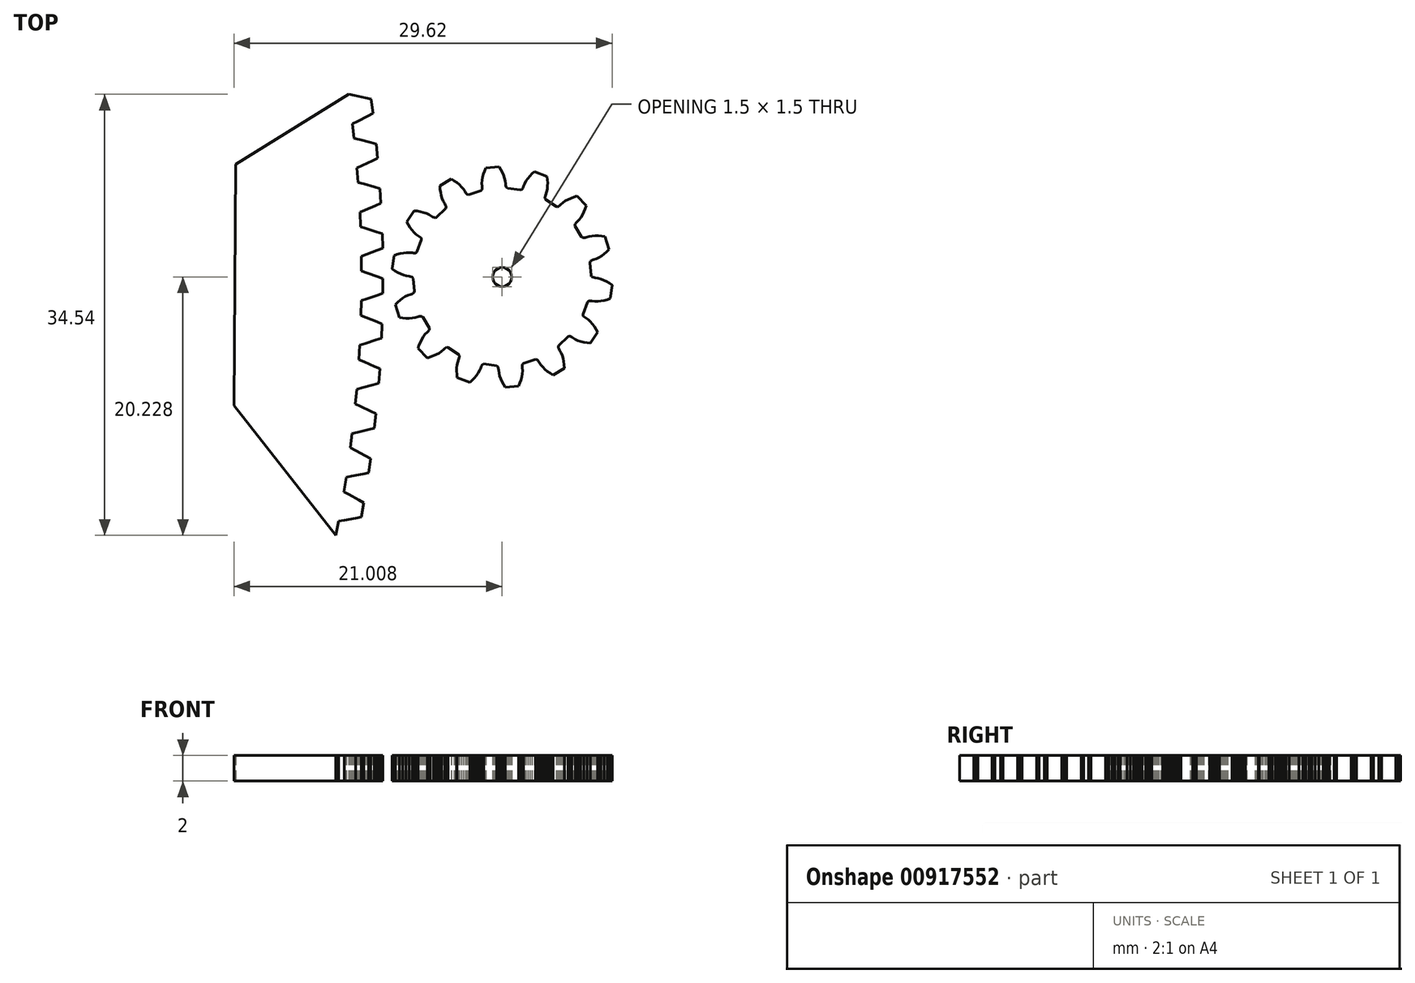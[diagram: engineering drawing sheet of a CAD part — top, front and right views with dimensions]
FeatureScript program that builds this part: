
annotation { "Feature Type Name" : "Feature", "Feature Type Description" : "" }
export const myFeature = defineFeature(function(context is Context, id is Id, definition is map)
    precondition{}
    {
        {
            var Q0;
            Q0=qCreatedBy(makeId("Top.planeOp"),FACE);
            var sketch = newSketch(context, id + "F0", { "sketchPlane" : qUnion([Q0])});
            skLineSegment(sketch, "E0", {"start": v(94.35, 0.47) * mm, "end": v(94.77, 0.32) * mm});
            skLineSegment(sketch, "E1", {"start": v(94.77, 0.32) * mm, "end": v(95.6, 0.02) * mm});
            skLineSegment(sketch, "E2", {"start": v(95.6, 0.02) * mm, "end": v(96.03, -0.14) * mm});
            skLineSegment(sketch, "E3", {"start": v(96.03, -0.14) * mm, "end": v(96.02, -1.27) * mm});
            skLineSegment(sketch, "E4", {"start": v(96.02, -1.27) * mm, "end": v(95.6, -1.43) * mm});
            skLineSegment(sketch, "E5", {"start": v(95.6, -1.43) * mm, "end": v(94.76, -1.72) * mm});
            skLineSegment(sketch, "E6", {"start": v(94.76, -1.72) * mm, "end": v(94.33, -1.86) * mm});
            skLineSegment(sketch, "E7", {"start": v(94.33, -1.86) * mm, "end": v(94.3, -3) * mm});
            skLineSegment(sketch, "E8", {"start": v(94.3, -3) * mm, "end": v(94.72, -3.16) * mm});
            skLineSegment(sketch, "E9", {"start": v(94.72, -3.16) * mm, "end": v(95.55, -3.5) * mm});
            skLineSegment(sketch, "E10", {"start": v(95.55, -3.5) * mm, "end": v(95.97, -3.67) * mm});
            skLineSegment(sketch, "E11", {"start": v(95.97, -3.67) * mm, "end": v(95.92, -4.8) * mm});
            skLineSegment(sketch, "E12", {"start": v(95.92, -4.8) * mm, "end": v(95.5, -4.94) * mm});
            skLineSegment(sketch, "E13", {"start": v(95.5, -4.94) * mm, "end": v(94.64, -5.2) * mm});
            skLineSegment(sketch, "E14", {"start": v(94.64, -5.2) * mm, "end": v(94.21, -5.33) * mm});
            skLineSegment(sketch, "E15", {"start": v(94.21, -5.33) * mm, "end": v(94.15, -6.47) * mm});
            skLineSegment(sketch, "E16", {"start": v(94.15, -6.47) * mm, "end": v(94.56, -6.65) * mm});
            skLineSegment(sketch, "E17", {"start": v(94.56, -6.65) * mm, "end": v(95.37, -7) * mm});
            skLineSegment(sketch, "E18", {"start": v(95.37, -7) * mm, "end": v(95.78, -7.2) * mm});
            skLineSegment(sketch, "E19", {"start": v(95.78, -7.2) * mm, "end": v(95.7, -8.32) * mm});
            skLineSegment(sketch, "E20", {"start": v(95.7, -8.32) * mm, "end": v(95.27, -8.45) * mm});
            skLineSegment(sketch, "E21", {"start": v(95.27, -8.45) * mm, "end": v(94.4, -8.68) * mm});
            skLineSegment(sketch, "E22", {"start": v(94.4, -8.68) * mm, "end": v(93.98, -8.8) * mm});
            skLineSegment(sketch, "E23", {"start": v(93.98, -8.8) * mm, "end": v(93.87, -9.93) * mm});
            skLineSegment(sketch, "E24", {"start": v(93.87, -9.93) * mm, "end": v(94.28, -10.12) * mm});
            skLineSegment(sketch, "E25", {"start": v(94.28, -10.12) * mm, "end": v(95.08, -10.5) * mm});
            skLineSegment(sketch, "E26", {"start": v(95.08, -10.5) * mm, "end": v(95.48, -10.7) * mm});
            skLineSegment(sketch, "E27", {"start": v(95.48, -10.7) * mm, "end": v(95.36, -11.83) * mm});
            skLineSegment(sketch, "E28", {"start": v(95.36, -11.83) * mm, "end": v(94.93, -11.94) * mm});
            skLineSegment(sketch, "E29", {"start": v(94.93, -11.94) * mm, "end": v(94.06, -12.15) * mm});
            skLineSegment(sketch, "E30", {"start": v(94.06, -12.15) * mm, "end": v(93.62, -12.24) * mm});
            skLineSegment(sketch, "E31", {"start": v(93.62, -12.24) * mm, "end": v(93.48, -13.38) * mm});
            skLineSegment(sketch, "E32", {"start": v(93.48, -13.38) * mm, "end": v(93.88, -13.58) * mm});
            skLineSegment(sketch, "E33", {"start": v(93.88, -13.58) * mm, "end": v(94.67, -14) * mm});
            skLineSegment(sketch, "E34", {"start": v(94.67, -14) * mm, "end": v(95.06, -14.21) * mm});
            skLineSegment(sketch, "E35", {"start": v(95.06, -14.21) * mm, "end": v(94.9, -15.33) * mm});
            skLineSegment(sketch, "E36", {"start": v(94.9, -15.33) * mm, "end": v(94.47, -15.43) * mm});
            skLineSegment(sketch, "E37", {"start": v(94.47, -15.43) * mm, "end": v(93.6, -15.6) * mm});
            skLineSegment(sketch, "E38", {"start": v(93.6, -15.6) * mm, "end": v(93.15, -15.68) * mm});
            skLineSegment(sketch, "E39", {"start": v(93.15, -15.68) * mm, "end": v(92.97, -16.82) * mm});
            skLineSegment(sketch, "E40", {"start": v(92.97, -16.82) * mm, "end": v(93.36, -17.03) * mm});
            skLineSegment(sketch, "E41", {"start": v(93.36, -17.03) * mm, "end": v(94.14, -17.47) * mm});
            skLineSegment(sketch, "E42", {"start": v(94.14, -17.47) * mm, "end": v(94.53, -17.7) * mm});
            skLineSegment(sketch, "E43", {"start": v(94.53, -17.7) * mm, "end": v(94.33, -18.81) * mm});
            skLineSegment(sketch, "E44", {"start": v(94.33, -18.81) * mm, "end": v(93.89, -18.9) * mm});
            skLineSegment(sketch, "E45", {"start": v(93.89, -18.9) * mm, "end": v(93, -19.04) * mm});
            skLineSegment(sketch, "E46", {"start": v(93, -19.04) * mm, "end": v(92.57, -19.1) * mm});
            skLineSegment(sketch, "E47", {"start": v(92.57, -19.1) * mm, "end": v(92.35, -20.23) * mm});
            skLineSegment(sketch, "E48", {"start": v(92.35, -20.23) * mm, "end": v(92.73, -20.46) * mm});
            skLineSegment(sketch, "E49", {"start": v(92.73, -20.46) * mm, "end": v(93.5, -20.92) * mm});
            skLineSegment(sketch, "E50", {"start": v(93.5, -20.92) * mm, "end": v(93.87, -21.17) * mm});
            skLineSegment(sketch, "E51", {"start": v(93.87, -21.17) * mm, "end": v(93.64, -22.27) * mm});
            skLineSegment(sketch, "E52", {"start": v(93.64, -22.27) * mm, "end": v(93.2, -22.34) * mm});
            skLineSegment(sketch, "E53", {"start": v(93.2, -22.34) * mm, "end": v(92.31, -22.46) * mm});
            skLineSegment(sketch, "E54", {"start": v(92.31, -22.46) * mm, "end": v(91.87, -22.5) * mm});
            skLineSegment(sketch, "E55", {"start": v(91.87, -22.5) * mm, "end": v(91.61, -23.63) * mm});
            skLineSegment(sketch, "E56", {"start": v(91.61, -23.63) * mm, "end": v(91.99, -23.86) * mm});
            skLineSegment(sketch, "E57", {"start": v(91.99, -23.86) * mm, "end": v(92.73, -24.36) * mm});
            skLineSegment(sketch, "E58", {"start": v(92.73, -24.36) * mm, "end": v(93.1, -24.6) * mm});
            skLineSegment(sketch, "E59", {"start": v(93.1, -24.6) * mm, "end": v(92.83, -25.7) * mm});
            skLineSegment(sketch, "E60", {"start": v(92.83, -25.7) * mm, "end": v(92.39, -25.76) * mm});
            skLineSegment(sketch, "E61", {"start": v(92.39, -25.76) * mm, "end": v(91.5, -25.85) * mm});
            skLineSegment(sketch, "E62", {"start": v(91.5, -25.85) * mm, "end": v(91.06, -25.88) * mm});
            skLineSegment(sketch, "E63", {"start": v(91.06, -25.88) * mm, "end": v(90.76, -27) * mm});
            skLineSegment(sketch, "E64", {"start": v(90.76, -27) * mm, "end": v(91.13, -27.24) * mm});
            skLineSegment(sketch, "E65", {"start": v(91.13, -27.24) * mm, "end": v(91.86, -27.76) * mm});
            skLineSegment(sketch, "E66", {"start": v(91.86, -27.76) * mm, "end": v(92.22, -28.02) * mm});
            skLineSegment(sketch, "E67", {"start": v(92.22, -28.02) * mm, "end": v(91.91, -29.11) * mm});
            skLineSegment(sketch, "E68", {"start": v(91.91, -29.11) * mm, "end": v(91.47, -29.15) * mm});
            skLineSegment(sketch, "E69", {"start": v(91.47, -29.15) * mm, "end": v(90.57, -29.2) * mm});
            skLineSegment(sketch, "E70", {"start": v(90.57, -29.2) * mm, "end": v(90.13, -29.23) * mm});
            skLineSegment(sketch, "E71", {"start": v(90.13, -29.23) * mm, "end": v(89.8, -30.33) * mm});
            skLineSegment(sketch, "E72", {"start": v(89.8, -30.33) * mm, "end": v(90.16, -30.59) * mm});
            skLineSegment(sketch, "E73", {"start": v(90.16, -30.59) * mm, "end": v(90.87, -31.13) * mm});
            skLineSegment(sketch, "E74", {"start": v(90.87, -31.13) * mm, "end": v(91.22, -31.4) * mm});
            skLineSegment(sketch, "E75", {"start": v(91.22, -31.4) * mm, "end": v(90.88, -32.48) * mm});
            skLineSegment(sketch, "E76", {"start": v(90.88, -32.48) * mm, "end": v(90.43, -32.5) * mm});
            skLineSegment(sketch, "E77", {"start": v(90.43, -32.5) * mm, "end": v(89.54, -32.54) * mm});
            skLineSegment(sketch, "E78", {"start": v(89.54, -32.54) * mm, "end": v(89.1, -32.54) * mm});
            skLineSegment(sketch, "E79", {"start": v(89.1, -32.54) * mm, "end": v(88.73, -33.63) * mm});
            skLineSegment(sketch, "E80", {"start": v(88.73, -33.63) * mm, "end": v(89.07, -33.9) * mm});
            skLineSegment(sketch, "E81", {"start": v(89.07, -33.9) * mm, "end": v(89.77, -34.47) * mm});
            skLineSegment(sketch, "E82", {"start": v(89.77, -34.47) * mm, "end": v(90.11, -34.76) * mm});
            skLineSegment(sketch, "E83", {"start": v(90.11, -34.76) * mm, "end": v(89.73, -35.82) * mm});
            skLineSegment(sketch, "E84", {"start": v(89.73, -35.82) * mm, "end": v(89.28, -35.83) * mm});
            skLineSegment(sketch, "E85", {"start": v(89.28, -35.83) * mm, "end": v(88.39, -35.83) * mm});
            skLineSegment(sketch, "E86", {"start": v(88.39, -35.83) * mm, "end": v(87.94, -35.82) * mm});
            skLineSegment(sketch, "E87", {"start": v(87.94, -35.82) * mm, "end": v(87.54, -36.9) * mm});
            skLineSegment(sketch, "E88", {"start": v(87.54, -36.9) * mm, "end": v(87.88, -37.18) * mm});
            skLineSegment(sketch, "E89", {"start": v(87.88, -37.18) * mm, "end": v(88.55, -37.76) * mm});
            skLineSegment(sketch, "E90", {"start": v(88.55, -37.76) * mm, "end": v(88.89, -38.07) * mm});
            skLineSegment(sketch, "E91", {"start": v(88.89, -38.07) * mm, "end": v(88.47, -39.12) * mm});
            skLineSegment(sketch, "E92", {"start": v(88.47, -39.12) * mm, "end": v(88.02, -39.1) * mm});
            skLineSegment(sketch, "E93", {"start": v(88.02, -39.1) * mm, "end": v(87.13, -39.08) * mm});
            skLineSegment(sketch, "E94", {"start": v(87.13, -39.08) * mm, "end": v(86.69, -39.05) * mm});
            skLineSegment(sketch, "E95", {"start": v(86.69, -39.05) * mm, "end": v(86.25, -40.11) * mm});
            skLineSegment(sketch, "E96", {"start": v(86.25, -40.11) * mm, "end": v(86.58, -40.41) * mm});
            skLineSegment(sketch, "E97", {"start": v(86.58, -40.41) * mm, "end": v(87.23, -41.02) * mm});
            skLineSegment(sketch, "E98", {"start": v(87.23, -41.02) * mm, "end": v(87.55, -41.33) * mm});
            skLineSegment(sketch, "E99", {"start": v(87.55, -41.33) * mm, "end": v(87.1, -42.37) * mm});
            skLineSegment(sketch, "E100", {"start": v(87.1, -42.37) * mm, "end": v(86.65, -42.35) * mm});
            skLineSegment(sketch, "E101", {"start": v(86.65, -42.35) * mm, "end": v(85.76, -42.28) * mm});
            skLineSegment(sketch, "E102", {"start": v(85.76, -42.28) * mm, "end": v(85.32, -42.24) * mm});
            skLineSegment(sketch, "E103", {"start": v(85.32, -42.24) * mm, "end": v(84.85, -43.3) * mm});
            skLineSegment(sketch, "E104", {"start": v(84.85, -43.3) * mm, "end": v(85.17, -43.6) * mm});
            skLineSegment(sketch, "E105", {"start": v(85.17, -43.6) * mm, "end": v(85.8, -44.23) * mm});
            skLineSegment(sketch, "E106", {"start": v(85.8, -44.23) * mm, "end": v(86.11, -44.55) * mm});
            skLineSegment(sketch, "E107", {"start": v(86.11, -44.55) * mm, "end": v(85.63, -45.57) * mm});
            skLineSegment(sketch, "E108", {"start": v(85.63, -45.57) * mm, "end": v(85.18, -45.53) * mm});
            skLineSegment(sketch, "E109", {"start": v(85.18, -45.53) * mm, "end": v(84.29, -45.44) * mm});
            skLineSegment(sketch, "E110", {"start": v(84.29, -45.44) * mm, "end": v(83.85, -45.39) * mm});
            skLineSegment(sketch, "E111", {"start": v(83.85, -45.39) * mm, "end": v(83.34, -46.42) * mm});
            skLineSegment(sketch, "E112", {"start": v(83.34, -46.42) * mm, "end": v(83.65, -46.74) * mm});
            skLineSegment(sketch, "E113", {"start": v(83.65, -46.74) * mm, "end": v(84.26, -47.39) * mm});
            skLineSegment(sketch, "E114", {"start": v(84.26, -47.39) * mm, "end": v(84.56, -47.72) * mm});
            skLineSegment(sketch, "E115", {"start": v(84.56, -47.72) * mm, "end": v(84.04, -48.72) * mm});
            skLineSegment(sketch, "E116", {"start": v(84.04, -48.72) * mm, "end": v(83.6, -48.67) * mm});
            skLineSegment(sketch, "E117", {"start": v(83.6, -48.67) * mm, "end": v(82.71, -48.55) * mm});
            skLineSegment(sketch, "E118", {"start": v(82.71, -48.55) * mm, "end": v(82.27, -48.48) * mm});
            skLineSegment(sketch, "E119", {"start": v(82.27, -48.48) * mm, "end": v(81.73, -49.5) * mm});
            skLineSegment(sketch, "E120", {"start": v(81.73, -49.5) * mm, "end": v(82.03, -49.82) * mm});
            skLineSegment(sketch, "E121", {"start": v(82.03, -49.82) * mm, "end": v(82.61, -50.5) * mm});
            skLineSegment(sketch, "E122", {"start": v(82.61, -50.5) * mm, "end": v(82.9, -50.84) * mm});
            skLineSegment(sketch, "E123", {"start": v(82.9, -50.84) * mm, "end": v(82.35, -51.82) * mm});
            skLineSegment(sketch, "E124", {"start": v(82.35, -51.82) * mm, "end": v(81.9, -51.75) * mm});
            skLineSegment(sketch, "E125", {"start": v(81.9, -51.75) * mm, "end": v(81.03, -51.6) * mm});
            skLineSegment(sketch, "E126", {"start": v(81.03, -51.6) * mm, "end": v(80.6, -51.52) * mm});
            skLineSegment(sketch, "E127", {"start": v(80.6, -51.52) * mm, "end": v(80.01, -52.51) * mm});
            skLineSegment(sketch, "E128", {"start": v(80.01, -52.51) * mm, "end": v(80.3, -52.85) * mm});
            skLineSegment(sketch, "E129", {"start": v(80.3, -52.85) * mm, "end": v(80.87, -53.54) * mm});
            skLineSegment(sketch, "E130", {"start": v(80.87, -53.54) * mm, "end": v(81.15, -53.9) * mm});
            skLineSegment(sketch, "E131", {"start": v(81.15, -53.9) * mm, "end": v(80.56, -54.86) * mm});
            skLineSegment(sketch, "E132", {"start": v(80.56, -54.86) * mm, "end": v(80.12, -54.78) * mm});
            skLineSegment(sketch, "E133", {"start": v(80.12, -54.78) * mm, "end": v(79.24, -54.6) * mm});
            skLineSegment(sketch, "E134", {"start": v(79.24, -54.6) * mm, "end": v(78.81, -54.5) * mm});
            skLineSegment(sketch, "E135", {"start": v(78.81, -54.5) * mm, "end": v(78.2, -55.47) * mm});
            skLineSegment(sketch, "E136", {"start": v(78.2, -55.47) * mm, "end": v(78.48, -55.82) * mm});
            skLineSegment(sketch, "E137", {"start": v(78.48, -55.82) * mm, "end": v(79.02, -56.53) * mm});
            skLineSegment(sketch, "E138", {"start": v(79.02, -56.53) * mm, "end": v(79.28, -56.9) * mm});
            skLineSegment(sketch, "E139", {"start": v(79.28, -56.9) * mm, "end": v(78.67, -57.84) * mm});
            skLineSegment(sketch, "E140", {"start": v(78.67, -57.84) * mm, "end": v(78.23, -57.74) * mm});
            skLineSegment(sketch, "E141", {"start": v(78.23, -57.74) * mm, "end": v(77.36, -57.53) * mm});
            skLineSegment(sketch, "E142", {"start": v(77.36, -57.53) * mm, "end": v(76.93, -57.42) * mm});
            skLineSegment(sketch, "E143", {"start": v(76.93, -57.42) * mm, "end": v(76.29, -58.37) * mm});
            skLineSegment(sketch, "E144", {"start": v(76.29, -58.37) * mm, "end": v(76.55, -58.73) * mm});
            skLineSegment(sketch, "E145", {"start": v(76.55, -58.73) * mm, "end": v(77.07, -59.45) * mm});
            skLineSegment(sketch, "E146", {"start": v(77.07, -59.45) * mm, "end": v(77.32, -59.82) * mm});
            skLineSegment(sketch, "E147", {"start": v(77.32, -59.82) * mm, "end": v(76.67, -60.75) * mm});
            skLineSegment(sketch, "E148", {"start": v(76.67, -60.75) * mm, "end": v(76.24, -60.64) * mm});
            skLineSegment(sketch, "E149", {"start": v(76.24, -60.64) * mm, "end": v(75.38, -60.4) * mm});
            skLineSegment(sketch, "E150", {"start": v(75.38, -60.4) * mm, "end": v(74.95, -60.27) * mm});
            skLineSegment(sketch, "E151", {"start": v(74.95, -60.27) * mm, "end": v(74.28, -61.2) * mm});
            skLineSegment(sketch, "E152", {"start": v(74.28, -61.2) * mm, "end": v(74.53, -61.57) * mm});
            skLineSegment(sketch, "E153", {"start": v(74.53, -61.57) * mm, "end": v(75.02, -62.31) * mm});
            skLineSegment(sketch, "E154", {"start": v(75.02, -62.31) * mm, "end": v(75.26, -62.69) * mm});
            skLineSegment(sketch, "E155", {"start": v(75.26, -62.69) * mm, "end": v(74.59, -63.6) * mm});
            skLineSegment(sketch, "E156", {"start": v(74.59, -63.6) * mm, "end": v(74.15, -63.47) * mm});
            skLineSegment(sketch, "E157", {"start": v(74.15, -63.47) * mm, "end": v(73.3, -63.2) * mm});
            skLineSegment(sketch, "E158", {"start": v(73.3, -63.2) * mm, "end": v(72.88, -63.06) * mm});
            skLineSegment(sketch, "E159", {"start": v(72.88, -63.06) * mm, "end": v(72.17, -63.96) * mm});
            skLineSegment(sketch, "E160", {"start": v(72.17, -63.96) * mm, "end": v(72.41, -64.34) * mm});
            skLineSegment(sketch, "E161", {"start": v(72.41, -64.34) * mm, "end": v(72.88, -65.1) * mm});
            skLineSegment(sketch, "E162", {"start": v(72.88, -65.1) * mm, "end": v(73.11, -65.48) * mm});
            skLineSegment(sketch, "E163", {"start": v(73.11, -65.48) * mm, "end": v(72.4, -66.36) * mm});
            skLineSegment(sketch, "E164", {"start": v(72.4, -66.36) * mm, "end": v(71.98, -66.22) * mm});
            skLineSegment(sketch, "E165", {"start": v(71.98, -66.22) * mm, "end": v(71.13, -65.93) * mm});
            skLineSegment(sketch, "E166", {"start": v(71.13, -65.93) * mm, "end": v(70.72, -65.77) * mm});
            skLineSegment(sketch, "E167", {"start": v(70.72, -65.77) * mm, "end": v(69.98, -66.65) * mm});
            skLineSegment(sketch, "E168", {"start": v(69.98, -66.65) * mm, "end": v(70.2, -67.03) * mm});
            skLineSegment(sketch, "E169", {"start": v(70.2, -67.03) * mm, "end": v(70.65, -67.81) * mm});
            skLineSegment(sketch, "E170", {"start": v(70.65, -67.81) * mm, "end": v(70.87, -68.2) * mm});
            skLineSegment(sketch, "E171", {"start": v(70.87, -68.2) * mm, "end": v(70.13, -69.06) * mm});
            skLineSegment(sketch, "E172", {"start": v(70.13, -69.06) * mm, "end": v(69.7, -68.9) * mm});
            skLineSegment(sketch, "E173", {"start": v(69.7, -68.9) * mm, "end": v(68.87, -68.58) * mm});
            skLineSegment(sketch, "E174", {"start": v(68.87, -68.58) * mm, "end": v(68.46, -68.41) * mm});
            skLineSegment(sketch, "E175", {"start": v(68.46, -68.41) * mm, "end": v(67.7, -69.27) * mm});
            skLineSegment(sketch, "E176", {"start": v(67.7, -69.27) * mm, "end": v(67.91, -69.66) * mm});
            skLineSegment(sketch, "E177", {"start": v(67.91, -69.66) * mm, "end": v(68.33, -70.45) * mm});
            skLineSegment(sketch, "E178", {"start": v(68.33, -70.45) * mm, "end": v(68.53, -70.85) * mm});
            skLineSegment(sketch, "E179", {"start": v(68.53, -70.85) * mm, "end": v(67.76, -71.68) * mm});
            skLineSegment(sketch, "E180", {"start": v(67.76, -71.68) * mm, "end": v(67.35, -71.5) * mm});
            skLineSegment(sketch, "E181", {"start": v(67.35, -71.5) * mm, "end": v(66.52, -71.16) * mm});
            skLineSegment(sketch, "E182", {"start": v(66.52, -71.16) * mm, "end": v(66.12, -70.97) * mm});
            skLineSegment(sketch, "E183", {"start": v(66.12, -70.97) * mm, "end": v(65.33, -71.8) * mm});
            skLineSegment(sketch, "E184", {"start": v(65.33, -71.8) * mm, "end": v(65.53, -72.2) * mm});
            skLineSegment(sketch, "E185", {"start": v(65.53, -72.2) * mm, "end": v(65.92, -73) * mm});
            skLineSegment(sketch, "E186", {"start": v(65.92, -73) * mm, "end": v(66.1, -73.41) * mm});
            skLineSegment(sketch, "E187", {"start": v(66.1, -73.41) * mm, "end": v(65.31, -74.22) * mm});
            skLineSegment(sketch, "E188", {"start": v(65.31, -74.22) * mm, "end": v(64.9, -74.03) * mm});
            skLineSegment(sketch, "E189", {"start": v(64.9, -74.03) * mm, "end": v(64.1, -73.65) * mm});
            skLineSegment(sketch, "E190", {"start": v(64.1, -73.65) * mm, "end": v(63.7, -73.46) * mm});
            skLineSegment(sketch, "E191", {"start": v(63.7, -73.46) * mm, "end": v(62.87, -74.26) * mm});
            skLineSegment(sketch, "E192", {"start": v(62.87, -74.26) * mm, "end": v(63.06, -74.66) * mm});
            skLineSegment(sketch, "E193", {"start": v(63.06, -74.66) * mm, "end": v(63.42, -75.48) * mm});
            skLineSegment(sketch, "E194", {"start": v(63.42, -75.48) * mm, "end": v(63.6, -75.9) * mm});
            skLineSegment(sketch, "E195", {"start": v(63.6, -75.9) * mm, "end": v(62.78, -76.67) * mm});
            skLineSegment(sketch, "E196", {"start": v(62.78, -76.67) * mm, "end": v(62.37, -76.47) * mm});
            skLineSegment(sketch, "E197", {"start": v(62.37, -76.47) * mm, "end": v(61.58, -76.07) * mm});
            skLineSegment(sketch, "E198", {"start": v(61.58, -76.07) * mm, "end": v(61.18, -75.86) * mm});
            skLineSegment(sketch, "E199", {"start": v(61.18, -75.86) * mm, "end": v(60.34, -76.63) * mm});
            skLineSegment(sketch, "E200", {"start": v(60.34, -76.63) * mm, "end": v(60.51, -77.04) * mm});
            skLineSegment(sketch, "E201", {"start": v(60.51, -77.04) * mm, "end": v(60.85, -77.87) * mm});
            skLineSegment(sketch, "E202", {"start": v(60.85, -77.87) * mm, "end": v(61, -78.29) * mm});
            skLineSegment(sketch, "E203", {"start": v(61, -78.29) * mm, "end": v(60.16, -79.04) * mm});
            skLineSegment(sketch, "E204", {"start": v(60.16, -79.04) * mm, "end": v(59.76, -78.83) * mm});
            skLineSegment(sketch, "E205", {"start": v(59.76, -78.83) * mm, "end": v(58.98, -78.4) * mm});
            skLineSegment(sketch, "E206", {"start": v(58.98, -78.4) * mm, "end": v(58.6, -78.17) * mm});
            skLineSegment(sketch, "E207", {"start": v(58.6, -78.17) * mm, "end": v(57.72, -78.92) * mm});
            skLineSegment(sketch, "E208", {"start": v(57.72, -78.92) * mm, "end": v(57.88, -79.33) * mm});
            skLineSegment(sketch, "E209", {"start": v(57.88, -79.33) * mm, "end": v(58.2, -80.17) * mm});
            skLineSegment(sketch, "E210", {"start": v(58.2, -80.17) * mm, "end": v(58.34, -80.6) * mm});
            skLineSegment(sketch, "E211", {"start": v(58.34, -80.6) * mm, "end": v(57.47, -81.31) * mm});
            skLineSegment(sketch, "E212", {"start": v(57.47, -81.31) * mm, "end": v(57.08, -81.1) * mm});
            skLineSegment(sketch, "E213", {"start": v(57.08, -81.1) * mm, "end": v(56.3, -80.63) * mm});
            skLineSegment(sketch, "E214", {"start": v(56.3, -80.63) * mm, "end": v(55.93, -80.4) * mm});
            skLineSegment(sketch, "E215", {"start": v(55.93, -80.4) * mm, "end": v(55.04, -81.11) * mm});
            skLineSegment(sketch, "E216", {"start": v(55.04, -81.11) * mm, "end": v(55.18, -81.53) * mm});
            skLineSegment(sketch, "E217", {"start": v(55.18, -81.53) * mm, "end": v(55.46, -82.38) * mm});
            skLineSegment(sketch, "E218", {"start": v(55.46, -82.38) * mm, "end": v(55.6, -82.81) * mm});
            skLineSegment(sketch, "E219", {"start": v(55.6, -82.81) * mm, "end": v(54.7, -83.5) * mm});
            skLineSegment(sketch, "E220", {"start": v(54.7, -83.5) * mm, "end": v(54.31, -83.26) * mm});
            skLineSegment(sketch, "E221", {"start": v(54.31, -83.26) * mm, "end": v(53.56, -82.78) * mm});
            skLineSegment(sketch, "E222", {"start": v(53.56, -82.78) * mm, "end": v(53.2, -82.53) * mm});
            skLineSegment(sketch, "E223", {"start": v(53.2, -82.53) * mm, "end": v(52.27, -83.22) * mm});
            skLineSegment(sketch, "E224", {"start": v(52.27, -83.22) * mm, "end": v(52.4, -83.64) * mm});
            skLineSegment(sketch, "E225", {"start": v(52.4, -83.64) * mm, "end": v(52.66, -84.5) * mm});
            skLineSegment(sketch, "E226", {"start": v(52.66, -84.5) * mm, "end": v(52.77, -84.93) * mm});
            skLineSegment(sketch, "E227", {"start": v(52.77, -84.93) * mm, "end": v(51.86, -85.6) * mm});
            skLineSegment(sketch, "E228", {"start": v(51.86, -85.6) * mm, "end": v(51.48, -85.34) * mm});
            skLineSegment(sketch, "E229", {"start": v(51.48, -85.34) * mm, "end": v(50.75, -84.83) * mm});
            skLineSegment(sketch, "E230", {"start": v(50.75, -84.83) * mm, "end": v(50.39, -84.57) * mm});
            skLineSegment(sketch, "E231", {"start": v(50.39, -84.57) * mm, "end": v(49.44, -85.23) * mm});
            skLineSegment(sketch, "E232", {"start": v(49.44, -85.23) * mm, "end": v(49.56, -85.66) * mm});
            skLineSegment(sketch, "E233", {"start": v(49.56, -85.66) * mm, "end": v(49.78, -86.52) * mm});
            skLineSegment(sketch, "E234", {"start": v(49.78, -86.52) * mm, "end": v(49.89, -86.96) * mm});
            skLineSegment(sketch, "E235", {"start": v(49.89, -86.96) * mm, "end": v(48.95, -87.59) * mm});
            skLineSegment(sketch, "E236", {"start": v(48.95, -87.59) * mm, "end": v(48.58, -87.33) * mm});
            skLineSegment(sketch, "E237", {"start": v(48.58, -87.33) * mm, "end": v(47.86, -86.8) * mm});
            skLineSegment(sketch, "E238", {"start": v(47.86, -86.8) * mm, "end": v(47.51, -86.52) * mm});
            skLineSegment(sketch, "E239", {"start": v(47.51, -86.52) * mm, "end": v(46.55, -87.14) * mm});
            skLineSegment(sketch, "E240", {"start": v(46.55, -87.14) * mm, "end": v(46.65, -87.57) * mm});
            skLineSegment(sketch, "E241", {"start": v(46.65, -87.57) * mm, "end": v(46.84, -88.45) * mm});
            skLineSegment(sketch, "E242", {"start": v(46.84, -88.45) * mm, "end": v(46.93, -88.89) * mm});
            skLineSegment(sketch, "E243", {"start": v(46.93, -88.89) * mm, "end": v(45.97, -89.48) * mm});
            skLineSegment(sketch, "E244", {"start": v(45.97, -89.48) * mm, "end": v(45.61, -89.21) * mm});
            skLineSegment(sketch, "E245", {"start": v(45.61, -89.21) * mm, "end": v(44.92, -88.65) * mm});
            skLineSegment(sketch, "E246", {"start": v(44.92, -88.65) * mm, "end": v(44.58, -88.37) * mm});
            skLineSegment(sketch, "E247", {"start": v(44.58, -88.37) * mm, "end": v(43.59, -88.96) * mm});
            skLineSegment(sketch, "E248", {"start": v(43.59, -88.96) * mm, "end": v(43.68, -89.4) * mm});
            skLineSegment(sketch, "E249", {"start": v(43.68, -89.4) * mm, "end": v(43.84, -90.27) * mm});
            skLineSegment(sketch, "E250", {"start": v(43.84, -90.27) * mm, "end": v(43.91, -90.72) * mm});
            skLineSegment(sketch, "E251", {"start": v(43.91, -90.72) * mm, "end": v(42.93, -91.28) * mm});
            skLineSegment(sketch, "E252", {"start": v(42.93, -91.28) * mm, "end": v(42.59, -91) * mm});
            skLineSegment(sketch, "E253", {"start": v(42.59, -91) * mm, "end": v(41.9, -90.41) * mm});
            skLineSegment(sketch, "E254", {"start": v(41.9, -90.41) * mm, "end": v(41.58, -90.12) * mm});
            skLineSegment(sketch, "E255", {"start": v(41.58, -90.12) * mm, "end": v(40.57, -90.67) * mm});
            skLineSegment(sketch, "E256", {"start": v(40.57, -90.67) * mm, "end": v(40.65, -91.11) * mm});
            skLineSegment(sketch, "E257", {"start": v(40.65, -91.11) * mm, "end": v(40.78, -92) * mm});
            skLineSegment(sketch, "E258", {"start": v(40.78, -92) * mm, "end": v(40.84, -92.44) * mm});
            skLineSegment(sketch, "E259", {"start": v(40.84, -92.44) * mm, "end": v(39.84, -92.97) * mm});
            skLineSegment(sketch, "E260", {"start": v(39.84, -92.97) * mm, "end": v(39.5, -92.67) * mm});
            skLineSegment(sketch, "E261", {"start": v(39.5, -92.67) * mm, "end": v(38.84, -92.07) * mm});
            skLineSegment(sketch, "E262", {"start": v(38.84, -92.07) * mm, "end": v(38.52, -91.77) * mm});
            skLineSegment(sketch, "E263", {"start": v(38.52, -91.77) * mm, "end": v(37.5, -92.29) * mm});
            skLineSegment(sketch, "E264", {"start": v(37.5, -92.29) * mm, "end": v(37.56, -92.73) * mm});
            skLineSegment(sketch, "E265", {"start": v(37.56, -92.73) * mm, "end": v(37.66, -93.62) * mm});
            skLineSegment(sketch, "E266", {"start": v(37.66, -93.62) * mm, "end": v(37.7, -94.06) * mm});
            skLineSegment(sketch, "E267", {"start": v(37.7, -94.06) * mm, "end": v(36.69, -94.56) * mm});
            skLineSegment(sketch, "E268", {"start": v(36.69, -94.56) * mm, "end": v(36.36, -94.25) * mm});
            skLineSegment(sketch, "E269", {"start": v(36.36, -94.25) * mm, "end": v(35.72, -93.63) * mm});
            skLineSegment(sketch, "E270", {"start": v(35.72, -93.63) * mm, "end": v(35.41, -93.3) * mm});
            skLineSegment(sketch, "E271", {"start": v(35.41, -93.3) * mm, "end": v(34.37, -93.8) * mm});
            skLineSegment(sketch, "E272", {"start": v(34.37, -93.8) * mm, "end": v(34.42, -94.24) * mm});
            skLineSegment(sketch, "E273", {"start": v(34.42, -94.24) * mm, "end": v(34.49, -95.13) * mm});
            skLineSegment(sketch, "E274", {"start": v(34.49, -95.13) * mm, "end": v(34.52, -95.58) * mm});
            skLineSegment(sketch, "E275", {"start": v(34.52, -95.58) * mm, "end": v(33.49, -96.04) * mm});
            skLineSegment(sketch, "E276", {"start": v(33.49, -96.04) * mm, "end": v(33.17, -95.72) * mm});
            skLineSegment(sketch, "E277", {"start": v(33.17, -95.72) * mm, "end": v(32.55, -95.07) * mm});
            skLineSegment(sketch, "E278", {"start": v(32.55, -95.07) * mm, "end": v(32.25, -94.75) * mm});
            skLineSegment(sketch, "E279", {"start": v(32.25, -94.75) * mm, "end": v(31.2, -95.2) * mm});
            skLineSegment(sketch, "E280", {"start": v(31.2, -95.2) * mm, "end": v(31.23, -95.64) * mm});
            skLineSegment(sketch, "E281", {"start": v(31.23, -95.64) * mm, "end": v(31.27, -96.54) * mm});
            skLineSegment(sketch, "E282", {"start": v(31.27, -96.54) * mm, "end": v(31.28, -96.98) * mm});
            skLineSegment(sketch, "E283", {"start": v(31.28, -96.98) * mm, "end": v(30.24, -97.41) * mm});
            skLineSegment(sketch, "E284", {"start": v(30.24, -97.41) * mm, "end": v(29.93, -97.08) * mm});
            skLineSegment(sketch, "E285", {"start": v(29.93, -97.08) * mm, "end": v(29.33, -96.42) * mm});
            skLineSegment(sketch, "E286", {"start": v(29.33, -96.42) * mm, "end": v(29.05, -96.08) * mm});
            skLineSegment(sketch, "E287", {"start": v(29.05, -96.08) * mm, "end": v(27.98, -96.5) * mm});
            skLineSegment(sketch, "E288", {"start": v(27.98, -96.5) * mm, "end": v(27.99, -96.94) * mm});
            skLineSegment(sketch, "E289", {"start": v(27.99, -96.94) * mm, "end": v(28, -97.83) * mm});
            skLineSegment(sketch, "E290", {"start": v(28, -97.83) * mm, "end": v(28, -98.28) * mm});
            skLineSegment(sketch, "E291", {"start": v(28, -98.28) * mm, "end": v(26.94, -98.67) * mm});
            skLineSegment(sketch, "E292", {"start": v(26.94, -98.67) * mm, "end": v(26.65, -98.33) * mm});
            skLineSegment(sketch, "E293", {"start": v(26.65, -98.33) * mm, "end": v(26.07, -97.65) * mm});
            skLineSegment(sketch, "E294", {"start": v(26.07, -97.65) * mm, "end": v(25.8, -97.3) * mm});
            skLineSegment(sketch, "E295", {"start": v(25.8, -97.3) * mm, "end": v(24.71, -97.68) * mm});
            skLineSegment(sketch, "E296", {"start": v(24.71, -97.68) * mm, "end": v(24.71, -98.13) * mm});
            skLineSegment(sketch, "E297", {"start": v(24.71, -98.13) * mm, "end": v(24.7, -99.02) * mm});
            skLineSegment(sketch, "E298", {"start": v(24.7, -99.02) * mm, "end": v(24.68, -99.47) * mm});
            skLineSegment(sketch, "E299", {"start": v(24.68, -99.47) * mm, "end": v(23.6, -99.83) * mm});
            skLineSegment(sketch, "E300", {"start": v(23.6, -99.83) * mm, "end": v(23.32, -99.48) * mm});
            skLineSegment(sketch, "E301", {"start": v(23.32, -99.48) * mm, "end": v(22.77, -98.77) * mm});
            skLineSegment(sketch, "E302", {"start": v(22.77, -98.77) * mm, "end": v(22.5, -98.42) * mm});
            skLineSegment(sketch, "E303", {"start": v(22.5, -98.42) * mm, "end": v(21.41, -98.76) * mm});
            skLineSegment(sketch, "E304", {"start": v(21.41, -98.76) * mm, "end": v(21.4, -99.2) * mm});
            skLineSegment(sketch, "E305", {"start": v(21.4, -99.2) * mm, "end": v(21.35, -100.1) * mm});
            skLineSegment(sketch, "E306", {"start": v(21.35, -100.1) * mm, "end": v(21.32, -100.54) * mm});
            skLineSegment(sketch, "E307", {"start": v(21.32, -100.54) * mm, "end": v(20.23, -100.86) * mm});
            skLineSegment(sketch, "E308", {"start": v(20.23, -100.86) * mm, "end": v(19.96, -100.5) * mm});
            skLineSegment(sketch, "E309", {"start": v(19.96, -100.5) * mm, "end": v(19.44, -99.78) * mm});
            skLineSegment(sketch, "E310", {"start": v(19.44, -99.78) * mm, "end": v(19.18, -99.42) * mm});
            skLineSegment(sketch, "E311", {"start": v(19.18, -99.42) * mm, "end": v(18.08, -99.72) * mm});
            skLineSegment(sketch, "E312", {"start": v(18.08, -99.72) * mm, "end": v(18.05, -100.17) * mm});
            skLineSegment(sketch, "E313", {"start": v(18.05, -100.17) * mm, "end": v(17.97, -101.06) * mm});
            skLineSegment(sketch, "E314", {"start": v(17.97, -101.06) * mm, "end": v(17.92, -101.5) * mm});
            skLineSegment(sketch, "E315", {"start": v(17.92, -101.5) * mm, "end": v(16.83, -101.79) * mm});
            skLineSegment(sketch, "E316", {"start": v(16.83, -101.79) * mm, "end": v(16.57, -101.42) * mm});
            skLineSegment(sketch, "E317", {"start": v(16.57, -101.42) * mm, "end": v(16.07, -100.68) * mm});
            skLineSegment(sketch, "E318", {"start": v(16.07, -100.68) * mm, "end": v(15.83, -100.3) * mm});
            skLineSegment(sketch, "E319", {"start": v(15.83, -100.3) * mm, "end": v(14.71, -100.58) * mm});
            skLineSegment(sketch, "E320", {"start": v(14.71, -100.58) * mm, "end": v(14.67, -101.02) * mm});
            skLineSegment(sketch, "E321", {"start": v(14.67, -101.02) * mm, "end": v(14.56, -101.9) * mm});
            skLineSegment(sketch, "E322", {"start": v(14.56, -101.9) * mm, "end": v(14.5, -102.35) * mm});
            skLineSegment(sketch, "E323", {"start": v(14.5, -102.35) * mm, "end": v(13.4, -102.6) * mm});
            skLineSegment(sketch, "E324", {"start": v(13.4, -102.6) * mm, "end": v(13.15, -102.22) * mm});
            skLineSegment(sketch, "E325", {"start": v(13.15, -102.22) * mm, "end": v(12.67, -101.46) * mm});
            skLineSegment(sketch, "E326", {"start": v(12.67, -101.46) * mm, "end": v(12.45, -101.08) * mm});
            skLineSegment(sketch, "E327", {"start": v(12.45, -101.08) * mm, "end": v(11.32, -101.32) * mm});
            skLineSegment(sketch, "E328", {"start": v(11.32, -101.32) * mm, "end": v(11.26, -101.76) * mm});
            skLineSegment(sketch, "E329", {"start": v(11.26, -101.76) * mm, "end": v(11.12, -102.64) * mm});
            skLineSegment(sketch, "E330", {"start": v(11.12, -102.64) * mm, "end": v(11.05, -103.08) * mm});
            skLineSegment(sketch, "E331", {"start": v(11.05, -103.08) * mm, "end": v(9.94, -103.3) * mm});
            skLineSegment(sketch, "E332", {"start": v(9.94, -103.3) * mm, "end": v(9.7, -102.9) * mm});
            skLineSegment(sketch, "E333", {"start": v(9.7, -102.9) * mm, "end": v(9.25, -102.13) * mm});
            skLineSegment(sketch, "E334", {"start": v(9.25, -102.13) * mm, "end": v(9.04, -101.75) * mm});
            skLineSegment(sketch, "E335", {"start": v(9.04, -101.75) * mm, "end": v(7.9, -101.94) * mm});
            skLineSegment(sketch, "E336", {"start": v(7.9, -101.94) * mm, "end": v(7.83, -102.38) * mm});
            skLineSegment(sketch, "E337", {"start": v(7.83, -102.38) * mm, "end": v(7.66, -103.26) * mm});
            skLineSegment(sketch, "E338", {"start": v(7.66, -103.26) * mm, "end": v(7.57, -103.7) * mm});
            skLineSegment(sketch, "E339", {"start": v(7.57, -103.7) * mm, "end": v(6.46, -103.87) * mm});
            skLineSegment(sketch, "E340", {"start": v(6.46, -103.87) * mm, "end": v(6.24, -103.48) * mm});
            skLineSegment(sketch, "E341", {"start": v(6.24, -103.48) * mm, "end": v(5.81, -102.69) * mm});
            skLineSegment(sketch, "E342", {"start": v(5.81, -102.69) * mm, "end": v(5.6, -102.3) * mm});
            skLineSegment(sketch, "E343", {"start": v(5.6, -102.3) * mm, "end": v(4.47, -102.45) * mm});
            skLineSegment(sketch, "E344", {"start": v(4.47, -102.45) * mm, "end": v(4.38, -102.89) * mm});
            skLineSegment(sketch, "E345", {"start": v(4.38, -102.89) * mm, "end": v(4.19, -103.76) * mm});
            skLineSegment(sketch, "E346", {"start": v(4.19, -103.76) * mm, "end": v(4.08, -104.2) * mm});
            skLineSegment(sketch, "E347", {"start": v(4.08, -104.2) * mm, "end": v(2.96, -104.33) * mm});
            skLineSegment(sketch, "E348", {"start": v(2.96, -104.33) * mm, "end": v(2.75, -103.93) * mm});
            skLineSegment(sketch, "E349", {"start": v(2.75, -103.93) * mm, "end": v(2.35, -103.13) * mm});
            skLineSegment(sketch, "E350", {"start": v(2.35, -103.13) * mm, "end": v(2.16, -102.73) * mm});
            skLineSegment(sketch, "E351", {"start": v(2.16, -102.73) * mm, "end": v(1.02, -102.84) * mm});
            skLineSegment(sketch, "E352", {"start": v(1.02, -102.84) * mm, "end": v(0.92, -103.28) * mm});
            skLineSegment(sketch, "E353", {"start": v(0.92, -103.28) * mm, "end": v(0.7, -104.14) * mm});
            skLineSegment(sketch, "E354", {"start": v(0.7, -104.14) * mm, "end": v(0.57, -104.57) * mm});
            skLineSegment(sketch, "E355", {"start": v(0.57, -104.57) * mm, "end": v(-0.55, -104.67) * mm});
            skLineSegment(sketch, "E356", {"start": v(-0.55, -104.67) * mm, "end": v(-0.75, -104.26) * mm});
            skLineSegment(sketch, "E357", {"start": v(-0.75, -104.26) * mm, "end": v(-1.12, -103.45) * mm});
            skLineSegment(sketch, "E358", {"start": v(-1.12, -103.45) * mm, "end": v(-1.3, -103.04) * mm});
            skLineSegment(sketch, "E359", {"start": v(-1.3, -103.04) * mm, "end": v(-2.44, -103.12) * mm});
            skLineSegment(sketch, "E360", {"start": v(-2.44, -103.12) * mm, "end": v(-2.56, -103.55) * mm});
            skLineSegment(sketch, "E361", {"start": v(-2.56, -103.55) * mm, "end": v(-2.81, -104.4) * mm});
            skLineSegment(sketch, "E362", {"start": v(-2.81, -104.4) * mm, "end": v(-2.95, -104.84) * mm});
            skLineSegment(sketch, "E363", {"start": v(-2.95, -104.84) * mm, "end": v(-4.08, -104.9) * mm});
            skLineSegment(sketch, "E364", {"start": v(-4.08, -104.9) * mm, "end": v(-4.25, -104.48) * mm});
            skLineSegment(sketch, "E365", {"start": v(-4.25, -104.48) * mm, "end": v(-4.6, -103.66) * mm});
            skLineSegment(sketch, "E366", {"start": v(-4.6, -103.66) * mm, "end": v(-4.76, -103.24) * mm});
            skLineSegment(sketch, "E367", {"start": v(-4.76, -103.24) * mm, "end": v(-5.9, -103.28) * mm});
            skLineSegment(sketch, "E368", {"start": v(-5.9, -103.28) * mm, "end": v(-6.04, -103.7) * mm});
            skLineSegment(sketch, "E369", {"start": v(-6.04, -103.7) * mm, "end": v(-6.32, -104.56) * mm});
            skLineSegment(sketch, "E370", {"start": v(-6.32, -104.56) * mm, "end": v(-6.47, -104.98) * mm});
            skLineSegment(sketch, "E371", {"start": v(-6.47, -104.98) * mm, "end": v(-7.6, -105) * mm});
            skLineSegment(sketch, "E372", {"start": v(-7.6, -105) * mm, "end": v(-7.77, -104.58) * mm});
            skLineSegment(sketch, "E373", {"start": v(-7.77, -104.58) * mm, "end": v(-8.08, -103.75) * mm});
            skLineSegment(sketch, "E374", {"start": v(-8.08, -103.75) * mm, "end": v(-8.23, -103.33) * mm});
            skLineSegment(sketch, "E375", {"start": v(-8.23, -103.33) * mm, "end": v(-9.38, -103.33) * mm});
            skLineSegment(sketch, "E376", {"start": v(-9.38, -103.33) * mm, "end": v(-9.52, -103.75) * mm});
            skLineSegment(sketch, "E377", {"start": v(-9.52, -103.75) * mm, "end": v(-9.84, -104.59) * mm});
            skLineSegment(sketch, "E378", {"start": v(-9.84, -104.59) * mm, "end": v(-10, -105) * mm});
            skLineSegment(sketch, "E379", {"start": v(-10, -105) * mm, "end": v(-11.13, -104.99) * mm});
            skLineSegment(sketch, "E380", {"start": v(-11.13, -104.99) * mm, "end": v(-11.28, -104.56) * mm});
            skLineSegment(sketch, "E381", {"start": v(-11.28, -104.56) * mm, "end": v(-11.57, -103.72) * mm});
            skLineSegment(sketch, "E382", {"start": v(-11.57, -103.72) * mm, "end": v(-11.7, -103.3) * mm});
            skLineSegment(sketch, "E383", {"start": v(-11.7, -103.3) * mm, "end": v(-12.85, -103.26) * mm});
            skLineSegment(sketch, "E384", {"start": v(-12.85, -103.26) * mm, "end": v(-13, -103.67) * mm});
            skLineSegment(sketch, "E385", {"start": v(-13, -103.67) * mm, "end": v(-13.35, -104.5) * mm});
            skLineSegment(sketch, "E386", {"start": v(-13.35, -104.5) * mm, "end": v(-13.53, -104.91) * mm});
            skLineSegment(sketch, "E387", {"start": v(-13.53, -104.91) * mm, "end": v(-14.66, -104.86) * mm});
            skLineSegment(sketch, "E388", {"start": v(-14.66, -104.86) * mm, "end": v(-14.8, -104.43) * mm});
            skLineSegment(sketch, "E389", {"start": v(-14.8, -104.43) * mm, "end": v(-15.05, -103.57) * mm});
            skLineSegment(sketch, "E390", {"start": v(-15.05, -103.57) * mm, "end": v(-15.17, -103.14) * mm});
            skLineSegment(sketch, "E391", {"start": v(-15.17, -103.14) * mm, "end": v(-16.32, -103.07) * mm});
            skLineSegment(sketch, "E392", {"start": v(-16.32, -103.07) * mm, "end": v(-16.49, -103.48) * mm});
            skLineSegment(sketch, "E393", {"start": v(-16.49, -103.48) * mm, "end": v(-16.86, -104.3) * mm});
            skLineSegment(sketch, "E394", {"start": v(-16.86, -104.3) * mm, "end": v(-17.05, -104.7) * mm});
            skLineSegment(sketch, "E395", {"start": v(-17.05, -104.7) * mm, "end": v(-18.17, -104.6) * mm});
            skLineSegment(sketch, "E396", {"start": v(-18.17, -104.6) * mm, "end": v(-18.3, -104.17) * mm});
            skLineSegment(sketch, "E397", {"start": v(-18.3, -104.17) * mm, "end": v(-18.53, -103.3) * mm});
            skLineSegment(sketch, "E398", {"start": v(-18.53, -103.3) * mm, "end": v(-18.63, -102.88) * mm});
            skLineSegment(sketch, "E399", {"start": v(-18.63, -102.88) * mm, "end": v(-19.77, -102.76) * mm});
            skLineSegment(sketch, "E400", {"start": v(-19.77, -102.76) * mm, "end": v(-19.96, -103.17) * mm});
            skLineSegment(sketch, "E401", {"start": v(-19.96, -103.17) * mm, "end": v(-20.36, -103.97) * mm});
            skLineSegment(sketch, "E402", {"start": v(-20.36, -103.97) * mm, "end": v(-20.56, -104.37) * mm});
            skLineSegment(sketch, "E403", {"start": v(-20.56, -104.37) * mm, "end": v(-21.68, -104.24) * mm});
            skLineSegment(sketch, "E404", {"start": v(-21.68, -104.24) * mm, "end": v(-21.8, -103.8) * mm});
            skLineSegment(sketch, "E405", {"start": v(-21.8, -103.8) * mm, "end": v(-22, -102.93) * mm});
            skLineSegment(sketch, "E406", {"start": v(-22, -102.93) * mm, "end": v(-22.08, -102.5) * mm});
            skLineSegment(sketch, "E407", {"start": v(-22.08, -102.5) * mm, "end": v(-23.22, -102.34) * mm});
            skLineSegment(sketch, "E408", {"start": v(-23.22, -102.34) * mm, "end": v(-23.42, -102.74) * mm});
            skLineSegment(sketch, "E409", {"start": v(-23.42, -102.74) * mm, "end": v(-23.84, -103.53) * mm});
            skLineSegment(sketch, "E410", {"start": v(-23.84, -103.53) * mm, "end": v(-24.06, -103.92) * mm});
            skLineSegment(sketch, "E411", {"start": v(-24.06, -103.92) * mm, "end": v(-25.18, -103.75) * mm});
            skLineSegment(sketch, "E412", {"start": v(-25.18, -103.75) * mm, "end": v(-25.27, -103.31) * mm});
            skLineSegment(sketch, "E413", {"start": v(-25.27, -103.31) * mm, "end": v(-25.44, -102.43) * mm});
            skLineSegment(sketch, "E414", {"start": v(-25.44, -102.43) * mm, "end": v(-25.52, -102) * mm});
            skLineSegment(sketch, "E415", {"start": v(-25.52, -102) * mm, "end": v(-26.65, -101.8) * mm});
            skLineSegment(sketch, "E416", {"start": v(-26.65, -101.8) * mm, "end": v(-26.86, -102.2) * mm});
            skLineSegment(sketch, "E417", {"start": v(-26.86, -102.2) * mm, "end": v(-27.31, -102.97) * mm});
            skLineSegment(sketch, "E418", {"start": v(-27.31, -102.97) * mm, "end": v(-27.54, -103.35) * mm});
            skLineSegment(sketch, "E419", {"start": v(-27.54, -103.35) * mm, "end": v(-28.65, -103.15) * mm});
            skLineSegment(sketch, "E420", {"start": v(-28.65, -103.15) * mm, "end": v(-28.73, -102.7) * mm});
            skLineSegment(sketch, "E421", {"start": v(-28.73, -102.7) * mm, "end": v(-28.87, -101.82) * mm});
            skLineSegment(sketch, "E422", {"start": v(-28.87, -101.82) * mm, "end": v(-28.93, -101.38) * mm});
            skLineSegment(sketch, "E423", {"start": v(-28.93, -101.38) * mm, "end": v(-30.06, -101.16) * mm});
            skLineSegment(sketch, "E424", {"start": v(-30.06, -101.16) * mm, "end": v(-30.29, -101.54) * mm});
            skLineSegment(sketch, "E425", {"start": v(-30.29, -101.54) * mm, "end": v(-30.76, -102.3) * mm});
            skLineSegment(sketch, "E426", {"start": v(-30.76, -102.3) * mm, "end": v(-31, -102.67) * mm});
            skLineSegment(sketch, "E427", {"start": v(-31, -102.67) * mm, "end": v(-32.1, -102.43) * mm});
            skLineSegment(sketch, "E428", {"start": v(-32.1, -102.43) * mm, "end": v(-32.17, -101.98) * mm});
            skLineSegment(sketch, "E429", {"start": v(-32.17, -101.98) * mm, "end": v(-32.28, -101.1) * mm});
            skLineSegment(sketch, "E430", {"start": v(-32.28, -101.1) * mm, "end": v(-32.33, -100.66) * mm});
            skLineSegment(sketch, "E431", {"start": v(-32.33, -100.66) * mm, "end": v(-33.45, -100.4) * mm});
            skLineSegment(sketch, "E432", {"start": v(-33.45, -100.4) * mm, "end": v(-33.69, -100.76) * mm});
            skLineSegment(sketch, "E433", {"start": v(-33.69, -100.76) * mm, "end": v(-34.18, -101.5) * mm});
            skLineSegment(sketch, "E434", {"start": v(-34.18, -101.5) * mm, "end": v(-34.44, -101.87) * mm});
            skLineSegment(sketch, "E435", {"start": v(-34.44, -101.87) * mm, "end": v(-35.54, -101.6) * mm});
            skLineSegment(sketch, "E436", {"start": v(-35.54, -101.6) * mm, "end": v(-35.58, -101.15) * mm});
            skLineSegment(sketch, "E437", {"start": v(-35.58, -101.15) * mm, "end": v(-35.66, -100.26) * mm});
            skLineSegment(sketch, "E438", {"start": v(-35.66, -100.26) * mm, "end": v(-35.7, -99.81) * mm});
            skLineSegment(sketch, "E439", {"start": v(-35.7, -99.81) * mm, "end": v(-36.8, -99.51) * mm});
            skLineSegment(sketch, "E440", {"start": v(-36.8, -99.51) * mm, "end": v(-37.06, -99.88) * mm});
            skLineSegment(sketch, "E441", {"start": v(-37.06, -99.88) * mm, "end": v(-37.58, -100.6) * mm});
            skLineSegment(sketch, "E442", {"start": v(-37.58, -100.6) * mm, "end": v(-37.85, -100.96) * mm});
            skLineSegment(sketch, "E443", {"start": v(-37.85, -100.96) * mm, "end": v(-38.93, -100.65) * mm});
            skLineSegment(sketch, "E444", {"start": v(-38.93, -100.65) * mm, "end": v(-38.97, -100.2) * mm});
            skLineSegment(sketch, "E445", {"start": v(-38.97, -100.2) * mm, "end": v(-39.02, -99.3) * mm});
            skLineSegment(sketch, "E446", {"start": v(-39.02, -99.3) * mm, "end": v(-39.03, -98.86) * mm});
            skLineSegment(sketch, "E447", {"start": v(-39.03, -98.86) * mm, "end": v(-40.13, -98.52) * mm});
            skLineSegment(sketch, "E448", {"start": v(-40.13, -98.52) * mm, "end": v(-40.4, -98.88) * mm});
            skLineSegment(sketch, "E449", {"start": v(-40.4, -98.88) * mm, "end": v(-40.94, -99.58) * mm});
            skLineSegment(sketch, "E450", {"start": v(-40.94, -99.58) * mm, "end": v(-41.22, -99.93) * mm});
            skLineSegment(sketch, "E451", {"start": v(-41.22, -99.93) * mm, "end": v(-42.3, -99.58) * mm});
            skLineSegment(sketch, "E452", {"start": v(-42.3, -99.58) * mm, "end": v(-42.32, -99.13) * mm});
            skLineSegment(sketch, "E453", {"start": v(-42.32, -99.13) * mm, "end": v(-42.34, -98.24) * mm});
            skLineSegment(sketch, "E454", {"start": v(-42.34, -98.24) * mm, "end": v(-42.34, -97.8) * mm});
            skLineSegment(sketch, "E455", {"start": v(-42.34, -97.8) * mm, "end": v(-43.42, -97.42) * mm});
            skLineSegment(sketch, "E456", {"start": v(-43.42, -97.42) * mm, "end": v(-43.7, -97.77) * mm});
            skLineSegment(sketch, "E457", {"start": v(-43.7, -97.77) * mm, "end": v(-44.27, -98.45) * mm});
            skLineSegment(sketch, "E458", {"start": v(-44.27, -98.45) * mm, "end": v(-44.56, -98.8) * mm});
            skLineSegment(sketch, "E459", {"start": v(-44.56, -98.8) * mm, "end": v(-45.62, -98.4) * mm});
            skLineSegment(sketch, "E460", {"start": v(-45.62, -98.4) * mm, "end": v(-45.63, -97.96) * mm});
            skLineSegment(sketch, "E461", {"start": v(-45.63, -97.96) * mm, "end": v(-45.62, -97.06) * mm});
            skLineSegment(sketch, "E462", {"start": v(-45.62, -97.06) * mm, "end": v(-45.6, -96.62) * mm});
            skLineSegment(sketch, "E463", {"start": v(-45.6, -96.62) * mm, "end": v(-46.68, -96.2) * mm});
            skLineSegment(sketch, "E464", {"start": v(-46.68, -96.2) * mm, "end": v(-46.96, -96.54) * mm});
            skLineSegment(sketch, "E465", {"start": v(-46.96, -96.54) * mm, "end": v(-47.56, -97.21) * mm});
            skLineSegment(sketch, "E466", {"start": v(-47.56, -97.21) * mm, "end": v(-47.86, -97.54) * mm});
            skLineSegment(sketch, "E467", {"start": v(-47.86, -97.54) * mm, "end": v(-48.9, -97.12) * mm});
            skLineSegment(sketch, "E468", {"start": v(-48.9, -97.12) * mm, "end": v(-48.9, -96.67) * mm});
            skLineSegment(sketch, "E469", {"start": v(-48.9, -96.67) * mm, "end": v(-48.86, -95.78) * mm});
            skLineSegment(sketch, "E470", {"start": v(-48.86, -95.78) * mm, "end": v(-48.83, -95.33) * mm});
            skLineSegment(sketch, "E471", {"start": v(-48.83, -95.33) * mm, "end": v(-49.89, -94.89) * mm});
            skLineSegment(sketch, "E472", {"start": v(-49.89, -94.89) * mm, "end": v(-50.19, -95.21) * mm});
            skLineSegment(sketch, "E473", {"start": v(-50.19, -95.21) * mm, "end": v(-50.8, -95.86) * mm});
            skLineSegment(sketch, "E474", {"start": v(-50.8, -95.86) * mm, "end": v(-51.12, -96.18) * mm});
            skLineSegment(sketch, "E475", {"start": v(-51.12, -96.18) * mm, "end": v(-52.15, -95.72) * mm});
            skLineSegment(sketch, "E476", {"start": v(-52.15, -95.72) * mm, "end": v(-52.12, -95.27) * mm});
            skLineSegment(sketch, "E477", {"start": v(-52.12, -95.27) * mm, "end": v(-52.05, -94.38) * mm});
            skLineSegment(sketch, "E478", {"start": v(-52.05, -94.38) * mm, "end": v(-52, -93.94) * mm});
            skLineSegment(sketch, "E479", {"start": v(-52, -93.94) * mm, "end": v(-53.05, -93.46) * mm});
            skLineSegment(sketch, "E480", {"start": v(-53.05, -93.46) * mm, "end": v(-53.36, -93.78) * mm});
            skLineSegment(sketch, "E481", {"start": v(-53.36, -93.78) * mm, "end": v(-54, -94.4) * mm});
            skLineSegment(sketch, "E482", {"start": v(-54, -94.4) * mm, "end": v(-54.32, -94.71) * mm});
            skLineSegment(sketch, "E483", {"start": v(-54.32, -94.71) * mm, "end": v(-55.34, -94.22) * mm});
            skLineSegment(sketch, "E484", {"start": v(-55.34, -94.22) * mm, "end": v(-55.3, -93.77) * mm});
            skLineSegment(sketch, "E485", {"start": v(-55.3, -93.77) * mm, "end": v(-55.2, -92.88) * mm});
            skLineSegment(sketch, "E486", {"start": v(-55.2, -92.88) * mm, "end": v(-55.14, -92.44) * mm});
            skLineSegment(sketch, "E487", {"start": v(-55.14, -92.44) * mm, "end": v(-56.17, -91.92) * mm});
            skLineSegment(sketch, "E488", {"start": v(-56.17, -91.92) * mm, "end": v(-56.49, -92.23) * mm});
            skLineSegment(sketch, "E489", {"start": v(-56.49, -92.23) * mm, "end": v(-57.14, -92.84) * mm});
            skLineSegment(sketch, "E490", {"start": v(-57.14, -92.84) * mm, "end": v(-57.48, -93.14) * mm});
            skLineSegment(sketch, "E491", {"start": v(-57.48, -93.14) * mm, "end": v(-58.48, -92.6) * mm});
            skLineSegment(sketch, "E492", {"start": v(-58.48, -92.6) * mm, "end": v(-58.42, -92.16) * mm});
            skLineSegment(sketch, "E493", {"start": v(-58.42, -92.16) * mm, "end": v(-58.3, -91.28) * mm});
            skLineSegment(sketch, "E494", {"start": v(-58.3, -91.28) * mm, "end": v(-58.22, -90.84) * mm});
            skLineSegment(sketch, "E495", {"start": v(-58.22, -90.84) * mm, "end": v(-59.23, -90.29) * mm});
            skLineSegment(sketch, "E496", {"start": v(-59.23, -90.29) * mm, "end": v(-59.56, -90.58) * mm});
            skLineSegment(sketch, "E497", {"start": v(-59.56, -90.58) * mm, "end": v(-60.24, -91.17) * mm});
            skLineSegment(sketch, "E498", {"start": v(-60.24, -91.17) * mm, "end": v(-60.58, -91.45) * mm});
            skLineSegment(sketch, "E499", {"start": v(-60.58, -91.45) * mm, "end": v(-61.56, -90.9) * mm});
            skLineSegment(sketch, "E500", {"start": v(-61.56, -90.9) * mm, "end": v(-61.5, -90.45) * mm});
            skLineSegment(sketch, "E501", {"start": v(-61.5, -90.45) * mm, "end": v(-61.33, -89.57) * mm});
            skLineSegment(sketch, "E502", {"start": v(-61.33, -89.57) * mm, "end": v(-61.24, -89.13) * mm});
            skLineSegment(sketch, "E503", {"start": v(-61.24, -89.13) * mm, "end": v(-62.23, -88.55) * mm});
            skLineSegment(sketch, "E504", {"start": v(-62.23, -88.55) * mm, "end": v(-62.57, -88.83) * mm});
            skLineSegment(sketch, "E505", {"start": v(-62.57, -88.83) * mm, "end": v(-63.27, -89.4) * mm});
            skLineSegment(sketch, "E506", {"start": v(-63.27, -89.4) * mm, "end": v(-63.62, -89.67) * mm});
            skLineSegment(sketch, "E507", {"start": v(-63.62, -89.67) * mm, "end": v(-64.59, -89.08) * mm});
            skLineSegment(sketch, "E508", {"start": v(-64.59, -89.08) * mm, "end": v(-64.5, -88.63) * mm});
            skLineSegment(sketch, "E509", {"start": v(-64.5, -88.63) * mm, "end": v(-64.31, -87.76) * mm});
            skLineSegment(sketch, "E510", {"start": v(-64.31, -87.76) * mm, "end": v(-64.2, -87.33) * mm});
            skLineSegment(sketch, "E511", {"start": v(-64.2, -87.33) * mm, "end": v(-65.18, -86.7) * mm});
            skLineSegment(sketch, "E512", {"start": v(-65.18, -86.7) * mm, "end": v(-65.53, -86.98) * mm});
            skLineSegment(sketch, "E513", {"start": v(-65.53, -86.98) * mm, "end": v(-66.24, -87.52) * mm});
            skLineSegment(sketch, "E514", {"start": v(-66.24, -87.52) * mm, "end": v(-66.6, -87.78) * mm});
            skLineSegment(sketch, "E515", {"start": v(-66.6, -87.78) * mm, "end": v(-67.55, -87.16) * mm});
            skLineSegment(sketch, "E516", {"start": v(-67.55, -87.16) * mm, "end": v(-67.45, -86.72) * mm});
            skLineSegment(sketch, "E517", {"start": v(-67.45, -86.72) * mm, "end": v(-67.23, -85.85) * mm});
            skLineSegment(sketch, "E518", {"start": v(-67.23, -85.85) * mm, "end": v(-67.11, -85.42) * mm});
            skLineSegment(sketch, "E519", {"start": v(-67.11, -85.42) * mm, "end": v(-68.06, -84.77) * mm});
            skLineSegment(sketch, "E520", {"start": v(-68.06, -84.77) * mm, "end": v(-68.42, -85.03) * mm});
            skLineSegment(sketch, "E521", {"start": v(-68.42, -85.03) * mm, "end": v(-69.15, -85.55) * mm});
            skLineSegment(sketch, "E522", {"start": v(-69.15, -85.55) * mm, "end": v(-69.52, -85.8) * mm});
            skLineSegment(sketch, "E523", {"start": v(-69.52, -85.8) * mm, "end": v(-70.44, -85.14) * mm});
            skLineSegment(sketch, "E524", {"start": v(-70.44, -85.14) * mm, "end": v(-70.33, -84.7) * mm});
            skLineSegment(sketch, "E525", {"start": v(-70.33, -84.7) * mm, "end": v(-70.08, -83.85) * mm});
            skLineSegment(sketch, "E526", {"start": v(-70.08, -83.85) * mm, "end": v(-69.95, -83.42) * mm});
            skLineSegment(sketch, "E527", {"start": v(-69.95, -83.42) * mm, "end": v(-70.87, -82.74) * mm});
            skLineSegment(sketch, "E528", {"start": v(-70.87, -82.74) * mm, "end": v(-71.24, -82.99) * mm});
            skLineSegment(sketch, "E529", {"start": v(-71.24, -82.99) * mm, "end": v(-71.99, -83.48) * mm});
            skLineSegment(sketch, "E530", {"start": v(-71.99, -83.48) * mm, "end": v(-72.37, -83.71) * mm});
            skLineSegment(sketch, "E531", {"start": v(-72.37, -83.71) * mm, "end": v(-73.27, -83.03) * mm});
            skLineSegment(sketch, "E532", {"start": v(-73.27, -83.03) * mm, "end": v(-73.14, -82.6) * mm});
            skLineSegment(sketch, "E533", {"start": v(-73.14, -82.6) * mm, "end": v(-72.86, -81.75) * mm});
            skLineSegment(sketch, "E534", {"start": v(-72.86, -81.75) * mm, "end": v(-72.72, -81.33) * mm});
            skLineSegment(sketch, "E535", {"start": v(-72.72, -81.33) * mm, "end": v(-73.62, -80.61) * mm});
            skLineSegment(sketch, "E536", {"start": v(-73.62, -80.61) * mm, "end": v(-74, -80.85) * mm});
            skLineSegment(sketch, "E537", {"start": v(-74, -80.85) * mm, "end": v(-74.76, -81.31) * mm});
            skLineSegment(sketch, "E538", {"start": v(-74.76, -81.31) * mm, "end": v(-75.15, -81.54) * mm});
            skLineSegment(sketch, "E539", {"start": v(-75.15, -81.54) * mm, "end": v(-76.02, -80.82) * mm});
            skLineSegment(sketch, "E540", {"start": v(-76.02, -80.82) * mm, "end": v(-75.87, -80.4) * mm});
            skLineSegment(sketch, "E541", {"start": v(-75.87, -80.4) * mm, "end": v(-75.57, -79.55) * mm});
            skLineSegment(sketch, "E542", {"start": v(-75.57, -79.55) * mm, "end": v(-75.41, -79.14) * mm});
            skLineSegment(sketch, "E543", {"start": v(-75.41, -79.14) * mm, "end": v(-76.29, -78.4) * mm});
            skLineSegment(sketch, "E544", {"start": v(-76.29, -78.4) * mm, "end": v(-76.67, -78.62) * mm});
            skLineSegment(sketch, "E545", {"start": v(-76.67, -78.62) * mm, "end": v(-77.45, -79.06) * mm});
            skLineSegment(sketch, "E546", {"start": v(-77.45, -79.06) * mm, "end": v(-77.85, -79.27) * mm});
            skLineSegment(sketch, "E547", {"start": v(-77.85, -79.27) * mm, "end": v(-78.7, -78.52) * mm});
            skLineSegment(sketch, "E548", {"start": v(-78.7, -78.52) * mm, "end": v(-78.54, -78.1) * mm});
            skLineSegment(sketch, "E549", {"start": v(-78.54, -78.1) * mm, "end": v(-78.2, -77.27) * mm});
            skLineSegment(sketch, "E550", {"start": v(-78.2, -77.27) * mm, "end": v(-78.03, -76.86) * mm});
            skLineSegment(sketch, "E551", {"start": v(-78.03, -76.86) * mm, "end": v(-78.88, -76.1) * mm});
            skLineSegment(sketch, "E552", {"start": v(-78.88, -76.1) * mm, "end": v(-79.27, -76.3) * mm});
            skLineSegment(sketch, "E553", {"start": v(-79.27, -76.3) * mm, "end": v(-80.07, -76.71) * mm});
            skLineSegment(sketch, "E554", {"start": v(-80.07, -76.71) * mm, "end": v(-80.47, -76.91) * mm});
            skLineSegment(sketch, "E555", {"start": v(-80.47, -76.91) * mm, "end": v(-81.3, -76.14) * mm});
            skLineSegment(sketch, "E556", {"start": v(-81.3, -76.14) * mm, "end": v(-81.12, -75.72) * mm});
            skLineSegment(sketch, "E557", {"start": v(-81.12, -75.72) * mm, "end": v(-80.76, -74.9) * mm});
            skLineSegment(sketch, "E558", {"start": v(-80.76, -74.9) * mm, "end": v(-80.58, -74.5) * mm});
            skLineSegment(sketch, "E559", {"start": v(-80.58, -74.5) * mm, "end": v(-81.4, -73.7) * mm});
            skLineSegment(sketch, "E560", {"start": v(-81.4, -73.7) * mm, "end": v(-81.8, -73.9) * mm});
            skLineSegment(sketch, "E561", {"start": v(-81.8, -73.9) * mm, "end": v(-82.6, -74.28) * mm});
            skLineSegment(sketch, "E562", {"start": v(-82.6, -74.28) * mm, "end": v(-83.02, -74.46) * mm});
            skLineSegment(sketch, "E563", {"start": v(-83.02, -74.46) * mm, "end": v(-83.81, -73.66) * mm});
            skLineSegment(sketch, "E564", {"start": v(-83.81, -73.66) * mm, "end": v(-83.63, -73.26) * mm});
            skLineSegment(sketch, "E565", {"start": v(-83.63, -73.26) * mm, "end": v(-83.24, -72.45) * mm});
            skLineSegment(sketch, "E566", {"start": v(-83.24, -72.45) * mm, "end": v(-83.04, -72.05) * mm});
            skLineSegment(sketch, "E567", {"start": v(-83.04, -72.05) * mm, "end": v(-83.84, -71.23) * mm});
            skLineSegment(sketch, "E568", {"start": v(-83.84, -71.23) * mm, "end": v(-84.24, -71.4) * mm});
            skLineSegment(sketch, "E569", {"start": v(-84.24, -71.4) * mm, "end": v(-85.06, -71.76) * mm});
            skLineSegment(sketch, "E570", {"start": v(-85.06, -71.76) * mm, "end": v(-85.48, -71.94) * mm});
            skLineSegment(sketch, "E571", {"start": v(-85.48, -71.94) * mm, "end": v(-86.24, -71.1) * mm});
            skLineSegment(sketch, "E572", {"start": v(-86.24, -71.1) * mm, "end": v(-86.04, -70.7) * mm});
            skLineSegment(sketch, "E573", {"start": v(-86.04, -70.7) * mm, "end": v(-85.63, -69.91) * mm});
            skLineSegment(sketch, "E574", {"start": v(-85.63, -69.91) * mm, "end": v(-85.42, -69.52) * mm});
            skLineSegment(sketch, "E575", {"start": v(-85.42, -69.52) * mm, "end": v(-86.19, -68.67) * mm});
            skLineSegment(sketch, "E576", {"start": v(-86.19, -68.67) * mm, "end": v(-86.6, -68.84) * mm});
            skLineSegment(sketch, "E577", {"start": v(-86.6, -68.84) * mm, "end": v(-87.43, -69.17) * mm});
            skLineSegment(sketch, "E578", {"start": v(-87.43, -69.17) * mm, "end": v(-87.85, -69.33) * mm});
            skLineSegment(sketch, "E579", {"start": v(-87.85, -69.33) * mm, "end": v(-88.59, -68.47) * mm});
            skLineSegment(sketch, "E580", {"start": v(-88.59, -68.47) * mm, "end": v(-88.38, -68.08) * mm});
            skLineSegment(sketch, "E581", {"start": v(-88.38, -68.08) * mm, "end": v(-87.94, -67.3) * mm});
            skLineSegment(sketch, "E582", {"start": v(-87.94, -67.3) * mm, "end": v(-87.71, -66.92) * mm});
            skLineSegment(sketch, "E583", {"start": v(-87.71, -66.92) * mm, "end": v(-88.45, -66.04) * mm});
            skLineSegment(sketch, "E584", {"start": v(-88.45, -66.04) * mm, "end": v(-88.86, -66.2) * mm});
            skLineSegment(sketch, "E585", {"start": v(-88.86, -66.2) * mm, "end": v(-89.7, -66.5) * mm});
            skLineSegment(sketch, "E586", {"start": v(-89.7, -66.5) * mm, "end": v(-90.13, -66.64) * mm});
            skLineSegment(sketch, "E587", {"start": v(-90.13, -66.64) * mm, "end": v(-90.84, -65.76) * mm});
            skLineSegment(sketch, "E588", {"start": v(-90.84, -65.76) * mm, "end": v(-90.62, -65.37) * mm});
            skLineSegment(sketch, "E589", {"start": v(-90.62, -65.37) * mm, "end": v(-90.15, -64.6) * mm});
            skLineSegment(sketch, "E590", {"start": v(-90.15, -64.6) * mm, "end": v(-89.91, -64.23) * mm});
            skLineSegment(sketch, "E591", {"start": v(-89.91, -64.23) * mm, "end": v(-90.62, -63.33) * mm});
            skLineSegment(sketch, "E592", {"start": v(-90.62, -63.33) * mm, "end": v(-91.04, -63.47) * mm});
            skLineSegment(sketch, "E593", {"start": v(-91.04, -63.47) * mm, "end": v(-91.9, -63.74) * mm});
            skLineSegment(sketch, "E594", {"start": v(-91.9, -63.74) * mm, "end": v(-92.33, -63.87) * mm});
            skLineSegment(sketch, "E595", {"start": v(-92.33, -63.87) * mm, "end": v(-93, -62.97) * mm});
            skLineSegment(sketch, "E596", {"start": v(-93, -62.97) * mm, "end": v(-92.77, -62.6) * mm});
            skLineSegment(sketch, "E597", {"start": v(-92.77, -62.6) * mm, "end": v(-92.28, -61.85) * mm});
            skLineSegment(sketch, "E598", {"start": v(-92.28, -61.85) * mm, "end": v(-92.03, -61.48) * mm});
            skLineSegment(sketch, "E599", {"start": v(-92.03, -61.48) * mm, "end": v(-92.7, -60.55) * mm});
            skLineSegment(sketch, "E600", {"start": v(-92.7, -60.55) * mm, "end": v(-93.13, -60.68) * mm});
            skLineSegment(sketch, "E601", {"start": v(-93.13, -60.68) * mm, "end": v(-93.99, -60.92) * mm});
            skLineSegment(sketch, "E602", {"start": v(-93.99, -60.92) * mm, "end": v(-94.42, -61.04) * mm});
            skLineSegment(sketch, "E603", {"start": v(-94.42, -61.04) * mm, "end": v(-95.08, -60.11) * mm});
            skLineSegment(sketch, "E604", {"start": v(-95.08, -60.11) * mm, "end": v(-94.82, -59.74) * mm});
            skLineSegment(sketch, "E605", {"start": v(-94.82, -59.74) * mm, "end": v(-94.3, -59.01) * mm});
            skLineSegment(sketch, "E606", {"start": v(-94.3, -59.01) * mm, "end": v(-94.04, -58.65) * mm});
            skLineSegment(sketch, "E607", {"start": v(-94.04, -58.65) * mm, "end": v(-94.7, -57.7) * mm});
            skLineSegment(sketch, "E608", {"start": v(-94.7, -57.7) * mm, "end": v(-95.12, -57.82) * mm});
            skLineSegment(sketch, "E609", {"start": v(-95.12, -57.82) * mm, "end": v(-95.99, -58.03) * mm});
            skLineSegment(sketch, "E610", {"start": v(-95.99, -58.03) * mm, "end": v(-96.43, -58.13) * mm});
            skLineSegment(sketch, "E611", {"start": v(-96.43, -58.13) * mm, "end": v(-97.05, -57.19) * mm});
            skLineSegment(sketch, "E612", {"start": v(-97.05, -57.19) * mm, "end": v(-96.78, -56.82) * mm});
            skLineSegment(sketch, "E613", {"start": v(-96.78, -56.82) * mm, "end": v(-96.24, -56.11) * mm});
            skLineSegment(sketch, "E614", {"start": v(-96.24, -56.11) * mm, "end": v(-95.97, -55.76) * mm});
            skLineSegment(sketch, "E615", {"start": v(-95.97, -55.76) * mm, "end": v(-96.58, -54.8) * mm});
            skLineSegment(sketch, "E616", {"start": v(-96.58, -54.8) * mm, "end": v(-97.01, -54.9) * mm});
            skLineSegment(sketch, "E617", {"start": v(-97.01, -54.9) * mm, "end": v(-97.89, -55.08) * mm});
            skLineSegment(sketch, "E618", {"start": v(-97.89, -55.08) * mm, "end": v(-98.33, -55.16) * mm});
            skLineSegment(sketch, "E619", {"start": v(-98.33, -55.16) * mm, "end": v(-98.92, -54.2) * mm});
            skLineSegment(sketch, "E620", {"start": v(-98.92, -54.2) * mm, "end": v(-98.64, -53.84) * mm});
            skLineSegment(sketch, "E621", {"start": v(-98.64, -53.84) * mm, "end": v(-98.08, -53.15) * mm});
            skLineSegment(sketch, "E622", {"start": v(-98.08, -53.15) * mm, "end": v(-97.8, -52.81) * mm});
            skLineSegment(sketch, "E623", {"start": v(-97.8, -52.81) * mm, "end": v(-98.37, -51.82) * mm});
            skLineSegment(sketch, "E624", {"start": v(-98.37, -51.82) * mm, "end": v(-98.8, -51.9) * mm});
            skLineSegment(sketch, "E625", {"start": v(-98.8, -51.9) * mm, "end": v(-99.69, -52.06) * mm});
            skLineSegment(sketch, "E626", {"start": v(-99.69, -52.06) * mm, "end": v(-100.13, -52.13) * mm});
            skLineSegment(sketch, "E627", {"start": v(-100.13, -52.13) * mm, "end": v(-100.69, -51.14) * mm});
            skLineSegment(sketch, "E628", {"start": v(-100.69, -51.14) * mm, "end": v(-100.4, -50.8) * mm});
            skLineSegment(sketch, "E629", {"start": v(-100.4, -50.8) * mm, "end": v(-99.81, -50.13) * mm});
            skLineSegment(sketch, "E630", {"start": v(-99.81, -50.13) * mm, "end": v(-99.51, -49.8) * mm});
            skLineSegment(sketch, "E631", {"start": v(-99.51, -49.8) * mm, "end": v(-100.06, -48.79) * mm});
            skLineSegment(sketch, "E632", {"start": v(-100.06, -48.79) * mm, "end": v(-100.5, -48.86) * mm});
            skLineSegment(sketch, "E633", {"start": v(-100.5, -48.86) * mm, "end": v(-101.39, -48.98) * mm});
            skLineSegment(sketch, "E634", {"start": v(-101.39, -48.98) * mm, "end": v(-101.83, -49.04) * mm});
            skLineSegment(sketch, "E635", {"start": v(-101.83, -49.04) * mm, "end": v(-102.35, -48.03) * mm});
            skLineSegment(sketch, "E636", {"start": v(-102.35, -48.03) * mm, "end": v(-102.05, -47.7) * mm});
            skLineSegment(sketch, "E637", {"start": v(-102.05, -47.7) * mm, "end": v(-101.44, -47.05) * mm});
            skLineSegment(sketch, "E638", {"start": v(-101.44, -47.05) * mm, "end": v(-101.14, -46.73) * mm});
            skLineSegment(sketch, "E639", {"start": v(-101.14, -46.73) * mm, "end": v(-101.65, -45.7) * mm});
            skLineSegment(sketch, "E640", {"start": v(-101.65, -45.7) * mm, "end": v(-102.1, -45.76) * mm});
            skLineSegment(sketch, "E641", {"start": v(-102.1, -45.76) * mm, "end": v(-102.98, -45.85) * mm});
            skLineSegment(sketch, "E642", {"start": v(-102.98, -45.85) * mm, "end": v(-103.43, -45.89) * mm});
            skLineSegment(sketch, "E643", {"start": v(-103.43, -45.89) * mm, "end": v(-103.91, -44.87) * mm});
            skLineSegment(sketch, "E644", {"start": v(-103.91, -44.87) * mm, "end": v(-103.6, -44.55) * mm});
            skLineSegment(sketch, "E645", {"start": v(-103.6, -44.55) * mm, "end": v(-102.97, -43.91) * mm});
            skLineSegment(sketch, "E646", {"start": v(-102.97, -43.91) * mm, "end": v(-102.65, -43.6) * mm});
            skLineSegment(sketch, "E647", {"start": v(-102.65, -43.6) * mm, "end": v(-103.13, -42.56) * mm});
            skLineSegment(sketch, "E648", {"start": v(-103.13, -42.56) * mm, "end": v(-103.57, -42.6) * mm});
            skLineSegment(sketch, "E649", {"start": v(-103.57, -42.6) * mm, "end": v(-104.47, -42.67) * mm});
            skLineSegment(sketch, "E650", {"start": v(-104.47, -42.67) * mm, "end": v(-104.91, -42.7) * mm});
            skLineSegment(sketch, "E651", {"start": v(-104.91, -42.7) * mm, "end": v(-105.37, -41.66) * mm});
            skLineSegment(sketch, "E652", {"start": v(-105.37, -41.66) * mm, "end": v(-105.05, -41.34) * mm});
            skLineSegment(sketch, "E653", {"start": v(-105.05, -41.34) * mm, "end": v(-104.4, -40.73) * mm});
            skLineSegment(sketch, "E654", {"start": v(-104.4, -40.73) * mm, "end": v(-104.07, -40.43) * mm});
            skLineSegment(sketch, "E655", {"start": v(-104.07, -40.43) * mm, "end": v(-104.5, -39.37) * mm});
            skLineSegment(sketch, "E656", {"start": v(-104.5, -39.37) * mm, "end": v(-104.95, -39.4) * mm});
            skLineSegment(sketch, "E657", {"start": v(-104.95, -39.4) * mm, "end": v(-105.85, -39.43) * mm});
            skLineSegment(sketch, "E658", {"start": v(-105.85, -39.43) * mm, "end": v(-106.3, -39.44) * mm});
            skLineSegment(sketch, "E659", {"start": v(-106.3, -39.44) * mm, "end": v(-106.71, -38.4) * mm});
            skLineSegment(sketch, "E660", {"start": v(-106.71, -38.4) * mm, "end": v(-106.38, -38.1) * mm});
            skLineSegment(sketch, "E661", {"start": v(-106.38, -38.1) * mm, "end": v(-105.7, -37.5) * mm});
            skLineSegment(sketch, "E662", {"start": v(-105.7, -37.5) * mm, "end": v(-105.37, -37.22) * mm});
            skLineSegment(sketch, "E663", {"start": v(-105.37, -37.22) * mm, "end": v(-105.78, -36.14) * mm});
            skLineSegment(sketch, "E664", {"start": v(-105.78, -36.14) * mm, "end": v(-106.22, -36.15) * mm});
            skLineSegment(sketch, "E665", {"start": v(-106.22, -36.15) * mm, "end": v(-107.12, -36.16) * mm});
            skLineSegment(sketch, "E666", {"start": v(-107.12, -36.16) * mm, "end": v(-107.56, -36.15) * mm});
            skLineSegment(sketch, "E667", {"start": v(-107.56, -36.15) * mm, "end": v(-107.95, -35.09) * mm});
            skLineSegment(sketch, "E668", {"start": v(-107.95, -35.09) * mm, "end": v(-107.6, -34.8) * mm});
            skLineSegment(sketch, "E669", {"start": v(-107.6, -34.8) * mm, "end": v(-106.91, -34.23) * mm});
            skLineSegment(sketch, "E670", {"start": v(-106.91, -34.23) * mm, "end": v(-106.57, -33.96) * mm});
            skLineSegment(sketch, "E671", {"start": v(-106.57, -33.96) * mm, "end": v(-106.94, -32.87) * mm});
            skLineSegment(sketch, "E672", {"start": v(-106.94, -32.87) * mm, "end": v(-107.38, -32.87) * mm});
            skLineSegment(sketch, "E673", {"start": v(-107.38, -32.87) * mm, "end": v(-108.27, -32.84) * mm});
            skLineSegment(sketch, "E674", {"start": v(-108.27, -32.84) * mm, "end": v(-108.72, -32.82) * mm});
            skLineSegment(sketch, "E675", {"start": v(-108.72, -32.82) * mm, "end": v(-109.07, -31.75) * mm});
            skLineSegment(sketch, "E676", {"start": v(-109.07, -31.75) * mm, "end": v(-108.72, -31.47) * mm});
            skLineSegment(sketch, "E677", {"start": v(-108.72, -31.47) * mm, "end": v(-108, -30.92) * mm});
            skLineSegment(sketch, "E678", {"start": v(-108, -30.92) * mm, "end": v(-107.65, -30.66) * mm});
            skLineSegment(sketch, "E679", {"start": v(-107.65, -30.66) * mm, "end": v(-107.99, -29.56) * mm});
            skLineSegment(sketch, "E680", {"start": v(-107.99, -29.56) * mm, "end": v(-108.43, -29.54) * mm});
            skLineSegment(sketch, "E681", {"start": v(-108.43, -29.54) * mm, "end": v(-109.32, -29.49) * mm});
            skLineSegment(sketch, "E682", {"start": v(-109.32, -29.49) * mm, "end": v(-109.77, -29.45) * mm});
            skLineSegment(sketch, "E683", {"start": v(-109.77, -29.45) * mm, "end": v(-110.08, -28.36) * mm});
            skLineSegment(sketch, "E684", {"start": v(-110.08, -28.36) * mm, "end": v(-109.72, -28.1) * mm});
            skLineSegment(sketch, "E685", {"start": v(-109.72, -28.1) * mm, "end": v(-109, -27.58) * mm});
            skLineSegment(sketch, "E686", {"start": v(-109, -27.58) * mm, "end": v(-108.63, -27.33) * mm});
            skLineSegment(sketch, "E687", {"start": v(-108.63, -27.33) * mm, "end": v(-108.92, -26.22) * mm});
            skLineSegment(sketch, "E688", {"start": v(-108.92, -26.22) * mm, "end": v(-109.37, -26.18) * mm});
            skLineSegment(sketch, "E689", {"start": v(-109.37, -26.18) * mm, "end": v(-110.26, -26.1) * mm});
            skLineSegment(sketch, "E690", {"start": v(-110.26, -26.1) * mm, "end": v(-110.7, -26.05) * mm});
            skLineSegment(sketch, "E691", {"start": v(-110.7, -26.05) * mm, "end": v(-110.98, -24.95) * mm});
            skLineSegment(sketch, "E692", {"start": v(-110.98, -24.95) * mm, "end": v(-110.6, -24.7) * mm});
            skLineSegment(sketch, "E693", {"start": v(-110.6, -24.7) * mm, "end": v(-109.86, -24.2) * mm});
            skLineSegment(sketch, "E694", {"start": v(-109.86, -24.2) * mm, "end": v(-109.49, -23.96) * mm});
            skLineSegment(sketch, "E695", {"start": v(-109.49, -23.96) * mm, "end": v(-109.75, -22.85) * mm});
            skLineSegment(sketch, "E696", {"start": v(-109.75, -22.85) * mm, "end": v(-110.19, -22.8) * mm});
            skLineSegment(sketch, "E697", {"start": v(-110.19, -22.8) * mm, "end": v(-111.08, -22.68) * mm});
            skLineSegment(sketch, "E698", {"start": v(-111.08, -22.68) * mm, "end": v(-111.52, -22.62) * mm});
            skLineSegment(sketch, "E699", {"start": v(-111.52, -22.62) * mm, "end": v(-111.76, -21.51) * mm});
            skLineSegment(sketch, "E700", {"start": v(-111.76, -21.51) * mm, "end": v(-111.38, -21.27) * mm});
            skLineSegment(sketch, "E701", {"start": v(-111.38, -21.27) * mm, "end": v(-110.62, -20.8) * mm});
            skLineSegment(sketch, "E702", {"start": v(-110.62, -20.8) * mm, "end": v(-110.24, -20.57) * mm});
            skLineSegment(sketch, "E703", {"start": v(-110.24, -20.57) * mm, "end": v(-110.46, -19.45) * mm});
            skLineSegment(sketch, "E704", {"start": v(-110.46, -19.45) * mm, "end": v(-110.9, -19.38) * mm});
            skLineSegment(sketch, "E705", {"start": v(-110.9, -19.38) * mm, "end": v(-111.78, -19.24) * mm});
            skLineSegment(sketch, "E706", {"start": v(-111.78, -19.24) * mm, "end": v(-112.22, -19.16) * mm});
            skLineSegment(sketch, "E707", {"start": v(-112.22, -19.16) * mm, "end": v(-112.42, -18.05) * mm});
            skLineSegment(sketch, "E708", {"start": v(-112.42, -18.05) * mm, "end": v(-112.04, -17.82) * mm});
            skLineSegment(sketch, "E709", {"start": v(-112.04, -17.82) * mm, "end": v(-111.26, -17.37) * mm});
            skLineSegment(sketch, "E710", {"start": v(-111.26, -17.37) * mm, "end": v(-110.87, -17.16) * mm});
            skLineSegment(sketch, "E711", {"start": v(-110.87, -17.16) * mm, "end": v(-111.05, -16.03) * mm});
            skLineSegment(sketch, "E712", {"start": v(-111.05, -16.03) * mm, "end": v(-111.5, -15.95) * mm});
            skLineSegment(sketch, "E713", {"start": v(-111.5, -15.95) * mm, "end": v(-112.37, -15.78) * mm});
            skLineSegment(sketch, "E714", {"start": v(-112.37, -15.78) * mm, "end": v(-112.8, -15.68) * mm});
            skLineSegment(sketch, "E715", {"start": v(-112.8, -15.68) * mm, "end": v(-112.97, -14.56) * mm});
            skLineSegment(sketch, "E716", {"start": v(-112.97, -14.56) * mm, "end": v(-112.58, -14.34) * mm});
            skLineSegment(sketch, "E717", {"start": v(-112.58, -14.34) * mm, "end": v(-111.79, -13.93) * mm});
            skLineSegment(sketch, "E718", {"start": v(-111.79, -13.93) * mm, "end": v(-111.39, -13.73) * mm});
            skLineSegment(sketch, "E719", {"start": v(-111.39, -13.73) * mm, "end": v(-111.53, -12.59) * mm});
            skLineSegment(sketch, "E720", {"start": v(-111.53, -12.59) * mm, "end": v(-111.97, -12.5) * mm});
            skLineSegment(sketch, "E721", {"start": v(-111.97, -12.5) * mm, "end": v(-112.84, -12.3) * mm});
            skLineSegment(sketch, "E722", {"start": v(-112.84, -12.3) * mm, "end": v(-113.27, -12.18) * mm});
            skLineSegment(sketch, "E723", {"start": v(-113.27, -12.18) * mm, "end": v(-113.4, -11.06) * mm});
            skLineSegment(sketch, "E724", {"start": v(-113.4, -11.06) * mm, "end": v(-113, -10.86) * mm});
            skLineSegment(sketch, "E725", {"start": v(-113, -10.86) * mm, "end": v(-112.2, -10.47) * mm});
            skLineSegment(sketch, "E726", {"start": v(-112.2, -10.47) * mm, "end": v(-111.8, -10.28) * mm});
            skLineSegment(sketch, "E727", {"start": v(-111.8, -10.28) * mm, "end": v(-111.9, -9.14) * mm});
            skLineSegment(sketch, "E728", {"start": v(-111.9, -9.14) * mm, "end": v(-112.33, -9.03) * mm});
            skLineSegment(sketch, "E729", {"start": v(-112.33, -9.03) * mm, "end": v(-113.2, -8.8) * mm});
            skLineSegment(sketch, "E730", {"start": v(-113.2, -8.8) * mm, "end": v(-113.63, -8.67) * mm});
            skLineSegment(sketch, "E731", {"start": v(-113.63, -8.67) * mm, "end": v(-113.71, -7.55) * mm});
            skLineSegment(sketch, "E732", {"start": v(-113.71, -7.55) * mm, "end": v(-113.3, -7.36) * mm});
            skLineSegment(sketch, "E733", {"start": v(-113.3, -7.36) * mm, "end": v(-112.49, -7) * mm});
            skLineSegment(sketch, "E734", {"start": v(-112.49, -7) * mm, "end": v(-112.08, -6.82) * mm});
            skLineSegment(sketch, "E735", {"start": v(-112.08, -6.82) * mm, "end": v(-112.15, -5.67) * mm});
            skLineSegment(sketch, "E736", {"start": v(-112.15, -5.67) * mm, "end": v(-112.58, -5.55) * mm});
            skLineSegment(sketch, "E737", {"start": v(-112.58, -5.55) * mm, "end": v(-113.43, -5.3) * mm});
            skLineSegment(sketch, "E738", {"start": v(-113.43, -5.3) * mm, "end": v(-113.86, -5.15) * mm});
            skLineSegment(sketch, "E739", {"start": v(-113.86, -5.15) * mm, "end": v(-113.9, -4.02) * mm});
            skLineSegment(sketch, "E740", {"start": v(-113.9, -4.02) * mm, "end": v(-113.5, -3.85) * mm});
            skLineSegment(sketch, "E741", {"start": v(-113.5, -3.85) * mm, "end": v(-112.66, -3.51) * mm});
            skLineSegment(sketch, "E742", {"start": v(-112.66, -3.51) * mm, "end": v(-112.25, -3.35) * mm});
            skLineSegment(sketch, "E743", {"start": v(-112.25, -3.35) * mm, "end": v(-112.28, -2.2) * mm});
            skLineSegment(sketch, "E744", {"start": v(-112.28, -2.2) * mm, "end": v(-112.7, -2.07) * mm});
            skLineSegment(sketch, "E745", {"start": v(-112.7, -2.07) * mm, "end": v(-113.55, -1.78) * mm});
            skLineSegment(sketch, "E746", {"start": v(-113.55, -1.78) * mm, "end": v(-113.97, -1.63) * mm});
            skLineSegment(sketch, "E747", {"start": v(-113.97, -1.63) * mm, "end": v(-113.98, -0.5) * mm});
            skLineSegment(sketch, "E748", {"start": v(-113.98, -0.5) * mm, "end": v(-113.56, -0.33) * mm});
            skLineSegment(sketch, "E749", {"start": v(-113.56, -0.33) * mm, "end": v(-112.72, -0.03) * mm});
            skLineSegment(sketch, "E750", {"start": v(-112.72, -0.03) * mm, "end": v(-112.3, 0.12) * mm});
            skLineSegment(sketch, "E751", {"start": v(-112.3, 0.12) * mm, "end": v(-112.3, 1.27) * mm});
            skLineSegment(sketch, "E752", {"start": v(-112.3, 1.27) * mm, "end": v(-112.71, 1.42) * mm});
            skLineSegment(sketch, "E753", {"start": v(-112.71, 1.42) * mm, "end": v(-113.55, 1.73) * mm});
            skLineSegment(sketch, "E754", {"start": v(-113.55, 1.73) * mm, "end": v(-113.97, 1.9) * mm});
            skLineSegment(sketch, "E755", {"start": v(-113.97, 1.9) * mm, "end": v(-113.94, 3.03) * mm});
            skLineSegment(sketch, "E756", {"start": v(-113.94, 3.03) * mm, "end": v(-113.52, 3.18) * mm});
            skLineSegment(sketch, "E757", {"start": v(-113.52, 3.18) * mm, "end": v(-112.67, 3.46) * mm});
            skLineSegment(sketch, "E758", {"start": v(-112.67, 3.46) * mm, "end": v(-112.24, 3.59) * mm});
            skLineSegment(sketch, "E759", {"start": v(-112.24, 3.59) * mm, "end": v(-112.2, 4.74) * mm});
            skLineSegment(sketch, "E760", {"start": v(-112.2, 4.74) * mm, "end": v(-112.6, 4.9) * mm});
            skLineSegment(sketch, "E761", {"start": v(-112.6, 4.9) * mm, "end": v(-113.43, 5.25) * mm});
            skLineSegment(sketch, "E762", {"start": v(-113.43, 5.25) * mm, "end": v(-113.84, 5.43) * mm});
            skLineSegment(sketch, "E763", {"start": v(-113.84, 5.43) * mm, "end": v(-113.78, 6.56) * mm});
            skLineSegment(sketch, "E764", {"start": v(-113.78, 6.56) * mm, "end": v(-113.35, 6.7) * mm});
            skLineSegment(sketch, "E765", {"start": v(-113.35, 6.7) * mm, "end": v(-112.5, 6.94) * mm});
            skLineSegment(sketch, "E766", {"start": v(-112.5, 6.94) * mm, "end": v(-112.06, 7.06) * mm});
            skLineSegment(sketch, "E767", {"start": v(-112.06, 7.06) * mm, "end": v(-111.98, 8.2) * mm});
            skLineSegment(sketch, "E768", {"start": v(-111.98, 8.2) * mm, "end": v(-112.39, 8.38) * mm});
            skLineSegment(sketch, "E769", {"start": v(-112.39, 8.38) * mm, "end": v(-113.2, 8.75) * mm});
            skLineSegment(sketch, "E770", {"start": v(-113.2, 8.75) * mm, "end": v(-113.6, 8.95) * mm});
            skLineSegment(sketch, "E771", {"start": v(-113.6, 8.95) * mm, "end": v(-113.5, 10.07) * mm});
            skLineSegment(sketch, "E772", {"start": v(-113.5, 10.07) * mm, "end": v(-113.07, 10.2) * mm});
            skLineSegment(sketch, "E773", {"start": v(-113.07, 10.2) * mm, "end": v(-112.2, 10.41) * mm});
            skLineSegment(sketch, "E774", {"start": v(-112.2, 10.41) * mm, "end": v(-111.77, 10.52) * mm});
            skLineSegment(sketch, "E775", {"start": v(-111.77, 10.52) * mm, "end": v(-111.64, 11.66) * mm});
            skLineSegment(sketch, "E776", {"start": v(-111.64, 11.66) * mm, "end": v(-112.05, 11.85) * mm});
            skLineSegment(sketch, "E777", {"start": v(-112.05, 11.85) * mm, "end": v(-112.84, 12.25) * mm});
            skLineSegment(sketch, "E778", {"start": v(-112.84, 12.25) * mm, "end": v(-113.24, 12.46) * mm});
            skLineSegment(sketch, "E779", {"start": v(-113.24, 12.46) * mm, "end": v(-113.1, 13.58) * mm});
            skLineSegment(sketch, "E780", {"start": v(-113.1, 13.58) * mm, "end": v(-112.66, 13.68) * mm});
            skLineSegment(sketch, "E781", {"start": v(-112.66, 13.68) * mm, "end": v(-111.8, 13.88) * mm});
            skLineSegment(sketch, "E782", {"start": v(-111.8, 13.88) * mm, "end": v(-111.36, 13.96) * mm});
            skLineSegment(sketch, "E783", {"start": v(-111.36, 13.96) * mm, "end": v(-111.2, 15.1) * mm});
            skLineSegment(sketch, "E784", {"start": v(-111.2, 15.1) * mm, "end": v(-111.59, 15.3) * mm});
            skLineSegment(sketch, "E785", {"start": v(-111.59, 15.3) * mm, "end": v(-112.37, 15.73) * mm});
            skLineSegment(sketch, "E786", {"start": v(-112.37, 15.73) * mm, "end": v(-112.76, 15.95) * mm});
            skLineSegment(sketch, "E787", {"start": v(-112.76, 15.95) * mm, "end": v(-112.59, 17.07) * mm});
            skLineSegment(sketch, "E788", {"start": v(-112.59, 17.07) * mm, "end": v(-112.15, 17.16) * mm});
            skLineSegment(sketch, "E789", {"start": v(-112.15, 17.16) * mm, "end": v(-111.27, 17.32) * mm});
            skLineSegment(sketch, "E790", {"start": v(-111.27, 17.32) * mm, "end": v(-110.83, 17.4) * mm});
            skLineSegment(sketch, "E791", {"start": v(-110.83, 17.4) * mm, "end": v(-110.63, 18.52) * mm});
            skLineSegment(sketch, "E792", {"start": v(-110.63, 18.52) * mm, "end": v(-111.02, 18.74) * mm});
            skLineSegment(sketch, "E793", {"start": v(-111.02, 18.74) * mm, "end": v(-111.79, 19.2) * mm});
            skLineSegment(sketch, "E794", {"start": v(-111.79, 19.2) * mm, "end": v(-112.17, 19.43) * mm});
            skLineSegment(sketch, "E795", {"start": v(-112.17, 19.43) * mm, "end": v(-111.95, 20.54) * mm});
            skLineSegment(sketch, "E796", {"start": v(-111.95, 20.54) * mm, "end": v(-111.51, 20.62) * mm});
            skLineSegment(sketch, "E797", {"start": v(-111.51, 20.62) * mm, "end": v(-110.63, 20.75) * mm});
            skLineSegment(sketch, "E798", {"start": v(-110.63, 20.75) * mm, "end": v(-110.19, 20.8) * mm});
            skLineSegment(sketch, "E799", {"start": v(-110.19, 20.8) * mm, "end": v(-109.95, 21.93) * mm});
            skLineSegment(sketch, "E800", {"start": v(-109.95, 21.93) * mm, "end": v(-110.33, 22.16) * mm});
            skLineSegment(sketch, "E801", {"start": v(-110.33, 22.16) * mm, "end": v(-111.08, 22.64) * mm});
            skLineSegment(sketch, "E802", {"start": v(-111.08, 22.64) * mm, "end": v(-111.46, 22.89) * mm});
            skLineSegment(sketch, "E803", {"start": v(-111.46, 22.89) * mm, "end": v(-111.2, 23.99) * mm});
            skLineSegment(sketch, "E804", {"start": v(-111.2, 23.99) * mm, "end": v(-110.76, 24.05) * mm});
            skLineSegment(sketch, "E805", {"start": v(-110.76, 24.05) * mm, "end": v(-109.87, 24.15) * mm});
            skLineSegment(sketch, "E806", {"start": v(-109.87, 24.15) * mm, "end": v(-109.43, 24.2) * mm});
            skLineSegment(sketch, "E807", {"start": v(-109.43, 24.2) * mm, "end": v(-109.16, 25.3) * mm});
            skLineSegment(sketch, "E808", {"start": v(-109.16, 25.3) * mm, "end": v(-109.53, 25.55) * mm});
            skLineSegment(sketch, "E809", {"start": v(-109.53, 25.55) * mm, "end": v(-110.27, 26.06) * mm});
            skLineSegment(sketch, "E810", {"start": v(-110.27, 26.06) * mm, "end": v(-110.63, 26.32) * mm});
            skLineSegment(sketch, "E811", {"start": v(-110.63, 26.32) * mm, "end": v(-110.34, 27.4) * mm});
            skLineSegment(sketch, "E812", {"start": v(-110.34, 27.4) * mm, "end": v(-109.9, 27.45) * mm});
            skLineSegment(sketch, "E813", {"start": v(-109.9, 27.45) * mm, "end": v(-109, 27.53) * mm});
            skLineSegment(sketch, "E814", {"start": v(-109, 27.53) * mm, "end": v(-108.56, 27.55) * mm});
            skLineSegment(sketch, "E815", {"start": v(-108.56, 27.55) * mm, "end": v(-108.25, 28.66) * mm});
            skLineSegment(sketch, "E816", {"start": v(-108.25, 28.66) * mm, "end": v(-108.61, 28.92) * mm});
            skLineSegment(sketch, "E817", {"start": v(-108.61, 28.92) * mm, "end": v(-109.33, 29.44) * mm});
            skLineSegment(sketch, "E818", {"start": v(-109.33, 29.44) * mm, "end": v(-109.7, 29.72) * mm});
            skLineSegment(sketch, "E819", {"start": v(-109.7, 29.72) * mm, "end": v(-109.36, 30.8) * mm});
            skLineSegment(sketch, "E820", {"start": v(-109.36, 30.8) * mm, "end": v(-108.92, 30.83) * mm});
            skLineSegment(sketch, "E821", {"start": v(-108.92, 30.83) * mm, "end": v(-108.02, 30.87) * mm});
            skLineSegment(sketch, "E822", {"start": v(-108.02, 30.87) * mm, "end": v(-107.58, 30.88) * mm});
            skLineSegment(sketch, "E823", {"start": v(-107.58, 30.88) * mm, "end": v(-107.23, 31.98) * mm});
            skLineSegment(sketch, "E824", {"start": v(-107.23, 31.98) * mm, "end": v(-107.58, 32.25) * mm});
            skLineSegment(sketch, "E825", {"start": v(-107.58, 32.25) * mm, "end": v(-108.29, 32.8) * mm});
            skLineSegment(sketch, "E826", {"start": v(-108.29, 32.8) * mm, "end": v(-108.64, 33.08) * mm});
            skLineSegment(sketch, "E827", {"start": v(-108.64, 33.08) * mm, "end": v(-108.27, 34.15) * mm});
            skLineSegment(sketch, "E828", {"start": v(-108.27, 34.15) * mm, "end": v(-107.82, 34.17) * mm});
            skLineSegment(sketch, "E829", {"start": v(-107.82, 34.17) * mm, "end": v(-106.93, 34.18) * mm});
            skLineSegment(sketch, "E830", {"start": v(-106.93, 34.18) * mm, "end": v(-106.49, 34.18) * mm});
            skLineSegment(sketch, "E831", {"start": v(-106.49, 34.18) * mm, "end": v(-106.1, 35.26) * mm});
            skLineSegment(sketch, "E832", {"start": v(-106.1, 35.26) * mm, "end": v(-106.45, 35.54) * mm});
            skLineSegment(sketch, "E833", {"start": v(-106.45, 35.54) * mm, "end": v(-107.13, 36.12) * mm});
            skLineSegment(sketch, "E834", {"start": v(-107.13, 36.12) * mm, "end": v(-107.47, 36.41) * mm});
            skLineSegment(sketch, "E835", {"start": v(-107.47, 36.41) * mm, "end": v(-107.07, 37.47) * mm});
            skLineSegment(sketch, "E836", {"start": v(-107.07, 37.47) * mm, "end": v(-106.62, 37.47) * mm});
            skLineSegment(sketch, "E837", {"start": v(-106.62, 37.47) * mm, "end": v(-105.73, 37.45) * mm});
            skLineSegment(sketch, "E838", {"start": v(-105.73, 37.45) * mm, "end": v(-105.28, 37.44) * mm});
            skLineSegment(sketch, "E839", {"start": v(-105.28, 37.44) * mm, "end": v(-104.86, 38.5) * mm});
            skLineSegment(sketch, "E840", {"start": v(-104.86, 38.5) * mm, "end": v(-105.2, 38.8) * mm});
            skLineSegment(sketch, "E841", {"start": v(-105.2, 38.8) * mm, "end": v(-105.86, 39.4) * mm});
            skLineSegment(sketch, "E842", {"start": v(-105.86, 39.4) * mm, "end": v(-106.19, 39.7) * mm});
            skLineSegment(sketch, "E843", {"start": v(-106.19, 39.7) * mm, "end": v(-105.76, 40.74) * mm});
            skLineSegment(sketch, "E844", {"start": v(-105.76, 40.74) * mm, "end": v(-105.3, 40.73) * mm});
            skLineSegment(sketch, "E845", {"start": v(-105.3, 40.73) * mm, "end": v(-104.41, 40.68) * mm});
            skLineSegment(sketch, "E846", {"start": v(-104.41, 40.68) * mm, "end": v(-103.97, 40.65) * mm});
            skLineSegment(sketch, "E847", {"start": v(-103.97, 40.65) * mm, "end": v(-103.51, 41.7) * mm});
            skLineSegment(sketch, "E848", {"start": v(-103.51, 41.7) * mm, "end": v(-103.84, 42) * mm});
            skLineSegment(sketch, "E849", {"start": v(-103.84, 42) * mm, "end": v(-104.48, 42.63) * mm});
            skLineSegment(sketch, "E850", {"start": v(-104.48, 42.63) * mm, "end": v(-104.8, 42.94) * mm});
            skLineSegment(sketch, "E851", {"start": v(-104.8, 42.94) * mm, "end": v(-104.33, 43.97) * mm});
            skLineSegment(sketch, "E852", {"start": v(-104.33, 43.97) * mm, "end": v(-103.88, 43.94) * mm});
            skLineSegment(sketch, "E853", {"start": v(-103.88, 43.94) * mm, "end": v(-103, 43.87) * mm});
            skLineSegment(sketch, "E854", {"start": v(-103, 43.87) * mm, "end": v(-102.55, 43.82) * mm});
            skLineSegment(sketch, "E855", {"start": v(-102.55, 43.82) * mm, "end": v(-102.06, 44.86) * mm});
            skLineSegment(sketch, "E856", {"start": v(-102.06, 44.86) * mm, "end": v(-102.37, 45.17) * mm});
            skLineSegment(sketch, "E857", {"start": v(-102.37, 45.17) * mm, "end": v(-103, 45.81) * mm});
            skLineSegment(sketch, "E858", {"start": v(-103, 45.81) * mm, "end": v(-103.3, 46.14) * mm});
            skLineSegment(sketch, "E859", {"start": v(-103.3, 46.14) * mm, "end": v(-102.8, 47.15) * mm});
            skLineSegment(sketch, "E860", {"start": v(-102.8, 47.15) * mm, "end": v(-102.35, 47.1) * mm});
            skLineSegment(sketch, "E861", {"start": v(-102.35, 47.1) * mm, "end": v(-101.47, 47) * mm});
            skLineSegment(sketch, "E862", {"start": v(-101.47, 47) * mm, "end": v(-101.03, 46.94) * mm});
            skLineSegment(sketch, "E863", {"start": v(-101.03, 46.94) * mm, "end": v(-100.5, 47.96) * mm});
            skLineSegment(sketch, "E864", {"start": v(-100.5, 47.96) * mm, "end": v(-100.8, 48.28) * mm});
            skLineSegment(sketch, "E865", {"start": v(-100.8, 48.28) * mm, "end": v(-101.4, 48.94) * mm});
            skLineSegment(sketch, "E866", {"start": v(-101.4, 48.94) * mm, "end": v(-101.7, 49.28) * mm});
            skLineSegment(sketch, "E867", {"start": v(-101.7, 49.28) * mm, "end": v(-101.16, 50.28) * mm});
            skLineSegment(sketch, "E868", {"start": v(-101.16, 50.28) * mm, "end": v(-100.72, 50.22) * mm});
            skLineSegment(sketch, "E869", {"start": v(-100.72, 50.22) * mm, "end": v(-99.84, 50.08) * mm});
            skLineSegment(sketch, "E870", {"start": v(-99.84, 50.08) * mm, "end": v(-99.4, 50) * mm});
            skLineSegment(sketch, "E871", {"start": v(-99.4, 50) * mm, "end": v(-98.84, 51) * mm});
            skLineSegment(sketch, "E872", {"start": v(-98.84, 51) * mm, "end": v(-99.13, 51.34) * mm});
            skLineSegment(sketch, "E873", {"start": v(-99.13, 51.34) * mm, "end": v(-99.7, 52.02) * mm});
            skLineSegment(sketch, "E874", {"start": v(-99.7, 52.02) * mm, "end": v(-100, 52.37) * mm});
            skLineSegment(sketch, "E875", {"start": v(-100, 52.37) * mm, "end": v(-99.42, 53.34) * mm});
            skLineSegment(sketch, "E876", {"start": v(-99.42, 53.34) * mm, "end": v(-98.98, 53.27) * mm});
            skLineSegment(sketch, "E877", {"start": v(-98.98, 53.27) * mm, "end": v(-98.1, 53.1) * mm});
            skLineSegment(sketch, "E878", {"start": v(-98.1, 53.1) * mm, "end": v(-97.67, 53.01) * mm});
            skLineSegment(sketch, "E879", {"start": v(-97.67, 53.01) * mm, "end": v(-97.07, 54) * mm});
            skLineSegment(sketch, "E880", {"start": v(-97.07, 54) * mm, "end": v(-97.35, 54.34) * mm});
            skLineSegment(sketch, "E881", {"start": v(-97.35, 54.34) * mm, "end": v(-97.9, 55.04) * mm});
            skLineSegment(sketch, "E882", {"start": v(-97.9, 55.04) * mm, "end": v(-98.18, 55.4) * mm});
            skLineSegment(sketch, "E883", {"start": v(-98.18, 55.4) * mm, "end": v(-97.58, 56.35) * mm});
            skLineSegment(sketch, "E884", {"start": v(-97.58, 56.35) * mm, "end": v(-97.14, 56.26) * mm});
            skLineSegment(sketch, "E885", {"start": v(-97.14, 56.26) * mm, "end": v(-96.27, 56.07) * mm});
            skLineSegment(sketch, "E886", {"start": v(-96.27, 56.07) * mm, "end": v(-95.84, 55.96) * mm});
            skLineSegment(sketch, "E887", {"start": v(-95.84, 55.96) * mm, "end": v(-95.2, 56.92) * mm});
            skLineSegment(sketch, "E888", {"start": v(-95.2, 56.92) * mm, "end": v(-95.48, 57.28) * mm});
            skLineSegment(sketch, "E889", {"start": v(-95.48, 57.28) * mm, "end": v(-96, 58) * mm});
            skLineSegment(sketch, "E890", {"start": v(-96, 58) * mm, "end": v(-96.27, 58.36) * mm});
            skLineSegment(sketch, "E891", {"start": v(-96.27, 58.36) * mm, "end": v(-95.64, 59.3) * mm});
            skLineSegment(sketch, "E892", {"start": v(-95.64, 59.3) * mm, "end": v(-95.2, 59.2) * mm});
            skLineSegment(sketch, "E893", {"start": v(-95.2, 59.2) * mm, "end": v(-94.34, 58.97) * mm});
            skLineSegment(sketch, "E894", {"start": v(-94.34, 58.97) * mm, "end": v(-93.9, 58.85) * mm});
            skLineSegment(sketch, "E895", {"start": v(-93.9, 58.85) * mm, "end": v(-93.25, 59.79) * mm});
            skLineSegment(sketch, "E896", {"start": v(-93.25, 59.79) * mm, "end": v(-93.5, 60.15) * mm});
            skLineSegment(sketch, "E897", {"start": v(-93.5, 60.15) * mm, "end": v(-94.01, 60.89) * mm});
            skLineSegment(sketch, "E898", {"start": v(-94.01, 60.89) * mm, "end": v(-94.26, 61.26) * mm});
            skLineSegment(sketch, "E899", {"start": v(-94.26, 61.26) * mm, "end": v(-93.6, 62.18) * mm});
            skLineSegment(sketch, "E900", {"start": v(-93.6, 62.18) * mm, "end": v(-93.16, 62.06) * mm});
            skLineSegment(sketch, "E901", {"start": v(-93.16, 62.06) * mm, "end": v(-92.3, 61.8) * mm});
            skLineSegment(sketch, "E902", {"start": v(-92.3, 61.8) * mm, "end": v(-91.88, 61.67) * mm});
            skLineSegment(sketch, "E903", {"start": v(-91.88, 61.67) * mm, "end": v(-91.2, 62.59) * mm});
            skLineSegment(sketch, "E904", {"start": v(-91.2, 62.59) * mm, "end": v(-91.44, 62.96) * mm});
            skLineSegment(sketch, "E905", {"start": v(-91.44, 62.96) * mm, "end": v(-91.92, 63.7) * mm});
            skLineSegment(sketch, "E906", {"start": v(-91.92, 63.7) * mm, "end": v(-92.15, 64.1) * mm});
            skLineSegment(sketch, "E907", {"start": v(-92.15, 64.1) * mm, "end": v(-91.46, 64.98) * mm});
            skLineSegment(sketch, "E908", {"start": v(-91.46, 64.98) * mm, "end": v(-91.03, 64.85) * mm});
            skLineSegment(sketch, "E909", {"start": v(-91.03, 64.85) * mm, "end": v(-90.18, 64.57) * mm});
            skLineSegment(sketch, "E910", {"start": v(-90.18, 64.57) * mm, "end": v(-89.76, 64.42) * mm});
            skLineSegment(sketch, "E911", {"start": v(-89.76, 64.42) * mm, "end": v(-89.04, 65.31) * mm});
            skLineSegment(sketch, "E912", {"start": v(-89.04, 65.31) * mm, "end": v(-89.28, 65.69) * mm});
            skLineSegment(sketch, "E913", {"start": v(-89.28, 65.69) * mm, "end": v(-89.73, 66.46) * mm});
            skLineSegment(sketch, "E914", {"start": v(-89.73, 66.46) * mm, "end": v(-89.95, 66.85) * mm});
            skLineSegment(sketch, "E915", {"start": v(-89.95, 66.85) * mm, "end": v(-89.23, 67.72) * mm});
            skLineSegment(sketch, "E916", {"start": v(-89.23, 67.72) * mm, "end": v(-88.8, 67.57) * mm});
            skLineSegment(sketch, "E917", {"start": v(-88.8, 67.57) * mm, "end": v(-87.97, 67.26) * mm});
            skLineSegment(sketch, "E918", {"start": v(-87.97, 67.26) * mm, "end": v(-87.55, 67.1) * mm});
            skLineSegment(sketch, "E919", {"start": v(-87.55, 67.1) * mm, "end": v(-86.8, 67.97) * mm});
            skLineSegment(sketch, "E920", {"start": v(-86.8, 67.97) * mm, "end": v(-87.02, 68.35) * mm});
            skLineSegment(sketch, "E921", {"start": v(-87.02, 68.35) * mm, "end": v(-87.45, 69.13) * mm});
            skLineSegment(sketch, "E922", {"start": v(-87.45, 69.13) * mm, "end": v(-87.66, 69.53) * mm});
            skLineSegment(sketch, "E923", {"start": v(-87.66, 69.53) * mm, "end": v(-86.9, 70.37) * mm});
            skLineSegment(sketch, "E924", {"start": v(-86.9, 70.37) * mm, "end": v(-86.5, 70.21) * mm});
            skLineSegment(sketch, "E925", {"start": v(-86.5, 70.21) * mm, "end": v(-85.66, 69.87) * mm});
            skLineSegment(sketch, "E926", {"start": v(-85.66, 69.87) * mm, "end": v(-85.26, 69.7) * mm});
            skLineSegment(sketch, "E927", {"start": v(-85.26, 69.7) * mm, "end": v(-84.48, 70.54) * mm});
            skLineSegment(sketch, "E928", {"start": v(-84.48, 70.54) * mm, "end": v(-84.68, 70.93) * mm});
            skLineSegment(sketch, "E929", {"start": v(-84.68, 70.93) * mm, "end": v(-85.09, 71.73) * mm});
            skLineSegment(sketch, "E930", {"start": v(-85.09, 71.73) * mm, "end": v(-85.28, 72.14) * mm});
            skLineSegment(sketch, "E931", {"start": v(-85.28, 72.14) * mm, "end": v(-84.5, 72.95) * mm});
            skLineSegment(sketch, "E932", {"start": v(-84.5, 72.95) * mm, "end": v(-84.09, 72.78) * mm});
            skLineSegment(sketch, "E933", {"start": v(-84.09, 72.78) * mm, "end": v(-83.27, 72.41) * mm});
            skLineSegment(sketch, "E934", {"start": v(-83.27, 72.41) * mm, "end": v(-82.87, 72.22) * mm});
            skLineSegment(sketch, "E935", {"start": v(-82.87, 72.22) * mm, "end": v(-82.06, 73.04) * mm});
            skLineSegment(sketch, "E936", {"start": v(-82.06, 73.04) * mm, "end": v(-82.26, 73.44) * mm});
            skLineSegment(sketch, "E937", {"start": v(-82.26, 73.44) * mm, "end": v(-82.63, 74.25) * mm});
            skLineSegment(sketch, "E938", {"start": v(-82.63, 74.25) * mm, "end": v(-82.82, 74.66) * mm});
            skLineSegment(sketch, "E939", {"start": v(-82.82, 74.66) * mm, "end": v(-82, 75.45) * mm});
            skLineSegment(sketch, "E940", {"start": v(-82, 75.45) * mm, "end": v(-81.6, 75.26) * mm});
            skLineSegment(sketch, "E941", {"start": v(-81.6, 75.26) * mm, "end": v(-80.8, 74.87) * mm});
            skLineSegment(sketch, "E942", {"start": v(-80.8, 74.87) * mm, "end": v(-80.4, 74.66) * mm});
            skLineSegment(sketch, "E943", {"start": v(-80.4, 74.66) * mm, "end": v(-79.57, 75.45) * mm});
            skLineSegment(sketch, "E944", {"start": v(-79.57, 75.45) * mm, "end": v(-79.75, 75.86) * mm});
            skLineSegment(sketch, "E945", {"start": v(-79.75, 75.86) * mm, "end": v(-80.1, 76.68) * mm});
            skLineSegment(sketch, "E946", {"start": v(-80.1, 76.68) * mm, "end": v(-80.27, 77.1) * mm});
            skLineSegment(sketch, "E947", {"start": v(-80.27, 77.1) * mm, "end": v(-79.43, 77.86) * mm});
            skLineSegment(sketch, "E948", {"start": v(-79.43, 77.86) * mm, "end": v(-79.03, 77.66) * mm});
            skLineSegment(sketch, "E949", {"start": v(-79.03, 77.66) * mm, "end": v(-78.24, 77.24) * mm});
            skLineSegment(sketch, "E950", {"start": v(-78.24, 77.24) * mm, "end": v(-77.85, 77.02) * mm});
            skLineSegment(sketch, "E951", {"start": v(-77.85, 77.02) * mm, "end": v(-77, 77.78) * mm});
            skLineSegment(sketch, "E952", {"start": v(-77, 77.78) * mm, "end": v(-77.16, 78.2) * mm});
            skLineSegment(sketch, "E953", {"start": v(-77.16, 78.2) * mm, "end": v(-77.48, 79.03) * mm});
            skLineSegment(sketch, "E954", {"start": v(-77.48, 79.03) * mm, "end": v(-77.64, 79.45) * mm});
            skLineSegment(sketch, "E955", {"start": v(-77.64, 79.45) * mm, "end": v(-76.78, 80.18) * mm});
            skLineSegment(sketch, "E956", {"start": v(-76.78, 80.18) * mm, "end": v(-76.38, 79.97) * mm});
            skLineSegment(sketch, "E957", {"start": v(-76.38, 79.97) * mm, "end": v(-75.6, 79.52) * mm});
            skLineSegment(sketch, "E958", {"start": v(-75.6, 79.52) * mm, "end": v(-75.23, 79.3) * mm});
            skLineSegment(sketch, "E959", {"start": v(-75.23, 79.3) * mm, "end": v(-74.34, 80.02) * mm});
            skLineSegment(sketch, "E960", {"start": v(-74.34, 80.02) * mm, "end": v(-74.5, 80.44) * mm});
            skLineSegment(sketch, "E961", {"start": v(-74.5, 80.44) * mm, "end": v(-74.79, 81.28) * mm});
            skLineSegment(sketch, "E962", {"start": v(-74.79, 81.28) * mm, "end": v(-74.93, 81.71) * mm});
            skLineSegment(sketch, "E963", {"start": v(-74.93, 81.71) * mm, "end": v(-74.04, 82.42) * mm});
            skLineSegment(sketch, "E964", {"start": v(-74.04, 82.42) * mm, "end": v(-73.66, 82.18) * mm});
            skLineSegment(sketch, "E965", {"start": v(-73.66, 82.18) * mm, "end": v(-72.9, 81.71) * mm});
            skLineSegment(sketch, "E966", {"start": v(-72.9, 81.71) * mm, "end": v(-72.53, 81.47) * mm});
            skLineSegment(sketch, "E967", {"start": v(-72.53, 81.47) * mm, "end": v(-71.62, 82.17) * mm});
            skLineSegment(sketch, "E968", {"start": v(-71.62, 82.17) * mm, "end": v(-71.76, 82.6) * mm});
            skLineSegment(sketch, "E969", {"start": v(-71.76, 82.6) * mm, "end": v(-72.02, 83.45) * mm});
            skLineSegment(sketch, "E970", {"start": v(-72.02, 83.45) * mm, "end": v(-72.15, 83.88) * mm});
            skLineSegment(sketch, "E971", {"start": v(-72.15, 83.88) * mm, "end": v(-71.24, 84.55) * mm});
            skLineSegment(sketch, "E972", {"start": v(-71.24, 84.55) * mm, "end": v(-70.86, 84.31) * mm});
            skLineSegment(sketch, "E973", {"start": v(-70.86, 84.31) * mm, "end": v(-70.12, 83.81) * mm});
            skLineSegment(sketch, "E974", {"start": v(-70.12, 83.81) * mm, "end": v(-69.75, 83.56) * mm});
            skLineSegment(sketch, "E975", {"start": v(-69.75, 83.56) * mm, "end": v(-68.82, 84.23) * mm});
            skLineSegment(sketch, "E976", {"start": v(-68.82, 84.23) * mm, "end": v(-68.95, 84.66) * mm});
            skLineSegment(sketch, "E977", {"start": v(-68.95, 84.66) * mm, "end": v(-69.18, 85.52) * mm});
            skLineSegment(sketch, "E978", {"start": v(-69.18, 85.52) * mm, "end": v(-69.3, 85.95) * mm});
            skLineSegment(sketch, "E979", {"start": v(-69.3, 85.95) * mm, "end": v(-68.36, 86.6) * mm});
            skLineSegment(sketch, "E980", {"start": v(-68.36, 86.6) * mm, "end": v(-68, 86.34) * mm});
            skLineSegment(sketch, "E981", {"start": v(-68, 86.34) * mm, "end": v(-67.27, 85.82) * mm});
            skLineSegment(sketch, "E982", {"start": v(-67.27, 85.82) * mm, "end": v(-66.91, 85.55) * mm});
            skLineSegment(sketch, "E983", {"start": v(-66.91, 85.55) * mm, "end": v(-65.96, 86.2) * mm});
            skLineSegment(sketch, "E984", {"start": v(-65.96, 86.2) * mm, "end": v(-66.07, 86.62) * mm});
            skLineSegment(sketch, "E985", {"start": v(-66.07, 86.62) * mm, "end": v(-66.27, 87.5) * mm});
            skLineSegment(sketch, "E986", {"start": v(-66.27, 87.5) * mm, "end": v(-66.37, 87.93) * mm});
            skLineSegment(sketch, "E987", {"start": v(-66.37, 87.93) * mm, "end": v(-65.42, 88.54) * mm});
            skLineSegment(sketch, "E988", {"start": v(-65.42, 88.54) * mm, "end": v(-65.06, 88.28) * mm});
            skLineSegment(sketch, "E989", {"start": v(-65.06, 88.28) * mm, "end": v(-64.35, 87.73) * mm});
            skLineSegment(sketch, "E990", {"start": v(-64.35, 87.73) * mm, "end": v(-64, 87.45) * mm});
            skLineSegment(sketch, "E991", {"start": v(-64, 87.45) * mm, "end": v(-63.03, 88.06) * mm});
            skLineSegment(sketch, "E992", {"start": v(-63.03, 88.06) * mm, "end": v(-63.13, 88.5) * mm});
            skLineSegment(sketch, "E993", {"start": v(-63.13, 88.5) * mm, "end": v(-63.3, 89.37) * mm});
            skLineSegment(sketch, "E994", {"start": v(-63.3, 89.37) * mm, "end": v(-63.38, 89.81) * mm});
            skLineSegment(sketch, "E995", {"start": v(-63.38, 89.81) * mm, "end": v(-62.41, 90.4) * mm});
            skLineSegment(sketch, "E996", {"start": v(-62.41, 90.4) * mm, "end": v(-62.06, 90.11) * mm});
            skLineSegment(sketch, "E997", {"start": v(-62.06, 90.11) * mm, "end": v(-61.37, 89.54) * mm});
            skLineSegment(sketch, "E998", {"start": v(-61.37, 89.54) * mm, "end": v(-61.04, 89.25) * mm});
            skLineSegment(sketch, "E999", {"start": v(-61.04, 89.25) * mm, "end": v(-60.04, 89.82) * mm});
            skLineSegment(sketch, "E1000", {"start": v(-60.04, 89.82) * mm, "end": v(-60.12, 90.26) * mm});
            skLineSegment(sketch, "E1001", {"start": v(-60.12, 90.26) * mm, "end": v(-60.27, 91.14) * mm});
            skLineSegment(sketch, "E1002", {"start": v(-60.27, 91.14) * mm, "end": v(-60.34, 91.59) * mm});
            skLineSegment(sketch, "E1003", {"start": v(-60.34, 91.59) * mm, "end": v(-59.35, 92.13) * mm});
            skLineSegment(sketch, "E1004", {"start": v(-59.35, 92.13) * mm, "end": v(-59, 91.84) * mm});
            skLineSegment(sketch, "E1005", {"start": v(-59, 91.84) * mm, "end": v(-58.34, 91.25) * mm});
            skLineSegment(sketch, "E1006", {"start": v(-58.34, 91.25) * mm, "end": v(-58, 90.95) * mm});
            skLineSegment(sketch, "E1007", {"start": v(-58, 90.95) * mm, "end": v(-57, 91.49) * mm});
            skLineSegment(sketch, "E1008", {"start": v(-57, 91.49) * mm, "end": v(-57.06, 91.93) * mm});
            skLineSegment(sketch, "E1009", {"start": v(-57.06, 91.93) * mm, "end": v(-57.18, 92.81) * mm});
            skLineSegment(sketch, "E1010", {"start": v(-57.18, 92.81) * mm, "end": v(-57.23, 93.26) * mm});
            skLineSegment(sketch, "E1011", {"start": v(-57.23, 93.26) * mm, "end": v(-56.22, 93.77) * mm});
            skLineSegment(sketch, "E1012", {"start": v(-56.22, 93.77) * mm, "end": v(-55.9, 93.47) * mm});
            skLineSegment(sketch, "E1013", {"start": v(-55.9, 93.47) * mm, "end": v(-55.24, 92.86) * mm});
            skLineSegment(sketch, "E1014", {"start": v(-55.24, 92.86) * mm, "end": v(-54.93, 92.55) * mm});
            skLineSegment(sketch, "E1015", {"start": v(-54.93, 92.55) * mm, "end": v(-53.9, 93.05) * mm});
            skLineSegment(sketch, "E1016", {"start": v(-53.9, 93.05) * mm, "end": v(-53.95, 93.5) * mm});
            skLineSegment(sketch, "E1017", {"start": v(-53.95, 93.5) * mm, "end": v(-54.03, 94.38) * mm});
            skLineSegment(sketch, "E1018", {"start": v(-54.03, 94.38) * mm, "end": v(-54.07, 94.83) * mm});
            skLineSegment(sketch, "E1019", {"start": v(-54.07, 94.83) * mm, "end": v(-53.05, 95.3) * mm});
            skLineSegment(sketch, "E1020", {"start": v(-53.05, 95.3) * mm, "end": v(-52.73, 95) * mm});
            skLineSegment(sketch, "E1021", {"start": v(-52.73, 95) * mm, "end": v(-52.1, 94.36) * mm});
            skLineSegment(sketch, "E1022", {"start": v(-52.1, 94.36) * mm, "end": v(-51.8, 94.04) * mm});
            skLineSegment(sketch, "E1023", {"start": v(-51.8, 94.04) * mm, "end": v(-50.74, 94.5) * mm});
            skLineSegment(sketch, "E1024", {"start": v(-50.74, 94.5) * mm, "end": v(-50.78, 94.95) * mm});
            skLineSegment(sketch, "E1025", {"start": v(-50.78, 94.95) * mm, "end": v(-50.84, 95.84) * mm});
            skLineSegment(sketch, "E1026", {"start": v(-50.84, 95.84) * mm, "end": v(-50.86, 96.3) * mm});
            skLineSegment(sketch, "E1027", {"start": v(-50.86, 96.3) * mm, "end": v(-49.82, 96.74) * mm});
            skLineSegment(sketch, "E1028", {"start": v(-49.82, 96.74) * mm, "end": v(-49.5, 96.41) * mm});
            skLineSegment(sketch, "E1029", {"start": v(-49.5, 96.41) * mm, "end": v(-48.9, 95.75) * mm});
            skLineSegment(sketch, "E1030", {"start": v(-48.9, 95.75) * mm, "end": v(-48.6, 95.42) * mm});
            skLineSegment(sketch, "E1031", {"start": v(-48.6, 95.42) * mm, "end": v(-47.55, 95.86) * mm});
            skLineSegment(sketch, "E1032", {"start": v(-47.55, 95.86) * mm, "end": v(-47.57, 96.3) * mm});
            skLineSegment(sketch, "E1033", {"start": v(-47.57, 96.3) * mm, "end": v(-47.6, 97.2) * mm});
            skLineSegment(sketch, "E1034", {"start": v(-47.6, 97.2) * mm, "end": v(-47.6, 97.64) * mm});
            skLineSegment(sketch, "E1035", {"start": v(-47.6, 97.64) * mm, "end": v(-46.55, 98.05) * mm});
            skLineSegment(sketch, "E1036", {"start": v(-46.55, 98.05) * mm, "end": v(-46.25, 97.72) * mm});
            skLineSegment(sketch, "E1037", {"start": v(-46.25, 97.72) * mm, "end": v(-45.66, 97.04) * mm});
            skLineSegment(sketch, "E1038", {"start": v(-45.66, 97.04) * mm, "end": v(-45.38, 96.7) * mm});
            skLineSegment(sketch, "E1039", {"start": v(-45.38, 96.7) * mm, "end": v(-44.3, 97.1) * mm});
            skLineSegment(sketch, "E1040", {"start": v(-44.3, 97.1) * mm, "end": v(-44.31, 97.54) * mm});
            skLineSegment(sketch, "E1041", {"start": v(-44.31, 97.54) * mm, "end": v(-44.3, 98.44) * mm});
            skLineSegment(sketch, "E1042", {"start": v(-44.3, 98.44) * mm, "end": v(-44.3, 98.89) * mm});
            skLineSegment(sketch, "E1043", {"start": v(-44.3, 98.89) * mm, "end": v(-43.23, 99.26) * mm});
            skLineSegment(sketch, "E1044", {"start": v(-43.23, 99.26) * mm, "end": v(-42.94, 98.92) * mm});
            skLineSegment(sketch, "E1045", {"start": v(-42.94, 98.92) * mm, "end": v(-42.38, 98.22) * mm});
            skLineSegment(sketch, "E1046", {"start": v(-42.38, 98.22) * mm, "end": v(-42.11, 97.87) * mm});
            skLineSegment(sketch, "E1047", {"start": v(-42.11, 97.87) * mm, "end": v(-41.02, 98.23) * mm});
            skLineSegment(sketch, "E1048", {"start": v(-41.02, 98.23) * mm, "end": v(-41.01, 98.67) * mm});
            skLineSegment(sketch, "E1049", {"start": v(-41.01, 98.67) * mm, "end": v(-40.98, 99.57) * mm});
            skLineSegment(sketch, "E1050", {"start": v(-40.98, 99.57) * mm, "end": v(-40.96, 100.02) * mm});
            skLineSegment(sketch, "E1051", {"start": v(-40.96, 100.02) * mm, "end": v(-39.88, 100.35) * mm});
            skLineSegment(sketch, "E1052", {"start": v(-39.88, 100.35) * mm, "end": v(-39.6, 100) * mm});
            skLineSegment(sketch, "E1053", {"start": v(-39.6, 100) * mm, "end": v(-39.06, 99.29) * mm});
            skLineSegment(sketch, "E1054", {"start": v(-39.06, 99.29) * mm, "end": v(-38.8, 98.93) * mm});
            skLineSegment(sketch, "E1055", {"start": v(-38.8, 98.93) * mm, "end": v(-37.7, 99.25) * mm});
            skLineSegment(sketch, "E1056", {"start": v(-37.7, 99.25) * mm, "end": v(-37.68, 99.7) * mm});
            skLineSegment(sketch, "E1057", {"start": v(-37.68, 99.7) * mm, "end": v(-37.62, 100.59) * mm});
            skLineSegment(sketch, "E1058", {"start": v(-37.62, 100.59) * mm, "end": v(-37.58, 101.03) * mm});
            skLineSegment(sketch, "E1059", {"start": v(-37.58, 101.03) * mm, "end": v(-36.49, 101.34) * mm});
            skLineSegment(sketch, "E1060", {"start": v(-36.49, 101.34) * mm, "end": v(-36.22, 100.97) * mm});
            skLineSegment(sketch, "E1061", {"start": v(-36.22, 100.97) * mm, "end": v(-35.71, 100.24) * mm});
            skLineSegment(sketch, "E1062", {"start": v(-35.71, 100.24) * mm, "end": v(-35.46, 99.87) * mm});
            skLineSegment(sketch, "E1063", {"start": v(-35.46, 99.87) * mm, "end": v(-34.35, 100.16) * mm});
            skLineSegment(sketch, "E1064", {"start": v(-34.35, 100.16) * mm, "end": v(-34.32, 100.6) * mm});
            skLineSegment(sketch, "E1065", {"start": v(-34.32, 100.6) * mm, "end": v(-34.22, 101.5) * mm});
            skLineSegment(sketch, "E1066", {"start": v(-34.22, 101.5) * mm, "end": v(-34.17, 101.94) * mm});
            skLineSegment(sketch, "E1067", {"start": v(-34.17, 101.94) * mm, "end": v(-33.07, 102.2) * mm});
            skLineSegment(sketch, "E1068", {"start": v(-33.07, 102.2) * mm, "end": v(-32.82, 101.83) * mm});
            skLineSegment(sketch, "E1069", {"start": v(-32.82, 101.83) * mm, "end": v(-32.33, 101.08) * mm});
            skLineSegment(sketch, "E1070", {"start": v(-32.33, 101.08) * mm, "end": v(-32.1, 100.7) * mm});
            skLineSegment(sketch, "E1071", {"start": v(-32.1, 100.7) * mm, "end": v(-30.97, 100.96) * mm});
            skLineSegment(sketch, "E1072", {"start": v(-30.97, 100.96) * mm, "end": v(-30.92, 101.4) * mm});
            skLineSegment(sketch, "E1073", {"start": v(-30.92, 101.4) * mm, "end": v(-30.8, 102.28) * mm});
            skLineSegment(sketch, "E1074", {"start": v(-30.8, 102.28) * mm, "end": v(-30.73, 102.73) * mm});
            skLineSegment(sketch, "E1075", {"start": v(-30.73, 102.73) * mm, "end": v(-29.62, 102.95) * mm});
            skLineSegment(sketch, "E1076", {"start": v(-29.62, 102.95) * mm, "end": v(-29.38, 102.57) * mm});
            skLineSegment(sketch, "E1077", {"start": v(-29.38, 102.57) * mm, "end": v(-28.92, 101.81) * mm});
            skLineSegment(sketch, "E1078", {"start": v(-28.92, 101.81) * mm, "end": v(-28.7, 101.43) * mm});
            skLineSegment(sketch, "E1079", {"start": v(-28.7, 101.43) * mm, "end": v(-27.57, 101.64) * mm});
            skLineSegment(sketch, "E1080", {"start": v(-27.57, 101.64) * mm, "end": v(-27.5, 102.08) * mm});
            skLineSegment(sketch, "E1081", {"start": v(-27.5, 102.08) * mm, "end": v(-27.35, 102.96) * mm});
            skLineSegment(sketch, "E1082", {"start": v(-27.35, 102.96) * mm, "end": v(-27.27, 103.4) * mm});
            skLineSegment(sketch, "E1083", {"start": v(-27.27, 103.4) * mm, "end": v(-26.15, 103.6) * mm});
            skLineSegment(sketch, "E1084", {"start": v(-26.15, 103.6) * mm, "end": v(-25.93, 103.2) * mm});
            skLineSegment(sketch, "E1085", {"start": v(-25.93, 103.2) * mm, "end": v(-25.49, 102.42) * mm});
            skLineSegment(sketch, "E1086", {"start": v(-25.49, 102.42) * mm, "end": v(-25.28, 102.03) * mm});
            skLineSegment(sketch, "E1087", {"start": v(-25.28, 102.03) * mm, "end": v(-24.14, 102.2) * mm});
            skLineSegment(sketch, "E1088", {"start": v(-24.14, 102.2) * mm, "end": v(-24.06, 102.64) * mm});
            skLineSegment(sketch, "E1089", {"start": v(-24.06, 102.64) * mm, "end": v(-23.88, 103.52) * mm});
            skLineSegment(sketch, "E1090", {"start": v(-23.88, 103.52) * mm, "end": v(-23.78, 103.96) * mm});
            skLineSegment(sketch, "E1091", {"start": v(-23.78, 103.96) * mm, "end": v(-22.66, 104.1) * mm});
            skLineSegment(sketch, "E1092", {"start": v(-22.66, 104.1) * mm, "end": v(-22.45, 103.71) * mm});
            skLineSegment(sketch, "E1093", {"start": v(-22.45, 103.71) * mm, "end": v(-22.04, 102.92) * mm});
            skLineSegment(sketch, "E1094", {"start": v(-22.04, 102.92) * mm, "end": v(-21.84, 102.52) * mm});
            skLineSegment(sketch, "E1095", {"start": v(-21.84, 102.52) * mm, "end": v(-20.7, 102.66) * mm});
            skLineSegment(sketch, "E1096", {"start": v(-20.7, 102.66) * mm, "end": v(-20.6, 103.1) * mm});
            skLineSegment(sketch, "E1097", {"start": v(-20.6, 103.1) * mm, "end": v(-20.4, 103.96) * mm});
            skLineSegment(sketch, "E1098", {"start": v(-20.4, 103.96) * mm, "end": v(-20.28, 104.4) * mm});
            skLineSegment(sketch, "E1099", {"start": v(-20.28, 104.4) * mm, "end": v(-19.16, 104.5) * mm});
            skLineSegment(sketch, "E1100", {"start": v(-19.16, 104.5) * mm, "end": v(-18.96, 104.1) * mm});
            skLineSegment(sketch, "E1101", {"start": v(-18.96, 104.1) * mm, "end": v(-18.57, 103.3) * mm});
            skLineSegment(sketch, "E1102", {"start": v(-18.57, 103.3) * mm, "end": v(-18.4, 102.9) * mm});
            skLineSegment(sketch, "E1103", {"start": v(-18.4, 102.9) * mm, "end": v(-17.25, 103) * mm});
            skLineSegment(sketch, "E1104", {"start": v(-17.25, 103) * mm, "end": v(-17.14, 103.42) * mm});
            skLineSegment(sketch, "E1105", {"start": v(-17.14, 103.42) * mm, "end": v(-16.9, 104.28) * mm});
            skLineSegment(sketch, "E1106", {"start": v(-16.9, 104.28) * mm, "end": v(-16.77, 104.72) * mm});
            skLineSegment(sketch, "E1107", {"start": v(-16.77, 104.72) * mm, "end": v(-15.64, 104.8) * mm});
            skLineSegment(sketch, "E1108", {"start": v(-15.64, 104.8) * mm, "end": v(-15.45, 104.38) * mm});
            skLineSegment(sketch, "E1109", {"start": v(-15.45, 104.38) * mm, "end": v(-15.1, 103.56) * mm});
            skLineSegment(sketch, "E1110", {"start": v(-15.1, 103.56) * mm, "end": v(-14.93, 103.15) * mm});
            skLineSegment(sketch, "E1111", {"start": v(-14.93, 103.15) * mm, "end": v(-13.78, 103.21) * mm});
            skLineSegment(sketch, "E1112", {"start": v(-13.78, 103.21) * mm, "end": v(-13.66, 103.64) * mm});
            skLineSegment(sketch, "E1113", {"start": v(-13.66, 103.64) * mm, "end": v(-13.39, 104.5) * mm});
            skLineSegment(sketch, "E1114", {"start": v(-13.39, 104.5) * mm, "end": v(-13.25, 104.92) * mm});
            skLineSegment(sketch, "E1115", {"start": v(-13.25, 104.92) * mm, "end": v(-12.12, 104.96) * mm});
            skLineSegment(sketch, "E1116", {"start": v(-12.12, 104.96) * mm, "end": v(-11.94, 104.54) * mm});
            skLineSegment(sketch, "E1117", {"start": v(-11.94, 104.54) * mm, "end": v(-11.62, 103.71) * mm});
            skLineSegment(sketch, "E1118", {"start": v(-11.62, 103.71) * mm, "end": v(-11.46, 103.3) * mm});
            skLineSegment(sketch, "E1119", {"start": v(-11.46, 103.3) * mm, "end": v(-10.31, 103.32) * mm});
            skLineSegment(sketch, "E1120", {"start": v(-10.31, 103.32) * mm, "end": v(-10.17, 103.74) * mm});
            skLineSegment(sketch, "E1121", {"start": v(-10.17, 103.74) * mm, "end": v(-9.88, 104.58) * mm});
            skLineSegment(sketch, "E1122", {"start": v(-9.88, 104.58) * mm, "end": v(-9.72, 105) * mm});
            skLineSegment(sketch, "E1123", {"start": v(-9.72, 105) * mm, "end": v(-8.59, 105) * mm});
            skLineSegment(sketch, "E1124", {"start": v(-8.59, 105) * mm, "end": v(-8.43, 104.58) * mm});
            skLineSegment(sketch, "E1125", {"start": v(-8.43, 104.58) * mm, "end": v(-8.13, 103.74) * mm});
            skLineSegment(sketch, "E1126", {"start": v(-8.13, 103.74) * mm, "end": v(-7.99, 103.32) * mm});
            skLineSegment(sketch, "E1127", {"start": v(-7.99, 103.32) * mm, "end": v(-6.84, 103.3) * mm});
            skLineSegment(sketch, "E1128", {"start": v(-6.84, 103.3) * mm, "end": v(-6.69, 103.72) * mm});
            skLineSegment(sketch, "E1129", {"start": v(-6.69, 103.72) * mm, "end": v(-6.36, 104.55) * mm});
            skLineSegment(sketch, "E1130", {"start": v(-6.36, 104.55) * mm, "end": v(-6.2, 104.97) * mm});
            skLineSegment(sketch, "E1131", {"start": v(-6.2, 104.97) * mm, "end": v(-5.06, 104.93) * mm});
            skLineSegment(sketch, "E1132", {"start": v(-5.06, 104.93) * mm, "end": v(-4.92, 104.5) * mm});
            skLineSegment(sketch, "E1133", {"start": v(-4.92, 104.5) * mm, "end": v(-4.65, 103.65) * mm});
            skLineSegment(sketch, "E1134", {"start": v(-4.65, 103.65) * mm, "end": v(-4.52, 103.23) * mm});
            skLineSegment(sketch, "E1135", {"start": v(-4.52, 103.23) * mm, "end": v(-3.37, 103.17) * mm});
            skLineSegment(sketch, "E1136", {"start": v(-3.37, 103.17) * mm, "end": v(-3.2, 103.58) * mm});
            skLineSegment(sketch, "E1137", {"start": v(-3.2, 103.58) * mm, "end": v(-2.85, 104.4) * mm});
            skLineSegment(sketch, "E1138", {"start": v(-2.85, 104.4) * mm, "end": v(-2.67, 104.81) * mm});
            skLineSegment(sketch, "E1139", {"start": v(-2.67, 104.81) * mm, "end": v(-1.54, 104.74) * mm});
            skLineSegment(sketch, "E1140", {"start": v(-1.54, 104.74) * mm, "end": v(-1.4, 104.31) * mm});
            skLineSegment(sketch, "E1141", {"start": v(-1.4, 104.31) * mm, "end": v(-1.17, 103.45) * mm});
            skLineSegment(sketch, "E1142", {"start": v(-1.17, 103.45) * mm, "end": v(-1.05, 103.02) * mm});
            skLineSegment(sketch, "E1143", {"start": v(-1.05, 103.02) * mm, "end": v(0.1, 102.93) * mm});
            skLineSegment(sketch, "E1144", {"start": v(0.1, 102.93) * mm, "end": v(0.27, 103.33) * mm});
            skLineSegment(sketch, "E1145", {"start": v(0.27, 103.33) * mm, "end": v(0.65, 104.14) * mm});
            skLineSegment(sketch, "E1146", {"start": v(0.65, 104.14) * mm, "end": v(0.85, 104.54) * mm});
            skLineSegment(sketch, "E1147", {"start": v(0.85, 104.54) * mm, "end": v(1.98, 104.43) * mm});
            skLineSegment(sketch, "E1148", {"start": v(1.98, 104.43) * mm, "end": v(2.1, 104) * mm});
            skLineSegment(sketch, "E1149", {"start": v(2.1, 104) * mm, "end": v(2.3, 103.13) * mm});
            skLineSegment(sketch, "E1150", {"start": v(2.3, 103.13) * mm, "end": v(2.4, 102.7) * mm});
            skLineSegment(sketch, "E1151", {"start": v(2.4, 102.7) * mm, "end": v(3.54, 102.56) * mm});
            skLineSegment(sketch, "E1152", {"start": v(3.54, 102.56) * mm, "end": v(3.74, 102.96) * mm});
            skLineSegment(sketch, "E1153", {"start": v(3.74, 102.96) * mm, "end": v(4.15, 103.76) * mm});
            skLineSegment(sketch, "E1154", {"start": v(4.15, 103.76) * mm, "end": v(4.36, 104.15) * mm});
            skLineSegment(sketch, "E1155", {"start": v(4.36, 104.15) * mm, "end": v(5.48, 104) * mm});
            skLineSegment(sketch, "E1156", {"start": v(5.48, 104) * mm, "end": v(5.58, 103.57) * mm});
            skLineSegment(sketch, "E1157", {"start": v(5.58, 103.57) * mm, "end": v(5.76, 102.7) * mm});
            skLineSegment(sketch, "E1158", {"start": v(5.76, 102.7) * mm, "end": v(5.85, 102.26) * mm});
            skLineSegment(sketch, "E1159", {"start": v(5.85, 102.26) * mm, "end": v(6.98, 102.09) * mm});
            skLineSegment(sketch, "E1160", {"start": v(6.98, 102.09) * mm, "end": v(7.2, 102.48) * mm});
            skLineSegment(sketch, "E1161", {"start": v(7.2, 102.48) * mm, "end": v(7.62, 103.26) * mm});
            skLineSegment(sketch, "E1162", {"start": v(7.62, 103.26) * mm, "end": v(7.85, 103.65) * mm});
            skLineSegment(sketch, "E1163", {"start": v(7.85, 103.65) * mm, "end": v(8.96, 103.46) * mm});
            skLineSegment(sketch, "E1164", {"start": v(8.96, 103.46) * mm, "end": v(9.05, 103.02) * mm});
            skLineSegment(sketch, "E1165", {"start": v(9.05, 103.02) * mm, "end": v(9.2, 102.14) * mm});
            skLineSegment(sketch, "E1166", {"start": v(9.2, 102.14) * mm, "end": v(9.27, 101.7) * mm});
            skLineSegment(sketch, "E1167", {"start": v(9.27, 101.7) * mm, "end": v(10.4, 101.5) * mm});
            skLineSegment(sketch, "E1168", {"start": v(10.4, 101.5) * mm, "end": v(10.62, 101.88) * mm});
            skLineSegment(sketch, "E1169", {"start": v(10.62, 101.88) * mm, "end": v(11.08, 102.64) * mm});
            skLineSegment(sketch, "E1170", {"start": v(11.08, 102.64) * mm, "end": v(11.32, 103.02) * mm});
            skLineSegment(sketch, "E1171", {"start": v(11.32, 103.02) * mm, "end": v(12.43, 102.8) * mm});
            skLineSegment(sketch, "E1172", {"start": v(12.43, 102.8) * mm, "end": v(12.5, 102.36) * mm});
            skLineSegment(sketch, "E1173", {"start": v(12.5, 102.36) * mm, "end": v(12.63, 101.47) * mm});
            skLineSegment(sketch, "E1174", {"start": v(12.63, 101.47) * mm, "end": v(12.68, 101.03) * mm});
            skLineSegment(sketch, "E1175", {"start": v(12.68, 101.03) * mm, "end": v(13.8, 100.78) * mm});
            skLineSegment(sketch, "E1176", {"start": v(13.8, 100.78) * mm, "end": v(14.04, 101.16) * mm});
            skLineSegment(sketch, "E1177", {"start": v(14.04, 101.16) * mm, "end": v(14.52, 101.91) * mm});
            skLineSegment(sketch, "E1178", {"start": v(14.52, 101.91) * mm, "end": v(14.77, 102.28) * mm});
            skLineSegment(sketch, "E1179", {"start": v(14.77, 102.28) * mm, "end": v(15.87, 102.02) * mm});
            skLineSegment(sketch, "E1180", {"start": v(15.87, 102.02) * mm, "end": v(15.93, 101.58) * mm});
            skLineSegment(sketch, "E1181", {"start": v(15.93, 101.58) * mm, "end": v(16.02, 100.69) * mm});
            skLineSegment(sketch, "E1182", {"start": v(16.02, 100.69) * mm, "end": v(16.06, 100.25) * mm});
            skLineSegment(sketch, "E1183", {"start": v(16.06, 100.25) * mm, "end": v(17.17, 99.96) * mm});
            skLineSegment(sketch, "E1184", {"start": v(17.17, 99.96) * mm, "end": v(17.42, 100.33) * mm});
            skLineSegment(sketch, "E1185", {"start": v(17.42, 100.33) * mm, "end": v(17.93, 101.06) * mm});
            skLineSegment(sketch, "E1186", {"start": v(17.93, 101.06) * mm, "end": v(18.2, 101.43) * mm});
            skLineSegment(sketch, "E1187", {"start": v(18.2, 101.43) * mm, "end": v(19.28, 101.13) * mm});
            skLineSegment(sketch, "E1188", {"start": v(19.28, 101.13) * mm, "end": v(19.33, 100.68) * mm});
            skLineSegment(sketch, "E1189", {"start": v(19.33, 100.68) * mm, "end": v(19.4, 99.8) * mm});
            skLineSegment(sketch, "E1190", {"start": v(19.4, 99.8) * mm, "end": v(19.42, 99.35) * mm});
            skLineSegment(sketch, "E1191", {"start": v(19.42, 99.35) * mm, "end": v(20.52, 99.03) * mm});
            skLineSegment(sketch, "E1192", {"start": v(20.52, 99.03) * mm, "end": v(20.78, 99.39) * mm});
            skLineSegment(sketch, "E1193", {"start": v(20.78, 99.39) * mm, "end": v(21.31, 100.1) * mm});
            skLineSegment(sketch, "E1194", {"start": v(21.31, 100.1) * mm, "end": v(21.59, 100.46) * mm});
            skLineSegment(sketch, "E1195", {"start": v(21.59, 100.46) * mm, "end": v(22.67, 100.12) * mm});
            skLineSegment(sketch, "E1196", {"start": v(22.67, 100.12) * mm, "end": v(22.7, 99.67) * mm});
            skLineSegment(sketch, "E1197", {"start": v(22.7, 99.67) * mm, "end": v(22.73, 98.78) * mm});
            skLineSegment(sketch, "E1198", {"start": v(22.73, 98.78) * mm, "end": v(22.74, 98.34) * mm});
            skLineSegment(sketch, "E1199", {"start": v(22.74, 98.34) * mm, "end": v(23.83, 97.98) * mm});
            skLineSegment(sketch, "E1200", {"start": v(23.83, 97.98) * mm, "end": v(24.1, 98.33) * mm});
            skLineSegment(sketch, "E1201", {"start": v(24.1, 98.33) * mm, "end": v(24.66, 99.03) * mm});
            skLineSegment(sketch, "E1202", {"start": v(24.66, 99.03) * mm, "end": v(24.94, 99.37) * mm});
            skLineSegment(sketch, "E1203", {"start": v(24.94, 99.37) * mm, "end": v(26.01, 99) * mm});
            skLineSegment(sketch, "E1204", {"start": v(26.01, 99) * mm, "end": v(26.02, 98.55) * mm});
            skLineSegment(sketch, "E1205", {"start": v(26.02, 98.55) * mm, "end": v(26.03, 97.66) * mm});
            skLineSegment(sketch, "E1206", {"start": v(26.03, 97.66) * mm, "end": v(26.02, 97.22) * mm});
            skLineSegment(sketch, "E1207", {"start": v(26.02, 97.22) * mm, "end": v(27.1, 96.82) * mm});
            skLineSegment(sketch, "E1208", {"start": v(27.1, 96.82) * mm, "end": v(27.38, 97.16) * mm});
            skLineSegment(sketch, "E1209", {"start": v(27.38, 97.16) * mm, "end": v(27.96, 97.84) * mm});
            skLineSegment(sketch, "E1210", {"start": v(27.96, 97.84) * mm, "end": v(28.26, 98.18) * mm});
            skLineSegment(sketch, "E1211", {"start": v(28.26, 98.18) * mm, "end": v(29.32, 97.77) * mm});
            skLineSegment(sketch, "E1212", {"start": v(29.32, 97.77) * mm, "end": v(29.31, 97.32) * mm});
            skLineSegment(sketch, "E1213", {"start": v(29.31, 97.32) * mm, "end": v(29.29, 96.43) * mm});
            skLineSegment(sketch, "E1214", {"start": v(29.29, 96.43) * mm, "end": v(29.27, 95.99) * mm});
            skLineSegment(sketch, "E1215", {"start": v(29.27, 95.99) * mm, "end": v(30.33, 95.56) * mm});
            skLineSegment(sketch, "E1216", {"start": v(30.33, 95.56) * mm, "end": v(30.63, 95.89) * mm});
            skLineSegment(sketch, "E1217", {"start": v(30.63, 95.89) * mm, "end": v(31.23, 96.55) * mm});
            skLineSegment(sketch, "E1218", {"start": v(31.23, 96.55) * mm, "end": v(31.54, 96.87) * mm});
            skLineSegment(sketch, "E1219", {"start": v(31.54, 96.87) * mm, "end": v(32.58, 96.43) * mm});
            skLineSegment(sketch, "E1220", {"start": v(32.58, 96.43) * mm, "end": v(32.56, 95.98) * mm});
            skLineSegment(sketch, "E1221", {"start": v(32.56, 95.98) * mm, "end": v(32.5, 95.1) * mm});
            skLineSegment(sketch, "E1222", {"start": v(32.5, 95.1) * mm, "end": v(32.47, 94.65) * mm});
            skLineSegment(sketch, "E1223", {"start": v(32.47, 94.65) * mm, "end": v(33.52, 94.18) * mm});
            skLineSegment(sketch, "E1224", {"start": v(33.52, 94.18) * mm, "end": v(33.83, 94.5) * mm});
            skLineSegment(sketch, "E1225", {"start": v(33.83, 94.5) * mm, "end": v(34.45, 95.14) * mm});
            skLineSegment(sketch, "E1226", {"start": v(34.45, 95.14) * mm, "end": v(34.77, 95.46) * mm});
            skLineSegment(sketch, "E1227", {"start": v(34.77, 95.46) * mm, "end": v(35.8, 94.98) * mm});
            skLineSegment(sketch, "E1228", {"start": v(35.8, 94.98) * mm, "end": v(35.76, 94.53) * mm});
            skLineSegment(sketch, "E1229", {"start": v(35.76, 94.53) * mm, "end": v(35.68, 93.64) * mm});
            skLineSegment(sketch, "E1230", {"start": v(35.68, 93.64) * mm, "end": v(35.63, 93.2) * mm});
            skLineSegment(sketch, "E1231", {"start": v(35.63, 93.2) * mm, "end": v(36.66, 92.7) * mm});
            skLineSegment(sketch, "E1232", {"start": v(36.66, 92.7) * mm, "end": v(36.98, 93.01) * mm});
            skLineSegment(sketch, "E1233", {"start": v(36.98, 93.01) * mm, "end": v(37.62, 93.63) * mm});
            skLineSegment(sketch, "E1234", {"start": v(37.62, 93.63) * mm, "end": v(37.95, 93.93) * mm});
            skLineSegment(sketch, "E1235", {"start": v(37.95, 93.93) * mm, "end": v(38.96, 93.42) * mm});
            skLineSegment(sketch, "E1236", {"start": v(38.96, 93.42) * mm, "end": v(38.91, 92.98) * mm});
            skLineSegment(sketch, "E1237", {"start": v(38.91, 92.98) * mm, "end": v(38.8, 92.09) * mm});
            skLineSegment(sketch, "E1238", {"start": v(38.8, 92.09) * mm, "end": v(38.73, 91.65) * mm});
            skLineSegment(sketch, "E1239", {"start": v(38.73, 91.65) * mm, "end": v(39.75, 91.11) * mm});
            skLineSegment(sketch, "E1240", {"start": v(39.75, 91.11) * mm, "end": v(40.08, 91.42) * mm});
            skLineSegment(sketch, "E1241", {"start": v(40.08, 91.42) * mm, "end": v(40.74, 92.01) * mm});
            skLineSegment(sketch, "E1242", {"start": v(40.74, 92.01) * mm, "end": v(41.08, 92.3) * mm});
            skLineSegment(sketch, "E1243", {"start": v(41.08, 92.3) * mm, "end": v(42.07, 91.76) * mm});
            skLineSegment(sketch, "E1244", {"start": v(42.07, 91.76) * mm, "end": v(42, 91.31) * mm});
            skLineSegment(sketch, "E1245", {"start": v(42, 91.31) * mm, "end": v(41.87, 90.43) * mm});
            skLineSegment(sketch, "E1246", {"start": v(41.87, 90.43) * mm, "end": v(41.79, 90) * mm});
            skLineSegment(sketch, "E1247", {"start": v(41.79, 90) * mm, "end": v(42.78, 89.43) * mm});
            skLineSegment(sketch, "E1248", {"start": v(42.78, 89.43) * mm, "end": v(43.12, 89.72) * mm});
            skLineSegment(sketch, "E1249", {"start": v(43.12, 89.72) * mm, "end": v(43.8, 90.29) * mm});
            skLineSegment(sketch, "E1250", {"start": v(43.8, 90.29) * mm, "end": v(44.16, 90.57) * mm});
            skLineSegment(sketch, "E1251", {"start": v(44.16, 90.57) * mm, "end": v(45.13, 90) * mm});
            skLineSegment(sketch, "E1252", {"start": v(45.13, 90) * mm, "end": v(45.05, 89.55) * mm});
            skLineSegment(sketch, "E1253", {"start": v(45.05, 89.55) * mm, "end": v(44.87, 88.67) * mm});
            skLineSegment(sketch, "E1254", {"start": v(44.87, 88.67) * mm, "end": v(44.78, 88.24) * mm});
            skLineSegment(sketch, "E1255", {"start": v(44.78, 88.24) * mm, "end": v(45.76, 87.64) * mm});
            skLineSegment(sketch, "E1256", {"start": v(45.76, 87.64) * mm, "end": v(46.1, 87.92) * mm});
            skLineSegment(sketch, "E1257", {"start": v(46.1, 87.92) * mm, "end": v(46.8, 88.46) * mm});
            skLineSegment(sketch, "E1258", {"start": v(46.8, 88.46) * mm, "end": v(47.17, 88.73) * mm});
            skLineSegment(sketch, "E1259", {"start": v(47.17, 88.73) * mm, "end": v(48.12, 88.12) * mm});
            skLineSegment(sketch, "E1260", {"start": v(48.12, 88.12) * mm, "end": v(48.03, 87.68) * mm});
            skLineSegment(sketch, "E1261", {"start": v(48.03, 87.68) * mm, "end": v(47.82, 86.81) * mm});
            skLineSegment(sketch, "E1262", {"start": v(47.82, 86.81) * mm, "end": v(47.71, 86.38) * mm});
            skLineSegment(sketch, "E1263", {"start": v(47.71, 86.38) * mm, "end": v(48.67, 85.75) * mm});
            skLineSegment(sketch, "E1264", {"start": v(48.67, 85.75) * mm, "end": v(49.03, 86.02) * mm});
            skLineSegment(sketch, "E1265", {"start": v(49.03, 86.02) * mm, "end": v(49.75, 86.54) * mm});
            skLineSegment(sketch, "E1266", {"start": v(49.75, 86.54) * mm, "end": v(50.12, 86.8) * mm});
            skLineSegment(sketch, "E1267", {"start": v(50.12, 86.8) * mm, "end": v(51.05, 86.16) * mm});
            skLineSegment(sketch, "E1268", {"start": v(51.05, 86.16) * mm, "end": v(50.94, 85.72) * mm});
            skLineSegment(sketch, "E1269", {"start": v(50.94, 85.72) * mm, "end": v(50.7, 84.86) * mm});
            skLineSegment(sketch, "E1270", {"start": v(50.7, 84.86) * mm, "end": v(50.58, 84.43) * mm});
            skLineSegment(sketch, "E1271", {"start": v(50.58, 84.43) * mm, "end": v(51.52, 83.76) * mm});
            skLineSegment(sketch, "E1272", {"start": v(51.52, 83.76) * mm, "end": v(51.88, 84.02) * mm});
            skLineSegment(sketch, "E1273", {"start": v(51.88, 84.02) * mm, "end": v(52.62, 84.52) * mm});
            skLineSegment(sketch, "E1274", {"start": v(52.62, 84.52) * mm, "end": v(53, 84.76) * mm});
            skLineSegment(sketch, "E1275", {"start": v(53, 84.76) * mm, "end": v(53.9, 84.1) * mm});
            skLineSegment(sketch, "E1276", {"start": v(53.9, 84.1) * mm, "end": v(53.79, 83.66) * mm});
            skLineSegment(sketch, "E1277", {"start": v(53.79, 83.66) * mm, "end": v(53.52, 82.8) * mm});
            skLineSegment(sketch, "E1278", {"start": v(53.52, 82.8) * mm, "end": v(53.39, 82.38) * mm});
            skLineSegment(sketch, "E1279", {"start": v(53.39, 82.38) * mm, "end": v(54.3, 81.68) * mm});
            skLineSegment(sketch, "E1280", {"start": v(54.3, 81.68) * mm, "end": v(54.67, 81.93) * mm});
            skLineSegment(sketch, "E1281", {"start": v(54.67, 81.93) * mm, "end": v(55.43, 82.4) * mm});
            skLineSegment(sketch, "E1282", {"start": v(55.43, 82.4) * mm, "end": v(55.81, 82.63) * mm});
            skLineSegment(sketch, "E1283", {"start": v(55.81, 82.63) * mm, "end": v(56.7, 81.93) * mm});
            skLineSegment(sketch, "E1284", {"start": v(56.7, 81.93) * mm, "end": v(56.56, 81.5) * mm});
            skLineSegment(sketch, "E1285", {"start": v(56.56, 81.5) * mm, "end": v(56.27, 80.66) * mm});
            skLineSegment(sketch, "E1286", {"start": v(56.27, 80.66) * mm, "end": v(56.12, 80.24) * mm});
            skLineSegment(sketch, "E1287", {"start": v(56.12, 80.24) * mm, "end": v(57, 79.51) * mm});
            skLineSegment(sketch, "E1288", {"start": v(57, 79.51) * mm, "end": v(57.39, 79.74) * mm});
            skLineSegment(sketch, "E1289", {"start": v(57.39, 79.74) * mm, "end": v(58.16, 80.2) * mm});
            skLineSegment(sketch, "E1290", {"start": v(58.16, 80.2) * mm, "end": v(58.55, 80.41) * mm});
            skLineSegment(sketch, "E1291", {"start": v(58.55, 80.41) * mm, "end": v(59.41, 79.68) * mm});
            skLineSegment(sketch, "E1292", {"start": v(59.41, 79.68) * mm, "end": v(59.26, 79.26) * mm});
            skLineSegment(sketch, "E1293", {"start": v(59.26, 79.26) * mm, "end": v(58.94, 78.42) * mm});
            skLineSegment(sketch, "E1294", {"start": v(58.94, 78.42) * mm, "end": v(58.78, 78) * mm});
            skLineSegment(sketch, "E1295", {"start": v(58.78, 78) * mm, "end": v(59.64, 77.25) * mm});
            skLineSegment(sketch, "E1296", {"start": v(59.64, 77.25) * mm, "end": v(60.03, 77.47) * mm});
            skLineSegment(sketch, "E1297", {"start": v(60.03, 77.47) * mm, "end": v(60.82, 77.9) * mm});
            skLineSegment(sketch, "E1298", {"start": v(60.82, 77.9) * mm, "end": v(61.22, 78.1) * mm});
            skLineSegment(sketch, "E1299", {"start": v(61.22, 78.1) * mm, "end": v(62.05, 77.34) * mm});
            skLineSegment(sketch, "E1300", {"start": v(62.05, 77.34) * mm, "end": v(61.89, 76.92) * mm});
            skLineSegment(sketch, "E1301", {"start": v(61.89, 76.92) * mm, "end": v(61.54, 76.1) * mm});
            skLineSegment(sketch, "E1302", {"start": v(61.54, 76.1) * mm, "end": v(61.36, 75.69) * mm});
            skLineSegment(sketch, "E1303", {"start": v(61.36, 75.69) * mm, "end": v(62.2, 74.9) * mm});
            skLineSegment(sketch, "E1304", {"start": v(62.2, 74.9) * mm, "end": v(62.6, 75.1) * mm});
            skLineSegment(sketch, "E1305", {"start": v(62.6, 75.1) * mm, "end": v(63.4, 75.5) * mm});
            skLineSegment(sketch, "E1306", {"start": v(63.4, 75.5) * mm, "end": v(63.8, 75.7) * mm});
            skLineSegment(sketch, "E1307", {"start": v(63.8, 75.7) * mm, "end": v(64.6, 74.9) * mm});
            skLineSegment(sketch, "E1308", {"start": v(64.6, 74.9) * mm, "end": v(64.43, 74.5) * mm});
            skLineSegment(sketch, "E1309", {"start": v(64.43, 74.5) * mm, "end": v(64.06, 73.68) * mm});
            skLineSegment(sketch, "E1310", {"start": v(64.06, 73.68) * mm, "end": v(63.86, 73.28) * mm});
            skLineSegment(sketch, "E1311", {"start": v(63.86, 73.28) * mm, "end": v(64.67, 72.47) * mm});
            skLineSegment(sketch, "E1312", {"start": v(64.67, 72.47) * mm, "end": v(65.07, 72.66) * mm});
            skLineSegment(sketch, "E1313", {"start": v(65.07, 72.66) * mm, "end": v(65.89, 73.03) * mm});
            skLineSegment(sketch, "E1314", {"start": v(65.89, 73.03) * mm, "end": v(66.3, 73.2) * mm});
            skLineSegment(sketch, "E1315", {"start": v(66.3, 73.2) * mm, "end": v(67.08, 72.4) * mm});
            skLineSegment(sketch, "E1316", {"start": v(67.08, 72.4) * mm, "end": v(66.9, 71.99) * mm});
            skLineSegment(sketch, "E1317", {"start": v(66.9, 71.99) * mm, "end": v(66.5, 71.19) * mm});
            skLineSegment(sketch, "E1318", {"start": v(66.5, 71.19) * mm, "end": v(66.28, 70.8) * mm});
            skLineSegment(sketch, "E1319", {"start": v(66.28, 70.8) * mm, "end": v(67.07, 69.95) * mm});
            skLineSegment(sketch, "E1320", {"start": v(67.07, 69.95) * mm, "end": v(67.47, 70.13) * mm});
            skLineSegment(sketch, "E1321", {"start": v(67.47, 70.13) * mm, "end": v(68.3, 70.47) * mm});
            skLineSegment(sketch, "E1322", {"start": v(68.3, 70.47) * mm, "end": v(68.72, 70.64) * mm});
            skLineSegment(sketch, "E1323", {"start": v(68.72, 70.64) * mm, "end": v(69.47, 69.8) * mm});
            skLineSegment(sketch, "E1324", {"start": v(69.47, 69.8) * mm, "end": v(69.27, 69.4) * mm});
            skLineSegment(sketch, "E1325", {"start": v(69.27, 69.4) * mm, "end": v(68.84, 68.61) * mm});
            skLineSegment(sketch, "E1326", {"start": v(68.84, 68.61) * mm, "end": v(68.62, 68.23) * mm});
            skLineSegment(sketch, "E1327", {"start": v(68.62, 68.23) * mm, "end": v(69.37, 67.36) * mm});
            skLineSegment(sketch, "E1328", {"start": v(69.37, 67.36) * mm, "end": v(69.79, 67.52) * mm});
            skLineSegment(sketch, "E1329", {"start": v(69.79, 67.52) * mm, "end": v(70.62, 67.84) * mm});
            skLineSegment(sketch, "E1330", {"start": v(70.62, 67.84) * mm, "end": v(71.05, 67.99) * mm});
            skLineSegment(sketch, "E1331", {"start": v(71.05, 67.99) * mm, "end": v(71.77, 67.12) * mm});
            skLineSegment(sketch, "E1332", {"start": v(71.77, 67.12) * mm, "end": v(71.55, 66.73) * mm});
            skLineSegment(sketch, "E1333", {"start": v(71.55, 66.73) * mm, "end": v(71.1, 65.96) * mm});
            skLineSegment(sketch, "E1334", {"start": v(71.1, 65.96) * mm, "end": v(70.87, 65.58) * mm});
            skLineSegment(sketch, "E1335", {"start": v(70.87, 65.58) * mm, "end": v(71.6, 64.69) * mm});
            skLineSegment(sketch, "E1336", {"start": v(71.6, 64.69) * mm, "end": v(72.01, 64.84) * mm});
            skLineSegment(sketch, "E1337", {"start": v(72.01, 64.84) * mm, "end": v(72.86, 65.12) * mm});
            skLineSegment(sketch, "E1338", {"start": v(72.86, 65.12) * mm, "end": v(73.29, 65.26) * mm});
            skLineSegment(sketch, "E1339", {"start": v(73.29, 65.26) * mm, "end": v(73.98, 64.37) * mm});
            skLineSegment(sketch, "E1340", {"start": v(73.98, 64.37) * mm, "end": v(73.75, 63.99) * mm});
            skLineSegment(sketch, "E1341", {"start": v(73.75, 63.99) * mm, "end": v(73.27, 63.23) * mm});
            skLineSegment(sketch, "E1342", {"start": v(73.27, 63.23) * mm, "end": v(73.03, 62.86) * mm});
            skLineSegment(sketch, "E1343", {"start": v(73.03, 62.86) * mm, "end": v(73.72, 61.95) * mm});
            skLineSegment(sketch, "E1344", {"start": v(73.72, 61.95) * mm, "end": v(74.14, 62.08) * mm});
            skLineSegment(sketch, "E1345", {"start": v(74.14, 62.08) * mm, "end": v(75, 62.34) * mm});
            skLineSegment(sketch, "E1346", {"start": v(75, 62.34) * mm, "end": v(75.43, 62.46) * mm});
            skLineSegment(sketch, "E1347", {"start": v(75.43, 62.46) * mm, "end": v(76.1, 61.55) * mm});
            skLineSegment(sketch, "E1348", {"start": v(76.1, 61.55) * mm, "end": v(75.85, 61.17) * mm});
            skLineSegment(sketch, "E1349", {"start": v(75.85, 61.17) * mm, "end": v(75.35, 60.43) * mm});
            skLineSegment(sketch, "E1350", {"start": v(75.35, 60.43) * mm, "end": v(75.1, 60.07) * mm});
            skLineSegment(sketch, "E1351", {"start": v(75.1, 60.07) * mm, "end": v(75.76, 59.13) * mm});
            skLineSegment(sketch, "E1352", {"start": v(75.76, 59.13) * mm, "end": v(76.18, 59.25) * mm});
            skLineSegment(sketch, "E1353", {"start": v(76.18, 59.25) * mm, "end": v(77.05, 59.48) * mm});
            skLineSegment(sketch, "E1354", {"start": v(77.05, 59.48) * mm, "end": v(77.48, 59.59) * mm});
            skLineSegment(sketch, "E1355", {"start": v(77.48, 59.59) * mm, "end": v(78.12, 58.65) * mm});
            skLineSegment(sketch, "E1356", {"start": v(78.12, 58.65) * mm, "end": v(77.86, 58.29) * mm});
            skLineSegment(sketch, "E1357", {"start": v(77.86, 58.29) * mm, "end": v(77.33, 57.57) * mm});
            skLineSegment(sketch, "E1358", {"start": v(77.33, 57.57) * mm, "end": v(77.06, 57.21) * mm});
            skLineSegment(sketch, "E1359", {"start": v(77.06, 57.21) * mm, "end": v(77.7, 56.25) * mm});
            skLineSegment(sketch, "E1360", {"start": v(77.7, 56.25) * mm, "end": v(78.12, 56.36) * mm});
            skLineSegment(sketch, "E1361", {"start": v(78.12, 56.36) * mm, "end": v(79, 56.56) * mm});
            skLineSegment(sketch, "E1362", {"start": v(79, 56.56) * mm, "end": v(79.44, 56.65) * mm});
            skLineSegment(sketch, "E1363", {"start": v(79.44, 56.65) * mm, "end": v(80.04, 55.7) * mm});
            skLineSegment(sketch, "E1364", {"start": v(80.04, 55.7) * mm, "end": v(79.77, 55.34) * mm});
            skLineSegment(sketch, "E1365", {"start": v(79.77, 55.34) * mm, "end": v(79.22, 54.63) * mm});
            skLineSegment(sketch, "E1366", {"start": v(79.22, 54.63) * mm, "end": v(78.94, 54.3) * mm});
            skLineSegment(sketch, "E1367", {"start": v(78.94, 54.3) * mm, "end": v(79.53, 53.3) * mm});
            skLineSegment(sketch, "E1368", {"start": v(79.53, 53.3) * mm, "end": v(79.97, 53.4) * mm});
            skLineSegment(sketch, "E1369", {"start": v(79.97, 53.4) * mm, "end": v(80.85, 53.57) * mm});
            skLineSegment(sketch, "E1370", {"start": v(80.85, 53.57) * mm, "end": v(81.29, 53.65) * mm});
            skLineSegment(sketch, "E1371", {"start": v(81.29, 53.65) * mm, "end": v(81.86, 52.67) * mm});
            skLineSegment(sketch, "E1372", {"start": v(81.86, 52.67) * mm, "end": v(81.58, 52.32) * mm});
            skLineSegment(sketch, "E1373", {"start": v(81.58, 52.32) * mm, "end": v(81, 51.64) * mm});
            skLineSegment(sketch, "E1374", {"start": v(81, 51.64) * mm, "end": v(80.71, 51.3) * mm});
            skLineSegment(sketch, "E1375", {"start": v(80.71, 51.3) * mm, "end": v(81.28, 50.3) * mm});
            skLineSegment(sketch, "E1376", {"start": v(81.28, 50.3) * mm, "end": v(81.71, 50.38) * mm});
            skLineSegment(sketch, "E1377", {"start": v(81.71, 50.38) * mm, "end": v(82.6, 50.52) * mm});
            skLineSegment(sketch, "E1378", {"start": v(82.6, 50.52) * mm, "end": v(83.04, 50.59) * mm});
            skLineSegment(sketch, "E1379", {"start": v(83.04, 50.59) * mm, "end": v(83.58, 49.6) * mm});
            skLineSegment(sketch, "E1380", {"start": v(83.58, 49.6) * mm, "end": v(83.29, 49.25) * mm});
            skLineSegment(sketch, "E1381", {"start": v(83.29, 49.25) * mm, "end": v(82.69, 48.59) * mm});
            skLineSegment(sketch, "E1382", {"start": v(82.69, 48.59) * mm, "end": v(82.38, 48.26) * mm});
            skLineSegment(sketch, "E1383", {"start": v(82.38, 48.26) * mm, "end": v(82.91, 47.25) * mm});
            skLineSegment(sketch, "E1384", {"start": v(82.91, 47.25) * mm, "end": v(83.35, 47.3) * mm});
            skLineSegment(sketch, "E1385", {"start": v(83.35, 47.3) * mm, "end": v(84.24, 47.42) * mm});
            skLineSegment(sketch, "E1386", {"start": v(84.24, 47.42) * mm, "end": v(84.69, 47.47) * mm});
            skLineSegment(sketch, "E1387", {"start": v(84.69, 47.47) * mm, "end": v(85.2, 46.46) * mm});
            skLineSegment(sketch, "E1388", {"start": v(85.2, 46.46) * mm, "end": v(84.89, 46.13) * mm});
            skLineSegment(sketch, "E1389", {"start": v(84.89, 46.13) * mm, "end": v(84.27, 45.48) * mm});
            skLineSegment(sketch, "E1390", {"start": v(84.27, 45.48) * mm, "end": v(83.95, 45.17) * mm});
            skLineSegment(sketch, "E1391", {"start": v(83.95, 45.17) * mm, "end": v(84.45, 44.13) * mm});
            skLineSegment(sketch, "E1392", {"start": v(84.45, 44.13) * mm, "end": v(84.9, 44.18) * mm});
            skLineSegment(sketch, "E1393", {"start": v(84.9, 44.18) * mm, "end": v(85.78, 44.26) * mm});
            skLineSegment(sketch, "E1394", {"start": v(85.78, 44.26) * mm, "end": v(86.23, 44.3) * mm});
            skLineSegment(sketch, "E1395", {"start": v(86.23, 44.3) * mm, "end": v(86.7, 43.27) * mm});
            skLineSegment(sketch, "E1396", {"start": v(86.7, 43.27) * mm, "end": v(86.38, 42.95) * mm});
            skLineSegment(sketch, "E1397", {"start": v(86.38, 42.95) * mm, "end": v(85.74, 42.32) * mm});
            skLineSegment(sketch, "E1398", {"start": v(85.74, 42.32) * mm, "end": v(85.42, 42.02) * mm});
            skLineSegment(sketch, "E1399", {"start": v(85.42, 42.02) * mm, "end": v(85.88, 40.97) * mm});
            skLineSegment(sketch, "E1400", {"start": v(85.88, 40.97) * mm, "end": v(86.32, 41) * mm});
            skLineSegment(sketch, "E1401", {"start": v(86.32, 41) * mm, "end": v(87.22, 41.05) * mm});
            skLineSegment(sketch, "E1402", {"start": v(87.22, 41.05) * mm, "end": v(87.66, 41.07) * mm});
            skLineSegment(sketch, "E1403", {"start": v(87.66, 41.07) * mm, "end": v(88.1, 40.03) * mm});
            skLineSegment(sketch, "E1404", {"start": v(88.1, 40.03) * mm, "end": v(87.77, 39.72) * mm});
            skLineSegment(sketch, "E1405", {"start": v(87.77, 39.72) * mm, "end": v(87.11, 39.12) * mm});
            skLineSegment(sketch, "E1406", {"start": v(87.11, 39.12) * mm, "end": v(86.78, 38.83) * mm});
            skLineSegment(sketch, "E1407", {"start": v(86.78, 38.83) * mm, "end": v(87.2, 37.76) * mm});
            skLineSegment(sketch, "E1408", {"start": v(87.2, 37.76) * mm, "end": v(87.65, 37.78) * mm});
            skLineSegment(sketch, "E1409", {"start": v(87.65, 37.78) * mm, "end": v(88.54, 37.8) * mm});
            skLineSegment(sketch, "E1410", {"start": v(88.54, 37.8) * mm, "end": v(88.99, 37.8) * mm});
            skLineSegment(sketch, "E1411", {"start": v(88.99, 37.8) * mm, "end": v(89.4, 36.74) * mm});
            skLineSegment(sketch, "E1412", {"start": v(89.4, 36.74) * mm, "end": v(89.05, 36.45) * mm});
            skLineSegment(sketch, "E1413", {"start": v(89.05, 36.45) * mm, "end": v(88.37, 35.87) * mm});
            skLineSegment(sketch, "E1414", {"start": v(88.37, 35.87) * mm, "end": v(88.03, 35.59) * mm});
            skLineSegment(sketch, "E1415", {"start": v(88.03, 35.59) * mm, "end": v(88.42, 34.5) * mm});
            skLineSegment(sketch, "E1416", {"start": v(88.42, 34.5) * mm, "end": v(88.86, 34.51) * mm});
            skLineSegment(sketch, "E1417", {"start": v(88.86, 34.51) * mm, "end": v(89.75, 34.5) * mm});
            skLineSegment(sketch, "E1418", {"start": v(89.75, 34.5) * mm, "end": v(90.2, 34.49) * mm});
            skLineSegment(sketch, "E1419", {"start": v(90.2, 34.49) * mm, "end": v(90.57, 33.42) * mm});
            skLineSegment(sketch, "E1420", {"start": v(90.57, 33.42) * mm, "end": v(90.22, 33.13) * mm});
            skLineSegment(sketch, "E1421", {"start": v(90.22, 33.13) * mm, "end": v(89.52, 32.58) * mm});
            skLineSegment(sketch, "E1422", {"start": v(89.52, 32.58) * mm, "end": v(89.17, 32.3) * mm});
            skLineSegment(sketch, "E1423", {"start": v(89.17, 32.3) * mm, "end": v(89.52, 31.22) * mm});
            skLineSegment(sketch, "E1424", {"start": v(89.52, 31.22) * mm, "end": v(89.97, 31.2) * mm});
            skLineSegment(sketch, "E1425", {"start": v(89.97, 31.2) * mm, "end": v(90.86, 31.16) * mm});
            skLineSegment(sketch, "E1426", {"start": v(90.86, 31.16) * mm, "end": v(91.3, 31.14) * mm});
            skLineSegment(sketch, "E1427", {"start": v(91.3, 31.14) * mm, "end": v(91.64, 30.05) * mm});
            skLineSegment(sketch, "E1428", {"start": v(91.64, 30.05) * mm, "end": v(91.28, 29.78) * mm});
            skLineSegment(sketch, "E1429", {"start": v(91.28, 29.78) * mm, "end": v(90.56, 29.25) * mm});
            skLineSegment(sketch, "E1430", {"start": v(90.56, 29.25) * mm, "end": v(90.2, 29) * mm});
            skLineSegment(sketch, "E1431", {"start": v(90.2, 29) * mm, "end": v(90.51, 27.89) * mm});
            skLineSegment(sketch, "E1432", {"start": v(90.51, 27.89) * mm, "end": v(90.96, 27.86) * mm});
            skLineSegment(sketch, "E1433", {"start": v(90.96, 27.86) * mm, "end": v(91.85, 27.8) * mm});
            skLineSegment(sketch, "E1434", {"start": v(91.85, 27.8) * mm, "end": v(92.3, 27.75) * mm});
            skLineSegment(sketch, "E1435", {"start": v(92.3, 27.75) * mm, "end": v(92.59, 26.66) * mm});
            skLineSegment(sketch, "E1436", {"start": v(92.59, 26.66) * mm, "end": v(92.22, 26.4) * mm});
            skLineSegment(sketch, "E1437", {"start": v(92.22, 26.4) * mm, "end": v(91.49, 25.89) * mm});
            skLineSegment(sketch, "E1438", {"start": v(91.49, 25.89) * mm, "end": v(91.12, 25.65) * mm});
            skLineSegment(sketch, "E1439", {"start": v(91.12, 25.65) * mm, "end": v(91.4, 24.53) * mm});
            skLineSegment(sketch, "E1440", {"start": v(91.4, 24.53) * mm, "end": v(91.84, 24.49) * mm});
            skLineSegment(sketch, "E1441", {"start": v(91.84, 24.49) * mm, "end": v(92.73, 24.39) * mm});
            skLineSegment(sketch, "E1442", {"start": v(92.73, 24.39) * mm, "end": v(93.17, 24.33) * mm});
            skLineSegment(sketch, "E1443", {"start": v(93.17, 24.33) * mm, "end": v(93.43, 23.23) * mm});
            skLineSegment(sketch, "E1444", {"start": v(93.43, 23.23) * mm, "end": v(93.05, 22.98) * mm});
            skLineSegment(sketch, "E1445", {"start": v(93.05, 22.98) * mm, "end": v(92.3, 22.5) * mm});
            skLineSegment(sketch, "E1446", {"start": v(92.3, 22.5) * mm, "end": v(91.92, 22.27) * mm});
            skLineSegment(sketch, "E1447", {"start": v(91.92, 22.27) * mm, "end": v(92.16, 21.15) * mm});
            skLineSegment(sketch, "E1448", {"start": v(92.16, 21.15) * mm, "end": v(92.6, 21.09) * mm});
            skLineSegment(sketch, "E1449", {"start": v(92.6, 21.09) * mm, "end": v(93.49, 20.96) * mm});
            skLineSegment(sketch, "E1450", {"start": v(93.49, 20.96) * mm, "end": v(93.93, 20.89) * mm});
            skLineSegment(sketch, "E1451", {"start": v(93.93, 20.89) * mm, "end": v(94.15, 19.78) * mm});
            skLineSegment(sketch, "E1452", {"start": v(94.15, 19.78) * mm, "end": v(93.77, 19.54) * mm});
            skLineSegment(sketch, "E1453", {"start": v(93.77, 19.54) * mm, "end": v(93, 19.09) * mm});
            skLineSegment(sketch, "E1454", {"start": v(93, 19.09) * mm, "end": v(92.61, 18.87) * mm});
            skLineSegment(sketch, "E1455", {"start": v(92.61, 18.87) * mm, "end": v(92.82, 17.74) * mm});
            skLineSegment(sketch, "E1456", {"start": v(92.82, 17.74) * mm, "end": v(93.25, 17.66) * mm});
            skLineSegment(sketch, "E1457", {"start": v(93.25, 17.66) * mm, "end": v(94.13, 17.5) * mm});
            skLineSegment(sketch, "E1458", {"start": v(94.13, 17.5) * mm, "end": v(94.57, 17.42) * mm});
            skLineSegment(sketch, "E1459", {"start": v(94.57, 17.42) * mm, "end": v(94.76, 16.3) * mm});
            skLineSegment(sketch, "E1460", {"start": v(94.76, 16.3) * mm, "end": v(94.37, 16.08) * mm});
            skLineSegment(sketch, "E1461", {"start": v(94.37, 16.08) * mm, "end": v(93.58, 15.65) * mm});
            skLineSegment(sketch, "E1462", {"start": v(93.58, 15.65) * mm, "end": v(93.19, 15.44) * mm});
            skLineSegment(sketch, "E1463", {"start": v(93.19, 15.44) * mm, "end": v(93.35, 14.3) * mm});
            skLineSegment(sketch, "E1464", {"start": v(93.35, 14.3) * mm, "end": v(93.8, 14.22) * mm});
            skLineSegment(sketch, "E1465", {"start": v(93.8, 14.22) * mm, "end": v(94.66, 14.03) * mm});
            skLineSegment(sketch, "E1466", {"start": v(94.66, 14.03) * mm, "end": v(95.1, 13.93) * mm});
            skLineSegment(sketch, "E1467", {"start": v(95.1, 13.93) * mm, "end": v(95.25, 12.8) * mm});
            skLineSegment(sketch, "E1468", {"start": v(95.25, 12.8) * mm, "end": v(94.85, 12.6) * mm});
            skLineSegment(sketch, "E1469", {"start": v(94.85, 12.6) * mm, "end": v(94.05, 12.2) * mm});
            skLineSegment(sketch, "E1470", {"start": v(94.05, 12.2) * mm, "end": v(93.65, 12) * mm});
            skLineSegment(sketch, "E1471", {"start": v(93.65, 12) * mm, "end": v(93.78, 10.86) * mm});
            skLineSegment(sketch, "E1472", {"start": v(93.78, 10.86) * mm, "end": v(94.21, 10.76) * mm});
            skLineSegment(sketch, "E1473", {"start": v(94.21, 10.76) * mm, "end": v(95.08, 10.54) * mm});
            skLineSegment(sketch, "E1474", {"start": v(95.08, 10.54) * mm, "end": v(95.51, 10.42) * mm});
            skLineSegment(sketch, "E1475", {"start": v(95.51, 10.42) * mm, "end": v(95.62, 9.3) * mm});
            skLineSegment(sketch, "E1476", {"start": v(95.62, 9.3) * mm, "end": v(95.21, 9.1) * mm});
            skLineSegment(sketch, "E1477", {"start": v(95.21, 9.1) * mm, "end": v(94.4, 8.73) * mm});
            skLineSegment(sketch, "E1478", {"start": v(94.4, 8.73) * mm, "end": v(94, 8.55) * mm});
            skLineSegment(sketch, "E1479", {"start": v(94, 8.55) * mm, "end": v(94.08, 7.4) * mm});
            skLineSegment(sketch, "E1480", {"start": v(94.08, 7.4) * mm, "end": v(94.51, 7.29) * mm});
            skLineSegment(sketch, "E1481", {"start": v(94.51, 7.29) * mm, "end": v(95.37, 7.04) * mm});
            skLineSegment(sketch, "E1482", {"start": v(95.37, 7.04) * mm, "end": v(95.8, 6.9) * mm});
            skLineSegment(sketch, "E1483", {"start": v(95.8, 6.9) * mm, "end": v(95.87, 5.78) * mm});
            skLineSegment(sketch, "E1484", {"start": v(95.87, 5.78) * mm, "end": v(95.46, 5.6) * mm});
            skLineSegment(sketch, "E1485", {"start": v(95.46, 5.6) * mm, "end": v(94.64, 5.25) * mm});
            skLineSegment(sketch, "E1486", {"start": v(94.64, 5.25) * mm, "end": v(94.22, 5.08) * mm});
            skLineSegment(sketch, "E1487", {"start": v(94.22, 5.08) * mm, "end": v(94.28, 3.94) * mm});
            skLineSegment(sketch, "E1488", {"start": v(94.28, 3.94) * mm, "end": v(94.7, 3.8) * mm});
            skLineSegment(sketch, "E1489", {"start": v(94.7, 3.8) * mm, "end": v(95.55, 3.53) * mm});
            skLineSegment(sketch, "E1490", {"start": v(95.55, 3.53) * mm, "end": v(95.97, 3.38) * mm});
            skLineSegment(sketch, "E1491", {"start": v(95.97, 3.38) * mm, "end": v(96, 2.26) * mm});
            skLineSegment(sketch, "E1492", {"start": v(96, 2.26) * mm, "end": v(95.59, 2.09) * mm});
            skLineSegment(sketch, "E1493", {"start": v(95.59, 2.09) * mm, "end": v(94.75, 1.77) * mm});
            skLineSegment(sketch, "E1494", {"start": v(94.75, 1.77) * mm, "end": v(94.34, 1.61) * mm});
            skLineSegment(sketch, "E1495", {"start": v(94.34, 1.61) * mm, "end": v(94.35, 0.47) * mm});
            skLineSegment(sketch, "E1496", {"start": v(13.9, 6.14) * mm, "end": v(81.58, 5.69) * mm});
            skLineSegment(sketch, "E1497", {"start": v(81.58, 5.69) * mm, "end": v(84.48, 8.82) * mm});
            skLineSegment(sketch, "E1498", {"start": v(84.48, 8.82) * mm, "end": v(83.63, 15.38) * mm});
            skLineSegment(sketch, "E1499", {"start": v(83.63, 15.38) * mm, "end": v(82.32, 21.86) * mm});
            skLineSegment(sketch, "E1500", {"start": v(82.32, 21.86) * mm, "end": v(80.55, 28.23) * mm});
            skLineSegment(sketch, "E1501", {"start": v(80.55, 28.23) * mm, "end": v(78.34, 34.47) * mm});
            skLineSegment(sketch, "E1502", {"start": v(78.34, 34.47) * mm, "end": v(75.7, 40.53) * mm});
            skLineSegment(sketch, "E1503", {"start": v(75.7, 40.53) * mm, "end": v(72.64, 46.39) * mm});
            skLineSegment(sketch, "E1504", {"start": v(72.64, 46.39) * mm, "end": v(69.17, 52.02) * mm});
            skLineSegment(sketch, "E1505", {"start": v(69.17, 52.02) * mm, "end": v(65.31, 57.4) * mm});
            skLineSegment(sketch, "E1506", {"start": v(65.31, 57.4) * mm, "end": v(61.09, 62.48) * mm});
            skLineSegment(sketch, "E1507", {"start": v(61.09, 62.48) * mm, "end": v(56.51, 67.26) * mm});
            skLineSegment(sketch, "E1508", {"start": v(56.51, 67.26) * mm, "end": v(51.62, 71.7) * mm});
            skLineSegment(sketch, "E1509", {"start": v(51.62, 71.7) * mm, "end": v(46.42, 75.79) * mm});
            skLineSegment(sketch, "E1510", {"start": v(46.42, 75.79) * mm, "end": v(42.24, 74.9) * mm});
            skLineSegment(sketch, "E1511", {"start": v(42.24, 74.9) * mm, "end": v(8, 16.5) * mm});
            skLineSegment(sketch, "E1512", {"start": v(8, 16.5) * mm, "end": v(8.47, 11.07) * mm});
            skLineSegment(sketch, "E1513", {"start": v(8.47, 11.07) * mm, "end": v(13.9, 6.14) * mm});
            skLineSegment(sketch, "E1514", {"start": v(-2.86, 22.88) * mm, "end": v(31.37, 81.27) * mm});
            skLineSegment(sketch, "E1515", {"start": v(31.37, 81.27) * mm, "end": v(30.11, 85.35) * mm});
            skLineSegment(sketch, "E1516", {"start": v(30.11, 85.35) * mm, "end": v(24, 87.89) * mm});
            skLineSegment(sketch, "E1517", {"start": v(24, 87.89) * mm, "end": v(17.74, 90) * mm});
            skLineSegment(sketch, "E1518", {"start": v(17.74, 90) * mm, "end": v(11.34, 91.65) * mm});
            skLineSegment(sketch, "E1519", {"start": v(11.34, 91.65) * mm, "end": v(4.83, 92.85) * mm});
            skLineSegment(sketch, "E1520", {"start": v(4.83, 92.85) * mm, "end": v(-1.74, 93.6) * mm});
            skLineSegment(sketch, "E1521", {"start": v(-1.74, 93.6) * mm, "end": v(-8.35, 93.87) * mm});
            skLineSegment(sketch, "E1522", {"start": v(-8.35, 93.87) * mm, "end": v(-14.96, 93.68) * mm});
            skLineSegment(sketch, "E1523", {"start": v(-14.96, 93.68) * mm, "end": v(-21.54, 93.03) * mm});
            skLineSegment(sketch, "E1524", {"start": v(-21.54, 93.03) * mm, "end": v(-28.06, 91.92) * mm});
            skLineSegment(sketch, "E1525", {"start": v(-28.06, 91.92) * mm, "end": v(-34.48, 90.34) * mm});
            skLineSegment(sketch, "E1526", {"start": v(-34.48, 90.34) * mm, "end": v(-40.78, 88.32) * mm});
            skLineSegment(sketch, "E1527", {"start": v(-40.78, 88.32) * mm, "end": v(-46.92, 85.87) * mm});
            skLineSegment(sketch, "E1528", {"start": v(-46.92, 85.87) * mm, "end": v(-48.23, 81.8) * mm});
            skLineSegment(sketch, "E1529", {"start": v(-48.23, 81.8) * mm, "end": v(-14.78, 22.96) * mm});
            skLineSegment(sketch, "E1530", {"start": v(-14.78, 22.96) * mm, "end": v(-9.84, 20.65) * mm});
            skLineSegment(sketch, "E1531", {"start": v(-9.84, 20.65) * mm, "end": v(-2.86, 22.88) * mm});
            skLineSegment(sketch, "E1532", {"start": v(-25.74, 16.73) * mm, "end": v(-59.18, 75.57) * mm});
            skLineSegment(sketch, "E1533", {"start": v(-59.18, 75.57) * mm, "end": v(-63.35, 76.53) * mm});
            skLineSegment(sketch, "E1534", {"start": v(-63.35, 76.53) * mm, "end": v(-68.6, 72.5) * mm});
            skLineSegment(sketch, "E1535", {"start": v(-68.6, 72.5) * mm, "end": v(-73.56, 68.13) * mm});
            skLineSegment(sketch, "E1536", {"start": v(-73.56, 68.13) * mm, "end": v(-78.2, 63.42) * mm});
            skLineSegment(sketch, "E1537", {"start": v(-78.2, 63.42) * mm, "end": v(-82.49, 58.39) * mm});
            skLineSegment(sketch, "E1538", {"start": v(-82.49, 58.39) * mm, "end": v(-86.42, 53.06) * mm});
            skLineSegment(sketch, "E1539", {"start": v(-86.42, 53.06) * mm, "end": v(-89.96, 47.48) * mm});
            skLineSegment(sketch, "E1540", {"start": v(-89.96, 47.48) * mm, "end": v(-93.1, 41.66) * mm});
            skLineSegment(sketch, "E1541", {"start": v(-93.1, 41.66) * mm, "end": v(-95.83, 35.64) * mm});
            skLineSegment(sketch, "E1542", {"start": v(-95.83, 35.64) * mm, "end": v(-98.12, 29.43) * mm});
            skLineSegment(sketch, "E1543", {"start": v(-98.12, 29.43) * mm, "end": v(-99.97, 23.09) * mm});
            skLineSegment(sketch, "E1544", {"start": v(-99.97, 23.09) * mm, "end": v(-101.37, 16.62) * mm});
            skLineSegment(sketch, "E1545", {"start": v(-101.37, 16.62) * mm, "end": v(-102.31, 10.08) * mm});
            skLineSegment(sketch, "E1546", {"start": v(-102.31, 10.08) * mm, "end": v(-99.45, 6.9) * mm});
            skLineSegment(sketch, "E1547", {"start": v(-99.45, 6.9) * mm, "end": v(-31.77, 6.45) * mm});
            skLineSegment(sketch, "E1548", {"start": v(-31.77, 6.45) * mm, "end": v(-27.3, 9.57) * mm});
            skLineSegment(sketch, "E1549", {"start": v(-27.3, 9.57) * mm, "end": v(-25.74, 16.73) * mm});
            skLineSegment(sketch, "E1550", {"start": v(-31.85, -6.15) * mm, "end": v(-99.53, -5.7) * mm});
            skLineSegment(sketch, "E1551", {"start": v(-99.53, -5.7) * mm, "end": v(-102.44, -8.82) * mm});
            skLineSegment(sketch, "E1552", {"start": v(-102.44, -8.82) * mm, "end": v(-101.59, -15.38) * mm});
            skLineSegment(sketch, "E1553", {"start": v(-101.59, -15.38) * mm, "end": v(-100.27, -21.86) * mm});
            skLineSegment(sketch, "E1554", {"start": v(-100.27, -21.86) * mm, "end": v(-98.5, -28.24) * mm});
            skLineSegment(sketch, "E1555", {"start": v(-98.5, -28.24) * mm, "end": v(-96.3, -34.47) * mm});
            skLineSegment(sketch, "E1556", {"start": v(-96.3, -34.47) * mm, "end": v(-93.65, -40.53) * mm});
            skLineSegment(sketch, "E1557", {"start": v(-93.65, -40.53) * mm, "end": v(-90.6, -46.4) * mm});
            skLineSegment(sketch, "E1558", {"start": v(-90.6, -46.4) * mm, "end": v(-87.12, -52.02) * mm});
            skLineSegment(sketch, "E1559", {"start": v(-87.12, -52.02) * mm, "end": v(-83.27, -57.4) * mm});
            skLineSegment(sketch, "E1560", {"start": v(-83.27, -57.4) * mm, "end": v(-79.04, -62.48) * mm});
            skLineSegment(sketch, "E1561", {"start": v(-79.04, -62.48) * mm, "end": v(-74.47, -67.26) * mm});
            skLineSegment(sketch, "E1562", {"start": v(-74.47, -67.26) * mm, "end": v(-69.57, -71.7) * mm});
            skLineSegment(sketch, "E1563", {"start": v(-69.57, -71.7) * mm, "end": v(-64.37, -75.8) * mm});
            skLineSegment(sketch, "E1564", {"start": v(-64.37, -75.8) * mm, "end": v(-60.2, -74.9) * mm});
            skLineSegment(sketch, "E1565", {"start": v(-60.2, -74.9) * mm, "end": v(-25.96, -16.51) * mm});
            skLineSegment(sketch, "E1566", {"start": v(-25.96, -16.51) * mm, "end": v(-26.43, -11.08) * mm});
            skLineSegment(sketch, "E1567", {"start": v(-26.43, -11.08) * mm, "end": v(-31.85, -6.15) * mm});
            skLineSegment(sketch, "E1568", {"start": v(-15.1, -22.88) * mm, "end": v(-49.33, -81.27) * mm});
            skLineSegment(sketch, "E1569", {"start": v(-49.33, -81.27) * mm, "end": v(-48.07, -85.35) * mm});
            skLineSegment(sketch, "E1570", {"start": v(-48.07, -85.35) * mm, "end": v(-41.96, -87.9) * mm});
            skLineSegment(sketch, "E1571", {"start": v(-41.96, -87.9) * mm, "end": v(-35.7, -90) * mm});
            skLineSegment(sketch, "E1572", {"start": v(-35.7, -90) * mm, "end": v(-29.29, -91.65) * mm});
            skLineSegment(sketch, "E1573", {"start": v(-29.29, -91.65) * mm, "end": v(-22.79, -92.86) * mm});
            skLineSegment(sketch, "E1574", {"start": v(-22.79, -92.86) * mm, "end": v(-16.22, -93.6) * mm});
            skLineSegment(sketch, "E1575", {"start": v(-16.22, -93.6) * mm, "end": v(-9.6, -93.88) * mm});
            skLineSegment(sketch, "E1576", {"start": v(-9.6, -93.88) * mm, "end": v(-3, -93.69) * mm});
            skLineSegment(sketch, "E1577", {"start": v(-3, -93.69) * mm, "end": v(3.58, -93.03) * mm});
            skLineSegment(sketch, "E1578", {"start": v(3.58, -93.03) * mm, "end": v(10.1, -91.92) * mm});
            skLineSegment(sketch, "E1579", {"start": v(10.1, -91.92) * mm, "end": v(16.53, -90.35) * mm});
            skLineSegment(sketch, "E1580", {"start": v(16.53, -90.35) * mm, "end": v(22.82, -88.33) * mm});
            skLineSegment(sketch, "E1581", {"start": v(22.82, -88.33) * mm, "end": v(28.96, -85.87) * mm});
            skLineSegment(sketch, "E1582", {"start": v(28.96, -85.87) * mm, "end": v(30.28, -81.8) * mm});
            skLineSegment(sketch, "E1583", {"start": v(30.28, -81.8) * mm, "end": v(-3.17, -22.96) * mm});
            skLineSegment(sketch, "E1584", {"start": v(-3.17, -22.96) * mm, "end": v(-8.11, -20.65) * mm});
            skLineSegment(sketch, "E1585", {"start": v(-8.11, -20.65) * mm, "end": v(-15.1, -22.88) * mm});
            skLineSegment(sketch, "E1586", {"start": v(7.78, -16.74) * mm, "end": v(41.23, -75.58) * mm});
            skLineSegment(sketch, "E1587", {"start": v(41.23, -75.58) * mm, "end": v(45.4, -76.53) * mm});
            skLineSegment(sketch, "E1588", {"start": v(45.4, -76.53) * mm, "end": v(50.65, -72.51) * mm});
            skLineSegment(sketch, "E1589", {"start": v(50.65, -72.51) * mm, "end": v(55.6, -68.14) * mm});
            skLineSegment(sketch, "E1590", {"start": v(55.6, -68.14) * mm, "end": v(60.24, -63.42) * mm});
            skLineSegment(sketch, "E1591", {"start": v(60.24, -63.42) * mm, "end": v(64.53, -58.39) * mm});
            skLineSegment(sketch, "E1592", {"start": v(64.53, -58.39) * mm, "end": v(68.46, -53.07) * mm});
            skLineSegment(sketch, "E1593", {"start": v(68.46, -53.07) * mm, "end": v(72, -47.49) * mm});
            skLineSegment(sketch, "E1594", {"start": v(72, -47.49) * mm, "end": v(75.15, -41.67) * mm});
            skLineSegment(sketch, "E1595", {"start": v(75.15, -41.67) * mm, "end": v(77.87, -35.64) * mm});
            skLineSegment(sketch, "E1596", {"start": v(77.87, -35.64) * mm, "end": v(80.17, -29.44) * mm});
            skLineSegment(sketch, "E1597", {"start": v(80.17, -29.44) * mm, "end": v(82.02, -23.09) * mm});
            skLineSegment(sketch, "E1598", {"start": v(82.02, -23.09) * mm, "end": v(83.42, -16.63) * mm});
            skLineSegment(sketch, "E1599", {"start": v(83.42, -16.63) * mm, "end": v(84.36, -10.08) * mm});
            skLineSegment(sketch, "E1600", {"start": v(84.36, -10.08) * mm, "end": v(81.5, -6.91) * mm});
            skLineSegment(sketch, "E1601", {"start": v(81.5, -6.91) * mm, "end": v(13.81, -6.46) * mm});
            skLineSegment(sketch, "E1602", {"start": v(13.81, -6.46) * mm, "end": v(9.34, -9.58) * mm});
            skLineSegment(sketch, "E1603", {"start": v(9.34, -9.58) * mm, "end": v(7.78, -16.74) * mm});
            skLineSegment(sketch, "E1604", {"start": v(-7.98, 0) * mm, "end": v(-8.01, 0.26) * mm});
            skLineSegment(sketch, "E1605", {"start": v(-8.01, 0.26) * mm, "end": v(-8.11, 0.5) * mm});
            skLineSegment(sketch, "E1606", {"start": v(-8.11, 0.5) * mm, "end": v(-8.27, 0.7) * mm});
            skLineSegment(sketch, "E1607", {"start": v(-8.27, 0.7) * mm, "end": v(-8.48, 0.86) * mm});
            skLineSegment(sketch, "E1608", {"start": v(-8.48, 0.86) * mm, "end": v(-8.72, 0.96) * mm});
            skLineSegment(sketch, "E1609", {"start": v(-8.72, 0.96) * mm, "end": v(-8.98, 1) * mm});
            skLineSegment(sketch, "E1610", {"start": v(-8.98, 1) * mm, "end": v(-9.24, 0.96) * mm});
            skLineSegment(sketch, "E1611", {"start": v(-9.24, 0.96) * mm, "end": v(-9.48, 0.86) * mm});
            skLineSegment(sketch, "E1612", {"start": v(-9.48, 0.86) * mm, "end": v(-9.68, 0.7) * mm});
            skLineSegment(sketch, "E1613", {"start": v(-9.68, 0.7) * mm, "end": v(-9.84, 0.5) * mm});
            skLineSegment(sketch, "E1614", {"start": v(-9.84, 0.5) * mm, "end": v(-9.94, 0.26) * mm});
            skLineSegment(sketch, "E1615", {"start": v(-9.94, 0.26) * mm, "end": v(-9.98, 0) * mm});
            skLineSegment(sketch, "E1616", {"start": v(-9.98, 0) * mm, "end": v(-9.94, -0.26) * mm});
            skLineSegment(sketch, "E1617", {"start": v(-9.94, -0.26) * mm, "end": v(-9.84, -0.5) * mm});
            skLineSegment(sketch, "E1618", {"start": v(-9.84, -0.5) * mm, "end": v(-9.68, -0.7) * mm});
            skLineSegment(sketch, "E1619", {"start": v(-9.68, -0.7) * mm, "end": v(-9.48, -0.87) * mm});
            skLineSegment(sketch, "E1620", {"start": v(-9.48, -0.87) * mm, "end": v(-9.24, -0.97) * mm});
            skLineSegment(sketch, "E1621", {"start": v(-9.24, -0.97) * mm, "end": v(-8.98, -1) * mm});
            skLineSegment(sketch, "E1622", {"start": v(-8.98, -1) * mm, "end": v(-8.72, -0.97) * mm});
            skLineSegment(sketch, "E1623", {"start": v(-8.72, -0.97) * mm, "end": v(-8.48, -0.87) * mm});
            skLineSegment(sketch, "E1624", {"start": v(-8.48, -0.87) * mm, "end": v(-8.27, -0.7) * mm});
            skLineSegment(sketch, "E1625", {"start": v(-8.27, -0.7) * mm, "end": v(-8.11, -0.5) * mm});
            skLineSegment(sketch, "E1626", {"start": v(-8.11, -0.5) * mm, "end": v(-8.01, -0.26) * mm});
            skLineSegment(sketch, "E1627", {"start": v(-8.01, -0.26) * mm, "end": v(-7.98, 0) * mm});
            skLineSegment(sketch, "E1628", {"start": v(98.4, -0.13) * mm, "end": v(98.35, -0.03) * mm});
            skLineSegment(sketch, "E1629", {"start": v(98.35, -0.03) * mm, "end": v(98.3, 0) * mm});
            skLineSegment(sketch, "E1630", {"start": v(98.3, 0) * mm, "end": v(98.18, 0.03) * mm});
            skLineSegment(sketch, "E1631", {"start": v(98.18, 0.03) * mm, "end": v(98.07, 0.05) * mm});
            skLineSegment(sketch, "E1632", {"start": v(98.07, 0.05) * mm, "end": v(97.85, 0.08) * mm});
            skLineSegment(sketch, "E1633", {"start": v(97.85, 0.08) * mm, "end": v(97.63, 0.15) * mm});
            skLineSegment(sketch, "E1634", {"start": v(97.63, 0.15) * mm, "end": v(97.4, 0.24) * mm});
            skLineSegment(sketch, "E1635", {"start": v(97.4, 0.24) * mm, "end": v(97.19, 0.36) * mm});
            skLineSegment(sketch, "E1636", {"start": v(97.19, 0.36) * mm, "end": v(96.97, 0.49) * mm});
            skLineSegment(sketch, "E1637", {"start": v(96.97, 0.49) * mm, "end": v(96.75, 0.63) * mm});
            skLineSegment(sketch, "E1638", {"start": v(96.75, 0.63) * mm, "end": v(96.9, 1.68) * mm});
            skLineSegment(sketch, "E1639", {"start": v(96.9, 1.68) * mm, "end": v(97.14, 1.76) * mm});
            skLineSegment(sketch, "E1640", {"start": v(97.14, 1.76) * mm, "end": v(97.38, 1.83) * mm});
            skLineSegment(sketch, "E1641", {"start": v(97.38, 1.83) * mm, "end": v(97.63, 1.88) * mm});
            skLineSegment(sketch, "E1642", {"start": v(97.63, 1.88) * mm, "end": v(97.86, 1.9) * mm});
            skLineSegment(sketch, "E1643", {"start": v(97.86, 1.9) * mm, "end": v(98.1, 1.92) * mm});
            skLineSegment(sketch, "E1644", {"start": v(98.1, 1.92) * mm, "end": v(98.32, 1.89) * mm});
            skLineSegment(sketch, "E1645", {"start": v(98.32, 1.89) * mm, "end": v(98.43, 1.87) * mm});
            skLineSegment(sketch, "E1646", {"start": v(98.43, 1.87) * mm, "end": v(98.55, 1.88) * mm});
            skLineSegment(sketch, "E1647", {"start": v(98.55, 1.88) * mm, "end": v(98.61, 1.9) * mm});
            skLineSegment(sketch, "E1648", {"start": v(98.61, 1.9) * mm, "end": v(98.7, 1.97) * mm});
            skLineSegment(sketch, "E1649", {"start": v(98.7, 1.97) * mm, "end": v(99.04, 2.9) * mm});
            skLineSegment(sketch, "E1650", {"start": v(99.04, 2.9) * mm, "end": v(99.03, 3.01) * mm});
            skLineSegment(sketch, "E1651", {"start": v(99.03, 3.01) * mm, "end": v(99, 3.07) * mm});
            skLineSegment(sketch, "E1652", {"start": v(99, 3.07) * mm, "end": v(98.91, 3.15) * mm});
            skLineSegment(sketch, "E1653", {"start": v(98.91, 3.15) * mm, "end": v(98.82, 3.21) * mm});
            skLineSegment(sketch, "E1654", {"start": v(98.82, 3.21) * mm, "end": v(98.63, 3.34) * mm});
            skLineSegment(sketch, "E1655", {"start": v(98.63, 3.34) * mm, "end": v(98.46, 3.5) * mm});
            skLineSegment(sketch, "E1656", {"start": v(98.46, 3.5) * mm, "end": v(98.3, 3.67) * mm});
            skLineSegment(sketch, "E1657", {"start": v(98.3, 3.67) * mm, "end": v(98.15, 3.87) * mm});
            skLineSegment(sketch, "E1658", {"start": v(98.15, 3.87) * mm, "end": v(98.01, 4.08) * mm});
            skLineSegment(sketch, "E1659", {"start": v(98.01, 4.08) * mm, "end": v(97.88, 4.3) * mm});
            skLineSegment(sketch, "E1660", {"start": v(97.88, 4.3) * mm, "end": v(98.46, 5.19) * mm});
            skLineSegment(sketch, "E1661", {"start": v(98.46, 5.19) * mm, "end": v(98.72, 5.16) * mm});
            skLineSegment(sketch, "E1662", {"start": v(98.72, 5.16) * mm, "end": v(98.97, 5.11) * mm});
            skLineSegment(sketch, "E1663", {"start": v(98.97, 5.11) * mm, "end": v(99.2, 5.05) * mm});
            skLineSegment(sketch, "E1664", {"start": v(99.2, 5.05) * mm, "end": v(99.44, 4.97) * mm});
            skLineSegment(sketch, "E1665", {"start": v(99.44, 4.97) * mm, "end": v(99.65, 4.88) * mm});
            skLineSegment(sketch, "E1666", {"start": v(99.65, 4.88) * mm, "end": v(99.84, 4.76) * mm});
            skLineSegment(sketch, "E1667", {"start": v(99.84, 4.76) * mm, "end": v(99.93, 4.7) * mm});
            skLineSegment(sketch, "E1668", {"start": v(99.93, 4.7) * mm, "end": v(100.04, 4.65) * mm});
            skLineSegment(sketch, "E1669", {"start": v(100.04, 4.65) * mm, "end": v(100.1, 4.64) * mm});
            skLineSegment(sketch, "E1670", {"start": v(100.1, 4.64) * mm, "end": v(100.2, 4.67) * mm});
            skLineSegment(sketch, "E1671", {"start": v(100.2, 4.67) * mm, "end": v(100.93, 5.36) * mm});
            skLineSegment(sketch, "E1672", {"start": v(100.93, 5.36) * mm, "end": v(100.97, 5.46) * mm});
            skLineSegment(sketch, "E1673", {"start": v(100.97, 5.46) * mm, "end": v(100.96, 5.53) * mm});
            skLineSegment(sketch, "E1674", {"start": v(100.96, 5.53) * mm, "end": v(100.92, 5.64) * mm});
            skLineSegment(sketch, "E1675", {"start": v(100.92, 5.64) * mm, "end": v(100.86, 5.73) * mm});
            skLineSegment(sketch, "E1676", {"start": v(100.86, 5.73) * mm, "end": v(100.75, 5.93) * mm});
            skLineSegment(sketch, "E1677", {"start": v(100.75, 5.93) * mm, "end": v(100.66, 6.15) * mm});
            skLineSegment(sketch, "E1678", {"start": v(100.66, 6.15) * mm, "end": v(100.6, 6.38) * mm});
            skLineSegment(sketch, "E1679", {"start": v(100.6, 6.38) * mm, "end": v(100.55, 6.62) * mm});
            skLineSegment(sketch, "E1680", {"start": v(100.55, 6.62) * mm, "end": v(100.51, 6.87) * mm});
            skLineSegment(sketch, "E1681", {"start": v(100.51, 6.87) * mm, "end": v(100.5, 7.13) * mm});
            skLineSegment(sketch, "E1682", {"start": v(100.5, 7.13) * mm, "end": v(101.4, 7.67) * mm});
            skLineSegment(sketch, "E1683", {"start": v(101.4, 7.67) * mm, "end": v(101.62, 7.53) * mm});
            skLineSegment(sketch, "E1684", {"start": v(101.62, 7.53) * mm, "end": v(101.82, 7.38) * mm});
            skLineSegment(sketch, "E1685", {"start": v(101.82, 7.38) * mm, "end": v(102.01, 7.22) * mm});
            skLineSegment(sketch, "E1686", {"start": v(102.01, 7.22) * mm, "end": v(102.18, 7.06) * mm});
            skLineSegment(sketch, "E1687", {"start": v(102.18, 7.06) * mm, "end": v(102.33, 6.88) * mm});
            skLineSegment(sketch, "E1688", {"start": v(102.33, 6.88) * mm, "end": v(102.45, 6.68) * mm});
            skLineSegment(sketch, "E1689", {"start": v(102.45, 6.68) * mm, "end": v(102.51, 6.59) * mm});
            skLineSegment(sketch, "E1690", {"start": v(102.51, 6.59) * mm, "end": v(102.59, 6.5) * mm});
            skLineSegment(sketch, "E1691", {"start": v(102.59, 6.5) * mm, "end": v(102.64, 6.46) * mm});
            skLineSegment(sketch, "E1692", {"start": v(102.64, 6.46) * mm, "end": v(102.75, 6.44) * mm});
            skLineSegment(sketch, "E1693", {"start": v(102.75, 6.44) * mm, "end": v(103.7, 6.75) * mm});
            skLineSegment(sketch, "E1694", {"start": v(103.7, 6.75) * mm, "end": v(103.78, 6.83) * mm});
            skLineSegment(sketch, "E1695", {"start": v(103.78, 6.83) * mm, "end": v(103.8, 6.9) * mm});
            skLineSegment(sketch, "E1696", {"start": v(103.8, 6.9) * mm, "end": v(103.8, 7) * mm});
            skLineSegment(sketch, "E1697", {"start": v(103.8, 7) * mm, "end": v(103.8, 7.12) * mm});
            skLineSegment(sketch, "E1698", {"start": v(103.8, 7.12) * mm, "end": v(103.78, 7.35) * mm});
            skLineSegment(sketch, "E1699", {"start": v(103.78, 7.35) * mm, "end": v(103.8, 7.58) * mm});
            skLineSegment(sketch, "E1700", {"start": v(103.8, 7.58) * mm, "end": v(103.84, 7.82) * mm});
            skLineSegment(sketch, "E1701", {"start": v(103.84, 7.82) * mm, "end": v(103.9, 8.05) * mm});
            skLineSegment(sketch, "E1702", {"start": v(103.9, 8.05) * mm, "end": v(103.97, 8.3) * mm});
            skLineSegment(sketch, "E1703", {"start": v(103.97, 8.3) * mm, "end": v(104.07, 8.54) * mm});
            skLineSegment(sketch, "E1704", {"start": v(104.07, 8.54) * mm, "end": v(105.12, 8.63) * mm});
            skLineSegment(sketch, "E1705", {"start": v(105.12, 8.63) * mm, "end": v(105.26, 8.41) * mm});
            skLineSegment(sketch, "E1706", {"start": v(105.26, 8.41) * mm, "end": v(105.38, 8.19) * mm});
            skLineSegment(sketch, "E1707", {"start": v(105.38, 8.19) * mm, "end": v(105.48, 7.96) * mm});
            skLineSegment(sketch, "E1708", {"start": v(105.48, 7.96) * mm, "end": v(105.56, 7.74) * mm});
            skLineSegment(sketch, "E1709", {"start": v(105.56, 7.74) * mm, "end": v(105.62, 7.51) * mm});
            skLineSegment(sketch, "E1710", {"start": v(105.62, 7.51) * mm, "end": v(105.64, 7.29) * mm});
            skLineSegment(sketch, "E1711", {"start": v(105.64, 7.29) * mm, "end": v(105.65, 7.18) * mm});
            skLineSegment(sketch, "E1712", {"start": v(105.65, 7.18) * mm, "end": v(105.68, 7.06) * mm});
            skLineSegment(sketch, "E1713", {"start": v(105.68, 7.06) * mm, "end": v(105.71, 7) * mm});
            skLineSegment(sketch, "E1714", {"start": v(105.71, 7) * mm, "end": v(105.8, 6.94) * mm});
            skLineSegment(sketch, "E1715", {"start": v(105.8, 6.94) * mm, "end": v(106.8, 6.8) * mm});
            skLineSegment(sketch, "E1716", {"start": v(106.8, 6.8) * mm, "end": v(106.9, 6.84) * mm});
            skLineSegment(sketch, "E1717", {"start": v(106.9, 6.84) * mm, "end": v(106.94, 6.9) * mm});
            skLineSegment(sketch, "E1718", {"start": v(106.94, 6.9) * mm, "end": v(107, 7) * mm});
            skLineSegment(sketch, "E1719", {"start": v(107, 7) * mm, "end": v(107.04, 7.1) * mm});
            skLineSegment(sketch, "E1720", {"start": v(107.04, 7.1) * mm, "end": v(107.12, 7.3) * mm});
            skLineSegment(sketch, "E1721", {"start": v(107.12, 7.3) * mm, "end": v(107.24, 7.51) * mm});
            skLineSegment(sketch, "E1722", {"start": v(107.24, 7.51) * mm, "end": v(107.38, 7.7) * mm});
            skLineSegment(sketch, "E1723", {"start": v(107.38, 7.7) * mm, "end": v(107.54, 7.9) * mm});
            skLineSegment(sketch, "E1724", {"start": v(107.54, 7.9) * mm, "end": v(107.71, 8.08) * mm});
            skLineSegment(sketch, "E1725", {"start": v(107.71, 8.08) * mm, "end": v(107.9, 8.26) * mm});
            skLineSegment(sketch, "E1726", {"start": v(107.9, 8.26) * mm, "end": v(108.9, 7.89) * mm});
            skLineSegment(sketch, "E1727", {"start": v(108.9, 7.89) * mm, "end": v(108.92, 7.63) * mm});
            skLineSegment(sketch, "E1728", {"start": v(108.92, 7.63) * mm, "end": v(108.93, 7.37) * mm});
            skLineSegment(sketch, "E1729", {"start": v(108.93, 7.37) * mm, "end": v(108.92, 7.13) * mm});
            skLineSegment(sketch, "E1730", {"start": v(108.92, 7.13) * mm, "end": v(108.9, 6.89) * mm});
            skLineSegment(sketch, "E1731", {"start": v(108.9, 6.89) * mm, "end": v(108.85, 6.66) * mm});
            skLineSegment(sketch, "E1732", {"start": v(108.85, 6.66) * mm, "end": v(108.78, 6.45) * mm});
            skLineSegment(sketch, "E1733", {"start": v(108.78, 6.45) * mm, "end": v(108.74, 6.34) * mm});
            skLineSegment(sketch, "E1734", {"start": v(108.74, 6.34) * mm, "end": v(108.72, 6.23) * mm});
            skLineSegment(sketch, "E1735", {"start": v(108.72, 6.23) * mm, "end": v(108.72, 6.16) * mm});
            skLineSegment(sketch, "E1736", {"start": v(108.72, 6.16) * mm, "end": v(108.77, 6.07) * mm});
            skLineSegment(sketch, "E1737", {"start": v(108.77, 6.07) * mm, "end": v(109.6, 5.52) * mm});
            skLineSegment(sketch, "E1738", {"start": v(109.6, 5.52) * mm, "end": v(109.72, 5.5) * mm});
            skLineSegment(sketch, "E1739", {"start": v(109.72, 5.5) * mm, "end": v(109.78, 5.53) * mm});
            skLineSegment(sketch, "E1740", {"start": v(109.78, 5.53) * mm, "end": v(109.88, 5.6) * mm});
            skLineSegment(sketch, "E1741", {"start": v(109.88, 5.6) * mm, "end": v(109.96, 5.67) * mm});
            skLineSegment(sketch, "E1742", {"start": v(109.96, 5.67) * mm, "end": v(110.12, 5.82) * mm});
            skLineSegment(sketch, "E1743", {"start": v(110.12, 5.82) * mm, "end": v(110.31, 5.95) * mm});
            skLineSegment(sketch, "E1744", {"start": v(110.31, 5.95) * mm, "end": v(110.52, 6.07) * mm});
            skLineSegment(sketch, "E1745", {"start": v(110.52, 6.07) * mm, "end": v(110.75, 6.17) * mm});
            skLineSegment(sketch, "E1746", {"start": v(110.75, 6.17) * mm, "end": v(110.99, 6.26) * mm});
            skLineSegment(sketch, "E1747", {"start": v(110.99, 6.26) * mm, "end": v(111.24, 6.34) * mm});
            skLineSegment(sketch, "E1748", {"start": v(111.24, 6.34) * mm, "end": v(111.96, 5.58) * mm});
            skLineSegment(sketch, "E1749", {"start": v(111.96, 5.58) * mm, "end": v(111.88, 5.33) * mm});
            skLineSegment(sketch, "E1750", {"start": v(111.88, 5.33) * mm, "end": v(111.78, 5.1) * mm});
            skLineSegment(sketch, "E1751", {"start": v(111.78, 5.1) * mm, "end": v(111.67, 4.88) * mm});
            skLineSegment(sketch, "E1752", {"start": v(111.67, 4.88) * mm, "end": v(111.54, 4.67) * mm});
            skLineSegment(sketch, "E1753", {"start": v(111.54, 4.67) * mm, "end": v(111.4, 4.49) * mm});
            skLineSegment(sketch, "E1754", {"start": v(111.4, 4.49) * mm, "end": v(111.24, 4.33) * mm});
            skLineSegment(sketch, "E1755", {"start": v(111.24, 4.33) * mm, "end": v(111.16, 4.25) * mm});
            skLineSegment(sketch, "E1756", {"start": v(111.16, 4.25) * mm, "end": v(111.09, 4.16) * mm});
            skLineSegment(sketch, "E1757", {"start": v(111.09, 4.16) * mm, "end": v(111.06, 4.1) * mm});
            skLineSegment(sketch, "E1758", {"start": v(111.06, 4.1) * mm, "end": v(111.07, 3.99) * mm});
            skLineSegment(sketch, "E1759", {"start": v(111.07, 3.99) * mm, "end": v(111.58, 3.13) * mm});
            skLineSegment(sketch, "E1760", {"start": v(111.58, 3.13) * mm, "end": v(111.67, 3.07) * mm});
            skLineSegment(sketch, "E1761", {"start": v(111.67, 3.07) * mm, "end": v(111.74, 3.06) * mm});
            skLineSegment(sketch, "E1762", {"start": v(111.74, 3.06) * mm, "end": v(111.86, 3.08) * mm});
            skLineSegment(sketch, "E1763", {"start": v(111.86, 3.08) * mm, "end": v(111.96, 3.12) * mm});
            skLineSegment(sketch, "E1764", {"start": v(111.96, 3.12) * mm, "end": v(112.18, 3.18) * mm});
            skLineSegment(sketch, "E1765", {"start": v(112.18, 3.18) * mm, "end": v(112.4, 3.22) * mm});
            skLineSegment(sketch, "E1766", {"start": v(112.4, 3.22) * mm, "end": v(112.65, 3.23) * mm});
            skLineSegment(sketch, "E1767", {"start": v(112.65, 3.23) * mm, "end": v(112.9, 3.23) * mm});
            skLineSegment(sketch, "E1768", {"start": v(112.9, 3.23) * mm, "end": v(113.15, 3.2) * mm});
            skLineSegment(sketch, "E1769", {"start": v(113.15, 3.2) * mm, "end": v(113.4, 3.16) * mm});
            skLineSegment(sketch, "E1770", {"start": v(113.4, 3.16) * mm, "end": v(113.73, 2.16) * mm});
            skLineSegment(sketch, "E1771", {"start": v(113.73, 2.16) * mm, "end": v(113.55, 1.98) * mm});
            skLineSegment(sketch, "E1772", {"start": v(113.55, 1.98) * mm, "end": v(113.35, 1.81) * mm});
            skLineSegment(sketch, "E1773", {"start": v(113.35, 1.81) * mm, "end": v(113.16, 1.66) * mm});
            skLineSegment(sketch, "E1774", {"start": v(113.16, 1.66) * mm, "end": v(112.96, 1.53) * mm});
            skLineSegment(sketch, "E1775", {"start": v(112.96, 1.53) * mm, "end": v(112.75, 1.42) * mm});
            skLineSegment(sketch, "E1776", {"start": v(112.75, 1.42) * mm, "end": v(112.54, 1.35) * mm});
            skLineSegment(sketch, "E1777", {"start": v(112.54, 1.35) * mm, "end": v(112.43, 1.32) * mm});
            skLineSegment(sketch, "E1778", {"start": v(112.43, 1.32) * mm, "end": v(112.32, 1.26) * mm});
            skLineSegment(sketch, "E1779", {"start": v(112.32, 1.26) * mm, "end": v(112.28, 1.22) * mm});
            skLineSegment(sketch, "E1780", {"start": v(112.28, 1.22) * mm, "end": v(112.24, 1.12) * mm});
            skLineSegment(sketch, "E1781", {"start": v(112.24, 1.12) * mm, "end": v(112.33, 0.12) * mm});
            skLineSegment(sketch, "E1782", {"start": v(112.33, 0.12) * mm, "end": v(112.38, 0.03) * mm});
            skLineSegment(sketch, "E1783", {"start": v(112.38, 0.03) * mm, "end": v(112.44, 0) * mm});
            skLineSegment(sketch, "E1784", {"start": v(112.44, 0) * mm, "end": v(112.55, -0.04) * mm});
            skLineSegment(sketch, "E1785", {"start": v(112.55, -0.04) * mm, "end": v(112.66, -0.06) * mm});
            skLineSegment(sketch, "E1786", {"start": v(112.66, -0.06) * mm, "end": v(112.89, -0.09) * mm});
            skLineSegment(sketch, "E1787", {"start": v(112.89, -0.09) * mm, "end": v(113.1, -0.16) * mm});
            skLineSegment(sketch, "E1788", {"start": v(113.1, -0.16) * mm, "end": v(113.33, -0.25) * mm});
            skLineSegment(sketch, "E1789", {"start": v(113.33, -0.25) * mm, "end": v(113.55, -0.36) * mm});
            skLineSegment(sketch, "E1790", {"start": v(113.55, -0.36) * mm, "end": v(113.77, -0.5) * mm});
            skLineSegment(sketch, "E1791", {"start": v(113.77, -0.5) * mm, "end": v(113.98, -0.64) * mm});
            skLineSegment(sketch, "E1792", {"start": v(113.98, -0.64) * mm, "end": v(113.84, -1.68) * mm});
            skLineSegment(sketch, "E1793", {"start": v(113.84, -1.68) * mm, "end": v(113.6, -1.77) * mm});
            skLineSegment(sketch, "E1794", {"start": v(113.6, -1.77) * mm, "end": v(113.35, -1.83) * mm});
            skLineSegment(sketch, "E1795", {"start": v(113.35, -1.83) * mm, "end": v(113.1, -1.88) * mm});
            skLineSegment(sketch, "E1796", {"start": v(113.1, -1.88) * mm, "end": v(112.87, -1.91) * mm});
            skLineSegment(sketch, "E1797", {"start": v(112.87, -1.91) * mm, "end": v(112.64, -1.92) * mm});
            skLineSegment(sketch, "E1798", {"start": v(112.64, -1.92) * mm, "end": v(112.41, -1.9) * mm});
            skLineSegment(sketch, "E1799", {"start": v(112.41, -1.9) * mm, "end": v(112.3, -1.88) * mm});
            skLineSegment(sketch, "E1800", {"start": v(112.3, -1.88) * mm, "end": v(112.18, -1.88) * mm});
            skLineSegment(sketch, "E1801", {"start": v(112.18, -1.88) * mm, "end": v(112.12, -1.9) * mm});
            skLineSegment(sketch, "E1802", {"start": v(112.12, -1.9) * mm, "end": v(112.04, -1.97) * mm});
            skLineSegment(sketch, "E1803", {"start": v(112.04, -1.97) * mm, "end": v(111.7, -2.9) * mm});
            skLineSegment(sketch, "E1804", {"start": v(111.7, -2.9) * mm, "end": v(111.7, -3.02) * mm});
            skLineSegment(sketch, "E1805", {"start": v(111.7, -3.02) * mm, "end": v(111.74, -3.07) * mm});
            skLineSegment(sketch, "E1806", {"start": v(111.74, -3.07) * mm, "end": v(111.82, -3.15) * mm});
            skLineSegment(sketch, "E1807", {"start": v(111.82, -3.15) * mm, "end": v(111.92, -3.21) * mm});
            skLineSegment(sketch, "E1808", {"start": v(111.92, -3.21) * mm, "end": v(112.1, -3.34) * mm});
            skLineSegment(sketch, "E1809", {"start": v(112.1, -3.34) * mm, "end": v(112.28, -3.5) * mm});
            skLineSegment(sketch, "E1810", {"start": v(112.28, -3.5) * mm, "end": v(112.44, -3.68) * mm});
            skLineSegment(sketch, "E1811", {"start": v(112.44, -3.68) * mm, "end": v(112.58, -3.87) * mm});
            skLineSegment(sketch, "E1812", {"start": v(112.58, -3.87) * mm, "end": v(112.72, -4.09) * mm});
            skLineSegment(sketch, "E1813", {"start": v(112.72, -4.09) * mm, "end": v(112.85, -4.31) * mm});
            skLineSegment(sketch, "E1814", {"start": v(112.85, -4.31) * mm, "end": v(112.27, -5.2) * mm});
            skLineSegment(sketch, "E1815", {"start": v(112.27, -5.2) * mm, "end": v(112.01, -5.16) * mm});
            skLineSegment(sketch, "E1816", {"start": v(112.01, -5.16) * mm, "end": v(111.77, -5.12) * mm});
            skLineSegment(sketch, "E1817", {"start": v(111.77, -5.12) * mm, "end": v(111.53, -5.06) * mm});
            skLineSegment(sketch, "E1818", {"start": v(111.53, -5.06) * mm, "end": v(111.3, -4.98) * mm});
            skLineSegment(sketch, "E1819", {"start": v(111.3, -4.98) * mm, "end": v(111.09, -4.88) * mm});
            skLineSegment(sketch, "E1820", {"start": v(111.09, -4.88) * mm, "end": v(110.9, -4.76) * mm});
            skLineSegment(sketch, "E1821", {"start": v(110.9, -4.76) * mm, "end": v(110.8, -4.7) * mm});
            skLineSegment(sketch, "E1822", {"start": v(110.8, -4.7) * mm, "end": v(110.7, -4.65) * mm});
            skLineSegment(sketch, "E1823", {"start": v(110.7, -4.65) * mm, "end": v(110.63, -4.64) * mm});
            skLineSegment(sketch, "E1824", {"start": v(110.63, -4.64) * mm, "end": v(110.53, -4.67) * mm});
            skLineSegment(sketch, "E1825", {"start": v(110.53, -4.67) * mm, "end": v(109.8, -5.36) * mm});
            skLineSegment(sketch, "E1826", {"start": v(109.8, -5.36) * mm, "end": v(109.77, -5.47) * mm});
            skLineSegment(sketch, "E1827", {"start": v(109.77, -5.47) * mm, "end": v(109.78, -5.53) * mm});
            skLineSegment(sketch, "E1828", {"start": v(109.78, -5.53) * mm, "end": v(109.82, -5.64) * mm});
            skLineSegment(sketch, "E1829", {"start": v(109.82, -5.64) * mm, "end": v(109.87, -5.74) * mm});
            skLineSegment(sketch, "E1830", {"start": v(109.87, -5.74) * mm, "end": v(109.99, -5.93) * mm});
            skLineSegment(sketch, "E1831", {"start": v(109.99, -5.93) * mm, "end": v(110.07, -6.15) * mm});
            skLineSegment(sketch, "E1832", {"start": v(110.07, -6.15) * mm, "end": v(110.14, -6.38) * mm});
            skLineSegment(sketch, "E1833", {"start": v(110.14, -6.38) * mm, "end": v(110.19, -6.62) * mm});
            skLineSegment(sketch, "E1834", {"start": v(110.19, -6.62) * mm, "end": v(110.22, -6.87) * mm});
            skLineSegment(sketch, "E1835", {"start": v(110.22, -6.87) * mm, "end": v(110.24, -7.13) * mm});
            skLineSegment(sketch, "E1836", {"start": v(110.24, -7.13) * mm, "end": v(109.34, -7.67) * mm});
            skLineSegment(sketch, "E1837", {"start": v(109.34, -7.67) * mm, "end": v(109.12, -7.53) * mm});
            skLineSegment(sketch, "E1838", {"start": v(109.12, -7.53) * mm, "end": v(108.91, -7.39) * mm});
            skLineSegment(sketch, "E1839", {"start": v(108.91, -7.39) * mm, "end": v(108.72, -7.23) * mm});
            skLineSegment(sketch, "E1840", {"start": v(108.72, -7.23) * mm, "end": v(108.55, -7.06) * mm});
            skLineSegment(sketch, "E1841", {"start": v(108.55, -7.06) * mm, "end": v(108.4, -6.88) * mm});
            skLineSegment(sketch, "E1842", {"start": v(108.4, -6.88) * mm, "end": v(108.28, -6.69) * mm});
            skLineSegment(sketch, "E1843", {"start": v(108.28, -6.69) * mm, "end": v(108.22, -6.6) * mm});
            skLineSegment(sketch, "E1844", {"start": v(108.22, -6.6) * mm, "end": v(108.15, -6.5) * mm});
            skLineSegment(sketch, "E1845", {"start": v(108.15, -6.5) * mm, "end": v(108.1, -6.46) * mm});
            skLineSegment(sketch, "E1846", {"start": v(108.1, -6.46) * mm, "end": v(107.99, -6.45) * mm});
            skLineSegment(sketch, "E1847", {"start": v(107.99, -6.45) * mm, "end": v(107.04, -6.76) * mm});
            skLineSegment(sketch, "E1848", {"start": v(107.04, -6.76) * mm, "end": v(106.96, -6.83) * mm});
            skLineSegment(sketch, "E1849", {"start": v(106.96, -6.83) * mm, "end": v(106.94, -6.9) * mm});
            skLineSegment(sketch, "E1850", {"start": v(106.94, -6.9) * mm, "end": v(106.93, -7.01) * mm});
            skLineSegment(sketch, "E1851", {"start": v(106.93, -7.01) * mm, "end": v(106.94, -7.13) * mm});
            skLineSegment(sketch, "E1852", {"start": v(106.94, -7.13) * mm, "end": v(106.96, -7.35) * mm});
            skLineSegment(sketch, "E1853", {"start": v(106.96, -7.35) * mm, "end": v(106.94, -7.58) * mm});
            skLineSegment(sketch, "E1854", {"start": v(106.94, -7.58) * mm, "end": v(106.9, -7.82) * mm});
            skLineSegment(sketch, "E1855", {"start": v(106.9, -7.82) * mm, "end": v(106.84, -8.06) * mm});
            skLineSegment(sketch, "E1856", {"start": v(106.84, -8.06) * mm, "end": v(106.76, -8.3) * mm});
            skLineSegment(sketch, "E1857", {"start": v(106.76, -8.3) * mm, "end": v(106.66, -8.54) * mm});
            skLineSegment(sketch, "E1858", {"start": v(106.66, -8.54) * mm, "end": v(105.62, -8.64) * mm});
            skLineSegment(sketch, "E1859", {"start": v(105.62, -8.64) * mm, "end": v(105.48, -8.42) * mm});
            skLineSegment(sketch, "E1860", {"start": v(105.48, -8.42) * mm, "end": v(105.36, -8.2) * mm});
            skLineSegment(sketch, "E1861", {"start": v(105.36, -8.2) * mm, "end": v(105.26, -7.97) * mm});
            skLineSegment(sketch, "E1862", {"start": v(105.26, -7.97) * mm, "end": v(105.17, -7.74) * mm});
            skLineSegment(sketch, "E1863", {"start": v(105.17, -7.74) * mm, "end": v(105.12, -7.52) * mm});
            skLineSegment(sketch, "E1864", {"start": v(105.12, -7.52) * mm, "end": v(105.1, -7.3) * mm});
            skLineSegment(sketch, "E1865", {"start": v(105.1, -7.3) * mm, "end": v(105.08, -7.18) * mm});
            skLineSegment(sketch, "E1866", {"start": v(105.08, -7.18) * mm, "end": v(105.05, -7.07) * mm});
            skLineSegment(sketch, "E1867", {"start": v(105.05, -7.07) * mm, "end": v(105.02, -7) * mm});
            skLineSegment(sketch, "E1868", {"start": v(105.02, -7) * mm, "end": v(104.93, -6.95) * mm});
            skLineSegment(sketch, "E1869", {"start": v(104.93, -6.95) * mm, "end": v(103.94, -6.81) * mm});
            skLineSegment(sketch, "E1870", {"start": v(103.94, -6.81) * mm, "end": v(103.84, -6.85) * mm});
            skLineSegment(sketch, "E1871", {"start": v(103.84, -6.85) * mm, "end": v(103.8, -6.9) * mm});
            skLineSegment(sketch, "E1872", {"start": v(103.8, -6.9) * mm, "end": v(103.73, -7) * mm});
            skLineSegment(sketch, "E1873", {"start": v(103.73, -7) * mm, "end": v(103.7, -7.1) * mm});
            skLineSegment(sketch, "E1874", {"start": v(103.7, -7.1) * mm, "end": v(103.61, -7.31) * mm});
            skLineSegment(sketch, "E1875", {"start": v(103.61, -7.31) * mm, "end": v(103.5, -7.51) * mm});
            skLineSegment(sketch, "E1876", {"start": v(103.5, -7.51) * mm, "end": v(103.36, -7.71) * mm});
            skLineSegment(sketch, "E1877", {"start": v(103.36, -7.71) * mm, "end": v(103.2, -7.9) * mm});
            skLineSegment(sketch, "E1878", {"start": v(103.2, -7.9) * mm, "end": v(103.02, -8.08) * mm});
            skLineSegment(sketch, "E1879", {"start": v(103.02, -8.08) * mm, "end": v(102.83, -8.26) * mm});
            skLineSegment(sketch, "E1880", {"start": v(102.83, -8.26) * mm, "end": v(101.85, -7.89) * mm});
            skLineSegment(sketch, "E1881", {"start": v(101.85, -7.89) * mm, "end": v(101.82, -7.63) * mm});
            skLineSegment(sketch, "E1882", {"start": v(101.82, -7.63) * mm, "end": v(101.8, -7.38) * mm});
            skLineSegment(sketch, "E1883", {"start": v(101.8, -7.38) * mm, "end": v(101.81, -7.13) * mm});
            skLineSegment(sketch, "E1884", {"start": v(101.81, -7.13) * mm, "end": v(101.84, -6.9) * mm});
            skLineSegment(sketch, "E1885", {"start": v(101.84, -6.9) * mm, "end": v(101.88, -6.66) * mm});
            skLineSegment(sketch, "E1886", {"start": v(101.88, -6.66) * mm, "end": v(101.96, -6.45) * mm});
            skLineSegment(sketch, "E1887", {"start": v(101.96, -6.45) * mm, "end": v(102, -6.34) * mm});
            skLineSegment(sketch, "E1888", {"start": v(102, -6.34) * mm, "end": v(102.02, -6.23) * mm});
            skLineSegment(sketch, "E1889", {"start": v(102.02, -6.23) * mm, "end": v(102.02, -6.16) * mm});
            skLineSegment(sketch, "E1890", {"start": v(102.02, -6.16) * mm, "end": v(101.96, -6.07) * mm});
            skLineSegment(sketch, "E1891", {"start": v(101.96, -6.07) * mm, "end": v(101.13, -5.52) * mm});
            skLineSegment(sketch, "E1892", {"start": v(101.13, -5.52) * mm, "end": v(101.02, -5.5) * mm});
            skLineSegment(sketch, "E1893", {"start": v(101.02, -5.5) * mm, "end": v(100.96, -5.53) * mm});
            skLineSegment(sketch, "E1894", {"start": v(100.96, -5.53) * mm, "end": v(100.86, -5.6) * mm});
            skLineSegment(sketch, "E1895", {"start": v(100.86, -5.6) * mm, "end": v(100.78, -5.67) * mm});
            skLineSegment(sketch, "E1896", {"start": v(100.78, -5.67) * mm, "end": v(100.61, -5.83) * mm});
            skLineSegment(sketch, "E1897", {"start": v(100.61, -5.83) * mm, "end": v(100.42, -5.96) * mm});
            skLineSegment(sketch, "E1898", {"start": v(100.42, -5.96) * mm, "end": v(100.21, -6.07) * mm});
            skLineSegment(sketch, "E1899", {"start": v(100.21, -6.07) * mm, "end": v(99.99, -6.18) * mm});
            skLineSegment(sketch, "E1900", {"start": v(99.99, -6.18) * mm, "end": v(99.75, -6.27) * mm});
            skLineSegment(sketch, "E1901", {"start": v(99.75, -6.27) * mm, "end": v(99.5, -6.34) * mm});
            skLineSegment(sketch, "E1902", {"start": v(99.5, -6.34) * mm, "end": v(98.77, -5.58) * mm});
            skLineSegment(sketch, "E1903", {"start": v(98.77, -5.58) * mm, "end": v(98.86, -5.33) * mm});
            skLineSegment(sketch, "E1904", {"start": v(98.86, -5.33) * mm, "end": v(98.96, -5.1) * mm});
            skLineSegment(sketch, "E1905", {"start": v(98.96, -5.1) * mm, "end": v(99.07, -4.88) * mm});
            skLineSegment(sketch, "E1906", {"start": v(99.07, -4.88) * mm, "end": v(99.2, -4.68) * mm});
            skLineSegment(sketch, "E1907", {"start": v(99.2, -4.68) * mm, "end": v(99.34, -4.5) * mm});
            skLineSegment(sketch, "E1908", {"start": v(99.34, -4.5) * mm, "end": v(99.5, -4.33) * mm});
            skLineSegment(sketch, "E1909", {"start": v(99.5, -4.33) * mm, "end": v(99.58, -4.25) * mm});
            skLineSegment(sketch, "E1910", {"start": v(99.58, -4.25) * mm, "end": v(99.65, -4.16) * mm});
            skLineSegment(sketch, "E1911", {"start": v(99.65, -4.16) * mm, "end": v(99.67, -4.1) * mm});
            skLineSegment(sketch, "E1912", {"start": v(99.67, -4.1) * mm, "end": v(99.67, -4) * mm});
            skLineSegment(sketch, "E1913", {"start": v(99.67, -4) * mm, "end": v(99.15, -3.13) * mm});
            skLineSegment(sketch, "E1914", {"start": v(99.15, -3.13) * mm, "end": v(99.06, -3.07) * mm});
            skLineSegment(sketch, "E1915", {"start": v(99.06, -3.07) * mm, "end": v(99, -3.07) * mm});
            skLineSegment(sketch, "E1916", {"start": v(99, -3.07) * mm, "end": v(98.88, -3.09) * mm});
            skLineSegment(sketch, "E1917", {"start": v(98.88, -3.09) * mm, "end": v(98.77, -3.12) * mm});
            skLineSegment(sketch, "E1918", {"start": v(98.77, -3.12) * mm, "end": v(98.56, -3.19) * mm});
            skLineSegment(sketch, "E1919", {"start": v(98.56, -3.19) * mm, "end": v(98.33, -3.22) * mm});
            skLineSegment(sketch, "E1920", {"start": v(98.33, -3.22) * mm, "end": v(98.09, -3.24) * mm});
            skLineSegment(sketch, "E1921", {"start": v(98.09, -3.24) * mm, "end": v(97.84, -3.23) * mm});
            skLineSegment(sketch, "E1922", {"start": v(97.84, -3.23) * mm, "end": v(97.59, -3.2) * mm});
            skLineSegment(sketch, "E1923", {"start": v(97.59, -3.2) * mm, "end": v(97.33, -3.17) * mm});
            skLineSegment(sketch, "E1924", {"start": v(97.33, -3.17) * mm, "end": v(97, -2.17) * mm});
            skLineSegment(sketch, "E1925", {"start": v(97, -2.17) * mm, "end": v(97.19, -1.98) * mm});
            skLineSegment(sketch, "E1926", {"start": v(97.19, -1.98) * mm, "end": v(97.38, -1.82) * mm});
            skLineSegment(sketch, "E1927", {"start": v(97.38, -1.82) * mm, "end": v(97.58, -1.67) * mm});
            skLineSegment(sketch, "E1928", {"start": v(97.58, -1.67) * mm, "end": v(97.78, -1.54) * mm});
            skLineSegment(sketch, "E1929", {"start": v(97.78, -1.54) * mm, "end": v(97.99, -1.43) * mm});
            skLineSegment(sketch, "E1930", {"start": v(97.99, -1.43) * mm, "end": v(98.2, -1.36) * mm});
            skLineSegment(sketch, "E1931", {"start": v(98.2, -1.36) * mm, "end": v(98.3, -1.32) * mm});
            skLineSegment(sketch, "E1932", {"start": v(98.3, -1.32) * mm, "end": v(98.41, -1.27) * mm});
            skLineSegment(sketch, "E1933", {"start": v(98.41, -1.27) * mm, "end": v(98.46, -1.22) * mm});
            skLineSegment(sketch, "E1934", {"start": v(98.46, -1.22) * mm, "end": v(98.5, -1.12) * mm});
            skLineSegment(sketch, "E1935", {"start": v(98.5, -1.12) * mm, "end": v(98.4, -0.13) * mm});
            skLineSegment(sketch, "E1936", {"start": v(106.12, 0) * mm, "end": v(106.1, 0.2) * mm});
            skLineSegment(sketch, "E1937", {"start": v(106.1, 0.2) * mm, "end": v(106.02, 0.37) * mm});
            skLineSegment(sketch, "E1938", {"start": v(106.02, 0.37) * mm, "end": v(105.9, 0.53) * mm});
            skLineSegment(sketch, "E1939", {"start": v(105.9, 0.53) * mm, "end": v(105.74, 0.65) * mm});
            skLineSegment(sketch, "E1940", {"start": v(105.74, 0.65) * mm, "end": v(105.56, 0.72) * mm});
            skLineSegment(sketch, "E1941", {"start": v(105.56, 0.72) * mm, "end": v(105.37, 0.75) * mm});
            skLineSegment(sketch, "E1942", {"start": v(105.37, 0.75) * mm, "end": v(105.17, 0.72) * mm});
            skLineSegment(sketch, "E1943", {"start": v(105.17, 0.72) * mm, "end": v(105, 0.65) * mm});
            skLineSegment(sketch, "E1944", {"start": v(105, 0.65) * mm, "end": v(104.84, 0.53) * mm});
            skLineSegment(sketch, "E1945", {"start": v(104.84, 0.53) * mm, "end": v(104.72, 0.37) * mm});
            skLineSegment(sketch, "E1946", {"start": v(104.72, 0.37) * mm, "end": v(104.64, 0.2) * mm});
            skLineSegment(sketch, "E1947", {"start": v(104.64, 0.2) * mm, "end": v(104.62, 0) * mm});
            skLineSegment(sketch, "E1948", {"start": v(104.62, 0) * mm, "end": v(104.64, -0.2) * mm});
            skLineSegment(sketch, "E1949", {"start": v(104.64, -0.2) * mm, "end": v(104.72, -0.38) * mm});
            skLineSegment(sketch, "E1950", {"start": v(104.72, -0.38) * mm, "end": v(104.84, -0.53) * mm});
            skLineSegment(sketch, "E1951", {"start": v(104.84, -0.53) * mm, "end": v(105, -0.65) * mm});
            skLineSegment(sketch, "E1952", {"start": v(105, -0.65) * mm, "end": v(105.17, -0.73) * mm});
            skLineSegment(sketch, "E1953", {"start": v(105.17, -0.73) * mm, "end": v(105.37, -0.75) * mm});
            skLineSegment(sketch, "E1954", {"start": v(105.37, -0.75) * mm, "end": v(105.56, -0.73) * mm});
            skLineSegment(sketch, "E1955", {"start": v(105.56, -0.73) * mm, "end": v(105.74, -0.65) * mm});
            skLineSegment(sketch, "E1956", {"start": v(105.74, -0.65) * mm, "end": v(105.9, -0.53) * mm});
            skLineSegment(sketch, "E1957", {"start": v(105.9, -0.53) * mm, "end": v(106.02, -0.38) * mm});
            skLineSegment(sketch, "E1958", {"start": v(106.02, -0.38) * mm, "end": v(106.1, -0.2) * mm});
            skLineSegment(sketch, "E1959", {"start": v(106.1, -0.2) * mm, "end": v(106.12, 0) * mm});
            skLineSegment(sketch, "E1960", {"start": v(84.36, -10.08) * mm, "end": v(92.35, -20.23) * mm});
            skLineSegment(sketch, "E1961", {"start": v(84.48, 8.82) * mm, "end": v(93.35, 14.3) * mm});
            skLineSegment(sketch, "E1962", {"start": v(84.48, 8.82) * mm, "end": v(84.36, -10.08) * mm});
            skSolve(sketch);
        }
        {
            var Q0;
            Q0=makeQuery(id+"F0.imprint","IMPRINT",FACE,{"disambiguationData":[TD([[makeQuery(id+"F0.imprint","IMPRINT",EDGE,{"derivedFrom":sQuery(id+"F0.wireOp",EDGE,"E0")}),-1.0]])]});
            var Q1;
            Q1=makeQuery(id+"F0.imprint","IMPRINT",FACE,{"disambiguationData":[TD([[makeQuery(id+"F0.imprint","IMPRINT",EDGE,{"derivedFrom":sQuery(id+"F0.wireOp",EDGE,"E1628")}),-1.0]])]});
            extrude(context, id + "F1", {"entities" : qUnion([Q0, Q1]), "depth" : 2 * mm, "offsetDistance" : 25 * mm});
        }
    });
